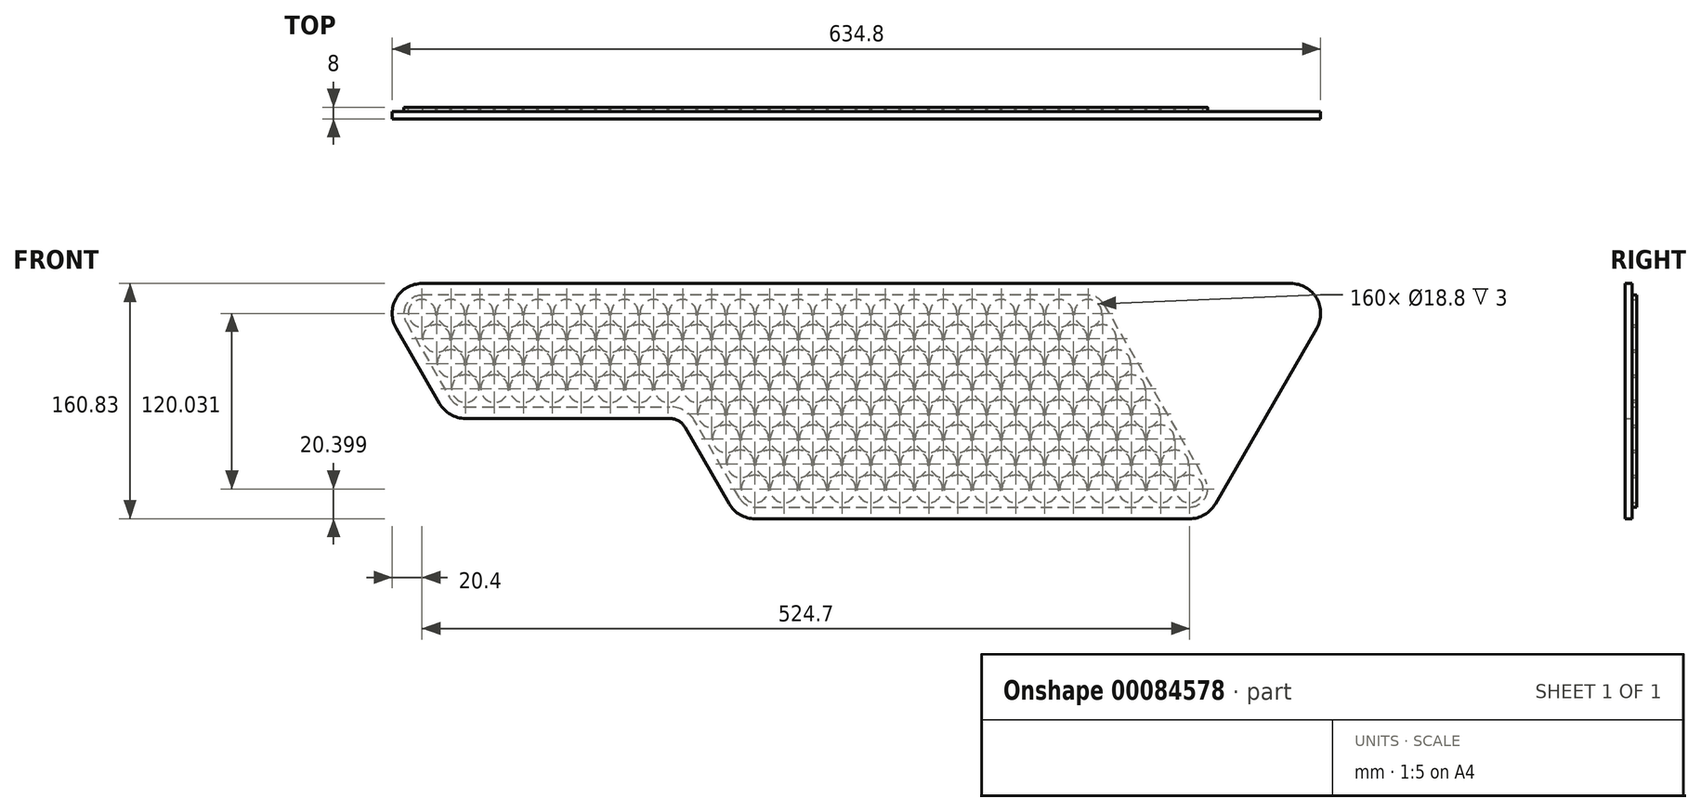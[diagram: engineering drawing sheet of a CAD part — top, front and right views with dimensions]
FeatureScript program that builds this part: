
annotation { "Feature Type Name" : "Feature", "Feature Type Description" : "" }
export const myFeature = defineFeature(function(context is Context, id is Id, definition is map)
    precondition{}
    {
        {
            var Q0;
            Q0=qCreatedBy(makeId("Front.planeOp"),FACE);
            var sketch = newSketch(context, id + "F0", { "sketchPlane" : qUnion([Q0]) });
            skCircle(sketch, "E0", {"center": v(0, 0) * mm, "radius": 9.4 * mm});
            skCircle(sketch, "E1.0.1.0", {"center": v(9.9, -17.15) * mm, "radius": 9.4 * mm});
            skCircle(sketch, "E1.0.2.0", {"center": v(19.8, -34.3) * mm, "radius": 9.4 * mm});
            skCircle(sketch, "E1.0.3.0", {"center": v(29.7, -51.44) * mm, "radius": 9.4 * mm});
            skCircle(sketch, "E1.1.0.0", {"center": v(19.8, 0) * mm, "radius": 9.4 * mm});
            skCircle(sketch, "E1.1.1.0", {"center": v(29.7, -17.15) * mm, "radius": 9.4 * mm});
            skCircle(sketch, "E1.1.2.0", {"center": v(39.6, -34.3) * mm, "radius": 9.4 * mm});
            skCircle(sketch, "E1.1.3.0", {"center": v(49.5, -51.44) * mm, "radius": 9.4 * mm});
            skCircle(sketch, "E1.2.0.0", {"center": v(39.6, 0) * mm, "radius": 9.4 * mm});
            skCircle(sketch, "E1.2.1.0", {"center": v(49.5, -17.15) * mm, "radius": 9.4 * mm});
            skCircle(sketch, "E1.2.2.0", {"center": v(59.4, -34.3) * mm, "radius": 9.4 * mm});
            skCircle(sketch, "E1.2.3.0", {"center": v(69.3, -51.44) * mm, "radius": 9.4 * mm});
            skCircle(sketch, "E1.3.0.0", {"center": v(59.4, 0) * mm, "radius": 9.4 * mm});
            skCircle(sketch, "E1.3.1.0", {"center": v(69.3, -17.15) * mm, "radius": 9.4 * mm});
            skCircle(sketch, "E1.3.2.0", {"center": v(79.2, -34.3) * mm, "radius": 9.4 * mm});
            skCircle(sketch, "E1.3.3.0", {"center": v(89.1, -51.44) * mm, "radius": 9.4 * mm});
            skCircle(sketch, "E1.4.0.0", {"center": v(79.2, 0) * mm, "radius": 9.4 * mm});
            skCircle(sketch, "E1.4.1.0", {"center": v(89.1, -17.15) * mm, "radius": 9.4 * mm});
            skCircle(sketch, "E1.4.2.0", {"center": v(99, -34.3) * mm, "radius": 9.4 * mm});
            skCircle(sketch, "E1.4.3.0", {"center": v(108.9, -51.44) * mm, "radius": 9.4 * mm});
            skCircle(sketch, "E1.5.0.0", {"center": v(99, 0) * mm, "radius": 9.4 * mm});
            skCircle(sketch, "E1.5.1.0", {"center": v(108.9, -17.15) * mm, "radius": 9.4 * mm});
            skCircle(sketch, "E1.5.2.0", {"center": v(118.8, -34.3) * mm, "radius": 9.4 * mm});
            skCircle(sketch, "E1.5.3.0", {"center": v(128.7, -51.44) * mm, "radius": 9.4 * mm});
            skCircle(sketch, "E1.6.0.0", {"center": v(118.8, 0) * mm, "radius": 9.4 * mm});
            skCircle(sketch, "E1.6.1.0", {"center": v(128.7, -17.15) * mm, "radius": 9.4 * mm});
            skCircle(sketch, "E1.6.2.0", {"center": v(138.6, -34.3) * mm, "radius": 9.4 * mm});
            skCircle(sketch, "E1.6.3.0", {"center": v(148.5, -51.44) * mm, "radius": 9.4 * mm});
            skCircle(sketch, "E1.7.0.0", {"center": v(138.6, 0) * mm, "radius": 9.4 * mm});
            skCircle(sketch, "E1.7.1.0", {"center": v(148.5, -17.15) * mm, "radius": 9.4 * mm});
            skCircle(sketch, "E1.7.2.0", {"center": v(158.4, -34.3) * mm, "radius": 9.4 * mm});
            skCircle(sketch, "E1.7.3.0", {"center": v(168.3, -51.44) * mm, "radius": 9.4 * mm});
            skCircle(sketch, "E1.8.0.0", {"center": v(158.4, 0) * mm, "radius": 9.4 * mm});
            skCircle(sketch, "E1.8.1.0", {"center": v(168.3, -17.15) * mm, "radius": 9.4 * mm});
            skCircle(sketch, "E1.8.2.0", {"center": v(178.2, -34.3) * mm, "radius": 9.4 * mm});
            skCircle(sketch, "E1.8.3.0", {"center": v(188.1, -51.44) * mm, "radius": 9.4 * mm});
            skCircle(sketch, "E1.9.0.0", {"center": v(178.2, 0) * mm, "radius": 9.4 * mm});
            skCircle(sketch, "E1.9.1.0", {"center": v(188.1, -17.15) * mm, "radius": 9.4 * mm});
            skCircle(sketch, "E1.9.2.0", {"center": v(198, -34.3) * mm, "radius": 9.4 * mm});
            skCircle(sketch, "E1.9.3.0", {"center": v(207.9, -51.44) * mm, "radius": 9.4 * mm});
            skLineSegment(sketch, "E1.direction1", {"start": v(0, 0) * mm, "end": v(19.8, 0) * mm, "construction": true});
            skLineSegment(sketch, "E1.direction2", {"start": v(0, 0) * mm, "end": v(9.9, -17.15) * mm, "construction": true});
            skCircle(sketch, "E2.0.10.0", {"center": v(198, 0) * mm, "radius": 9.4 * mm});
            skCircle(sketch, "E2.0.10.1", {"center": v(207.9, -17.15) * mm, "radius": 9.4 * mm});
            skCircle(sketch, "E2.0.10.2", {"center": v(217.8, -34.3) * mm, "radius": 9.4 * mm});
            skCircle(sketch, "E2.0.10.3", {"center": v(227.7, -51.44) * mm, "radius": 9.4 * mm});
            skCircle(sketch, "E2.0.11.0", {"center": v(217.8, 0) * mm, "radius": 9.4 * mm});
            skCircle(sketch, "E2.0.11.1", {"center": v(227.7, -17.15) * mm, "radius": 9.4 * mm});
            skCircle(sketch, "E2.0.11.2", {"center": v(237.6, -34.3) * mm, "radius": 9.4 * mm});
            skCircle(sketch, "E2.0.11.3", {"center": v(247.5, -51.44) * mm, "radius": 9.4 * mm});
            skCircle(sketch, "E2.0.12.0", {"center": v(237.6, 0) * mm, "radius": 9.4 * mm});
            skCircle(sketch, "E2.0.12.1", {"center": v(247.5, -17.15) * mm, "radius": 9.4 * mm});
            skCircle(sketch, "E2.0.12.2", {"center": v(257.4, -34.3) * mm, "radius": 9.4 * mm});
            skCircle(sketch, "E2.0.12.3", {"center": v(267.3, -51.44) * mm, "radius": 9.4 * mm});
            skCircle(sketch, "E2.0.13.0", {"center": v(257.4, 0) * mm, "radius": 9.4 * mm});
            skCircle(sketch, "E2.0.13.1", {"center": v(267.3, -17.15) * mm, "radius": 9.4 * mm});
            skCircle(sketch, "E2.0.13.2", {"center": v(277.2, -34.3) * mm, "radius": 9.4 * mm});
            skCircle(sketch, "E2.0.13.3", {"center": v(287.1, -51.44) * mm, "radius": 9.4 * mm});
            skCircle(sketch, "E2.0.14.0", {"center": v(277.2, 0) * mm, "radius": 9.4 * mm});
            skCircle(sketch, "E2.0.14.1", {"center": v(287.1, -17.15) * mm, "radius": 9.4 * mm});
            skCircle(sketch, "E2.0.14.2", {"center": v(297, -34.3) * mm, "radius": 9.4 * mm});
            skCircle(sketch, "E2.0.14.3", {"center": v(306.9, -51.44) * mm, "radius": 9.4 * mm});
            skCircle(sketch, "E2.0.15.0", {"center": v(297, 0) * mm, "radius": 9.4 * mm});
            skCircle(sketch, "E2.0.15.1", {"center": v(306.9, -17.15) * mm, "radius": 9.4 * mm});
            skCircle(sketch, "E2.0.15.2", {"center": v(316.8, -34.3) * mm, "radius": 9.4 * mm});
            skCircle(sketch, "E2.0.15.3", {"center": v(326.7, -51.44) * mm, "radius": 9.4 * mm});
            skCircle(sketch, "E2.0.16.0", {"center": v(316.8, 0) * mm, "radius": 9.4 * mm});
            skCircle(sketch, "E2.0.16.1", {"center": v(326.7, -17.15) * mm, "radius": 9.4 * mm});
            skCircle(sketch, "E2.0.16.2", {"center": v(336.6, -34.3) * mm, "radius": 9.4 * mm});
            skCircle(sketch, "E2.0.16.3", {"center": v(346.5, -51.44) * mm, "radius": 9.4 * mm});
            skCircle(sketch, "E2.0.17.0", {"center": v(336.6, 0) * mm, "radius": 9.4 * mm});
            skCircle(sketch, "E2.0.17.1", {"center": v(346.5, -17.15) * mm, "radius": 9.4 * mm});
            skCircle(sketch, "E2.0.17.2", {"center": v(356.4, -34.3) * mm, "radius": 9.4 * mm});
            skCircle(sketch, "E2.0.17.3", {"center": v(366.3, -51.44) * mm, "radius": 9.4 * mm});
            skCircle(sketch, "E2.0.18.0", {"center": v(356.4, 0) * mm, "radius": 9.4 * mm});
            skCircle(sketch, "E2.0.18.1", {"center": v(366.3, -17.15) * mm, "radius": 9.4 * mm});
            skCircle(sketch, "E2.0.18.2", {"center": v(376.2, -34.3) * mm, "radius": 9.4 * mm});
            skCircle(sketch, "E2.0.18.3", {"center": v(386.1, -51.44) * mm, "radius": 9.4 * mm});
            skCircle(sketch, "E2.0.19.0", {"center": v(376.2, 0) * mm, "radius": 9.4 * mm});
            skCircle(sketch, "E2.0.19.1", {"center": v(386.1, -17.15) * mm, "radius": 9.4 * mm});
            skCircle(sketch, "E2.0.19.2", {"center": v(396, -34.3) * mm, "radius": 9.4 * mm});
            skCircle(sketch, "E2.0.19.3", {"center": v(405.9, -51.44) * mm, "radius": 9.4 * mm});
            skCircle(sketch, "E3.0.20.0", {"center": v(396, 0) * mm, "radius": 9.4 * mm});
            skCircle(sketch, "E3.0.20.1", {"center": v(405.9, -17.15) * mm, "radius": 9.4 * mm});
            skCircle(sketch, "E3.0.20.2", {"center": v(415.8, -34.3) * mm, "radius": 9.4 * mm});
            skCircle(sketch, "E3.0.20.3", {"center": v(425.7, -51.44) * mm, "radius": 9.4 * mm});
            skCircle(sketch, "E3.0.21.0", {"center": v(415.8, 0) * mm, "radius": 9.4 * mm});
            skCircle(sketch, "E3.0.21.1", {"center": v(425.7, -17.15) * mm, "radius": 9.4 * mm});
            skCircle(sketch, "E3.0.21.2", {"center": v(435.6, -34.3) * mm, "radius": 9.4 * mm});
            skCircle(sketch, "E3.0.21.3", {"center": v(445.5, -51.44) * mm, "radius": 9.4 * mm});
            skCircle(sketch, "E3.0.22.0", {"center": v(435.6, 0) * mm, "radius": 9.4 * mm});
            skCircle(sketch, "E3.0.22.1", {"center": v(445.5, -17.15) * mm, "radius": 9.4 * mm});
            skCircle(sketch, "E3.0.22.2", {"center": v(455.4, -34.3) * mm, "radius": 9.4 * mm});
            skCircle(sketch, "E3.0.22.3", {"center": v(465.3, -51.44) * mm, "radius": 9.4 * mm});
            skCircle(sketch, "E3.0.23.0", {"center": v(455.4, 0) * mm, "radius": 9.4 * mm});
            skCircle(sketch, "E3.0.23.1", {"center": v(465.3, -17.15) * mm, "radius": 9.4 * mm});
            skCircle(sketch, "E3.0.23.2", {"center": v(475.2, -34.3) * mm, "radius": 9.4 * mm});
            skCircle(sketch, "E3.0.23.3", {"center": v(485.1, -51.44) * mm, "radius": 9.4 * mm});
            skLineSegment(sketch, "E4", {"start": v(188.1, -51.44) * mm, "end": v(158.4, 0) * mm, "construction": true});
            skLineSegment(sketch, "E5", {"start": v(237.6, 0) * mm, "end": v(207.9, -51.44) * mm, "construction": true});
            skLineSegment(sketch, "E6", {"start": v(207.9, -51.44) * mm, "end": v(188.1, -85.74) * mm, "construction": true});
            skLineSegment(sketch, "E7", {"start": v(188.1, -51.44) * mm, "end": v(207.9, -85.74) * mm, "construction": true});
            skCircle(sketch, "E8", {"center": v(198, -68.59) * mm, "radius": 9.4 * mm});
            skCircle(sketch, "E9.0.1.0", {"center": v(207.9, -85.74) * mm, "radius": 9.4 * mm});
            skCircle(sketch, "E9.0.2.0", {"center": v(217.8, -102.88) * mm, "radius": 9.4 * mm});
            skCircle(sketch, "E9.0.3.0", {"center": v(227.7, -120.03) * mm, "radius": 9.4 * mm});
            skCircle(sketch, "E9.1.0.0", {"center": v(217.8, -68.59) * mm, "radius": 9.4 * mm});
            skCircle(sketch, "E9.1.1.0", {"center": v(227.7, -85.74) * mm, "radius": 9.4 * mm});
            skCircle(sketch, "E9.1.2.0", {"center": v(237.6, -102.88) * mm, "radius": 9.4 * mm});
            skCircle(sketch, "E9.1.3.0", {"center": v(247.5, -120.03) * mm, "radius": 9.4 * mm});
            skCircle(sketch, "E9.2.0.0", {"center": v(237.6, -68.59) * mm, "radius": 9.4 * mm});
            skCircle(sketch, "E9.2.1.0", {"center": v(247.5, -85.74) * mm, "radius": 9.4 * mm});
            skCircle(sketch, "E9.2.2.0", {"center": v(257.4, -102.88) * mm, "radius": 9.4 * mm});
            skCircle(sketch, "E9.2.3.0", {"center": v(267.3, -120.03) * mm, "radius": 9.4 * mm});
            skCircle(sketch, "E9.3.0.0", {"center": v(257.4, -68.59) * mm, "radius": 9.4 * mm});
            skCircle(sketch, "E9.3.1.0", {"center": v(267.3, -85.74) * mm, "radius": 9.4 * mm});
            skCircle(sketch, "E9.3.2.0", {"center": v(277.2, -102.88) * mm, "radius": 9.4 * mm});
            skCircle(sketch, "E9.3.3.0", {"center": v(287.1, -120.03) * mm, "radius": 9.4 * mm});
            skCircle(sketch, "E9.4.0.0", {"center": v(277.2, -68.59) * mm, "radius": 9.4 * mm});
            skCircle(sketch, "E9.4.1.0", {"center": v(287.1, -85.74) * mm, "radius": 9.4 * mm});
            skCircle(sketch, "E9.4.2.0", {"center": v(297, -102.88) * mm, "radius": 9.4 * mm});
            skCircle(sketch, "E9.4.3.0", {"center": v(306.9, -120.03) * mm, "radius": 9.4 * mm});
            skCircle(sketch, "E9.5.0.0", {"center": v(297, -68.59) * mm, "radius": 9.4 * mm});
            skCircle(sketch, "E9.5.1.0", {"center": v(306.9, -85.74) * mm, "radius": 9.4 * mm});
            skCircle(sketch, "E9.5.2.0", {"center": v(316.8, -102.88) * mm, "radius": 9.4 * mm});
            skCircle(sketch, "E9.5.3.0", {"center": v(326.7, -120.03) * mm, "radius": 9.4 * mm});
            skCircle(sketch, "E9.6.0.0", {"center": v(316.8, -68.59) * mm, "radius": 9.4 * mm});
            skCircle(sketch, "E9.6.1.0", {"center": v(326.7, -85.74) * mm, "radius": 9.4 * mm});
            skCircle(sketch, "E9.6.2.0", {"center": v(336.6, -102.88) * mm, "radius": 9.4 * mm});
            skCircle(sketch, "E9.6.3.0", {"center": v(346.5, -120.03) * mm, "radius": 9.4 * mm});
            skCircle(sketch, "E9.7.0.0", {"center": v(336.6, -68.59) * mm, "radius": 9.4 * mm});
            skCircle(sketch, "E9.7.1.0", {"center": v(346.5, -85.74) * mm, "radius": 9.4 * mm});
            skCircle(sketch, "E9.7.2.0", {"center": v(356.4, -102.88) * mm, "radius": 9.4 * mm});
            skCircle(sketch, "E9.7.3.0", {"center": v(366.3, -120.03) * mm, "radius": 9.4 * mm});
            skCircle(sketch, "E9.8.0.0", {"center": v(356.4, -68.59) * mm, "radius": 9.4 * mm});
            skCircle(sketch, "E9.8.1.0", {"center": v(366.3, -85.74) * mm, "radius": 9.4 * mm});
            skCircle(sketch, "E9.8.2.0", {"center": v(376.2, -102.88) * mm, "radius": 9.4 * mm});
            skCircle(sketch, "E9.8.3.0", {"center": v(386.1, -120.03) * mm, "radius": 9.4 * mm});
            skCircle(sketch, "E9.9.0.0", {"center": v(376.2, -68.59) * mm, "radius": 9.4 * mm});
            skCircle(sketch, "E9.9.1.0", {"center": v(386.1, -85.74) * mm, "radius": 9.4 * mm});
            skCircle(sketch, "E9.9.2.0", {"center": v(396, -102.88) * mm, "radius": 9.4 * mm});
            skCircle(sketch, "E9.9.3.0", {"center": v(405.9, -120.03) * mm, "radius": 9.4 * mm});
            skCircle(sketch, "E9.10.0.0", {"center": v(396, -68.59) * mm, "radius": 9.4 * mm});
            skCircle(sketch, "E9.10.1.0", {"center": v(405.9, -85.74) * mm, "radius": 9.4 * mm});
            skCircle(sketch, "E9.10.2.0", {"center": v(415.8, -102.88) * mm, "radius": 9.4 * mm});
            skCircle(sketch, "E9.10.3.0", {"center": v(425.7, -120.03) * mm, "radius": 9.4 * mm});
            skCircle(sketch, "E9.11.0.0", {"center": v(415.8, -68.59) * mm, "radius": 9.4 * mm});
            skCircle(sketch, "E9.11.1.0", {"center": v(425.7, -85.74) * mm, "radius": 9.4 * mm});
            skCircle(sketch, "E9.11.2.0", {"center": v(435.6, -102.88) * mm, "radius": 9.4 * mm});
            skCircle(sketch, "E9.11.3.0", {"center": v(445.5, -120.03) * mm, "radius": 9.4 * mm});
            skCircle(sketch, "E9.12.0.0", {"center": v(435.6, -68.59) * mm, "radius": 9.4 * mm});
            skCircle(sketch, "E9.12.1.0", {"center": v(445.5, -85.74) * mm, "radius": 9.4 * mm});
            skCircle(sketch, "E9.12.2.0", {"center": v(455.4, -102.88) * mm, "radius": 9.4 * mm});
            skCircle(sketch, "E9.12.3.0", {"center": v(465.3, -120.03) * mm, "radius": 9.4 * mm});
            skCircle(sketch, "E9.13.0.0", {"center": v(455.4, -68.59) * mm, "radius": 9.4 * mm});
            skCircle(sketch, "E9.13.1.0", {"center": v(465.3, -85.74) * mm, "radius": 9.4 * mm});
            skCircle(sketch, "E9.13.2.0", {"center": v(475.2, -102.88) * mm, "radius": 9.4 * mm});
            skCircle(sketch, "E9.13.3.0", {"center": v(485.1, -120.03) * mm, "radius": 9.4 * mm});
            skCircle(sketch, "E9.14.0.0", {"center": v(475.2, -68.59) * mm, "radius": 9.4 * mm});
            skCircle(sketch, "E9.14.1.0", {"center": v(485.1, -85.74) * mm, "radius": 9.4 * mm});
            skCircle(sketch, "E9.14.2.0", {"center": v(495, -102.88) * mm, "radius": 9.4 * mm});
            skCircle(sketch, "E9.14.3.0", {"center": v(504.9, -120.03) * mm, "radius": 9.4 * mm});
            skCircle(sketch, "E9.15.0.0", {"center": v(495, -68.59) * mm, "radius": 9.4 * mm});
            skCircle(sketch, "E9.15.1.0", {"center": v(504.9, -85.74) * mm, "radius": 9.4 * mm});
            skCircle(sketch, "E9.15.2.0", {"center": v(514.8, -102.88) * mm, "radius": 9.4 * mm});
            skCircle(sketch, "E9.15.3.0", {"center": v(524.7, -120.03) * mm, "radius": 9.4 * mm});
            skLineSegment(sketch, "E9.direction1", {"start": v(198, -68.59) * mm, "end": v(217.8, -68.59) * mm, "construction": true});
            skLineSegment(sketch, "E9.direction2", {"start": v(198, -68.59) * mm, "end": v(207.9, -85.74) * mm, "construction": true});
            skCircle(sketch, "E10.0", {"center": v(0, 0) * mm, "radius": 12.4 * mm});
            skCircle(sketch, "E11.0", {"center": v(29.7, -51.44) * mm, "radius": 12.4 * mm});
            skCircle(sketch, "E12.0", {"center": v(455.4, 0) * mm, "radius": 12.4 * mm});
            skCircle(sketch, "E13.0", {"center": v(524.7, -120.03) * mm, "radius": 12.4 * mm});
            skCircle(sketch, "E14.0", {"center": v(227.7, -120.03) * mm, "radius": 12.4 * mm});
            skCircle(sketch, "E15.0", {"center": v(198, -68.59) * mm, "radius": 12.4 * mm});
            skLineSegment(sketch, "E16", {"start": v(-10.74, -6.2) * mm, "end": v(18.96, -57.64) * mm});
            skLineSegment(sketch, "E17", {"start": v(455.4, 12.4) * mm, "end": v(0, 12.4) * mm});
            skLineSegment(sketch, "E18", {"start": v(466.14, 6.2) * mm, "end": v(535.44, -113.83) * mm});
            skLineSegment(sketch, "E19", {"start": v(227.7, -132.43) * mm, "end": v(524.7, -132.43) * mm});
            skLineSegment(sketch, "E20", {"start": v(216.96, -126.23) * mm, "end": v(187.26, -74.79) * mm});
            skCircle(sketch, "E21.0", {"center": v(168.3, -51.44) * mm, "radius": 12.4 * mm});
            skLineSegment(sketch, "E22", {"start": v(29.7, -63.84) * mm, "end": v(168.3, -63.84) * mm});
            skLineSegment(sketch, "E23", {"start": v(168.3, -63.84) * mm, "end": v(180.94, -63.84) * mm});
            skLineSegment(sketch, "E24", {"start": v(187.26, -74.79) * mm, "end": v(180.94, -63.84) * mm});
            skSolve(sketch);
        }
        {
            var Q0;
            Q0=qSketchRegion(id+"F0",true);
            extrude(context, id + "F1", {"entities" : qUnion([Q0]), "depth" : 3 * mm});
        }
        {
            var Q0;
            Q0=makeQuery(id+"F1.opExtrude","SWEPT_EDGE",EDGE,{"disambiguationData":[OSD([sQuery(id+"F0.wireOp",EDGE,"E23"),sQuery(id+"F0.wireOp",EDGE,"E24")])]});
            fillet(context, id + "F2", {"entities" : qUnion([Q0]), "radius" : 20 * mm, "tangentPropagation" : true, "conicFillet" : false});
        }
        {
            var Q0;
            Q0=makeQuery(id+"F1.opExtrude","CAP_FACE",FACE,{"disambiguationData":[OSD([sQuery(id+"F0.wireOp",EDGE,"E0"),sQuery(id+"F0.wireOp",EDGE,"E1.0.1.0"),sQuery(id+"F0.wireOp",EDGE,"E1.0.2.0"),sQuery(id+"F0.wireOp",EDGE,"E1.0.3.0"),sQuery(id+"F0.wireOp",EDGE,"E1.1.0.0"),sQuery(id+"F0.wireOp",EDGE,"E1.1.1.0"),sQuery(id+"F0.wireOp",EDGE,"E1.1.2.0"),sQuery(id+"F0.wireOp",EDGE,"E1.1.3.0"),sQuery(id+"F0.wireOp",EDGE,"E1.2.0.0"),sQuery(id+"F0.wireOp",EDGE,"E1.2.1.0"),sQuery(id+"F0.wireOp",EDGE,"E1.2.2.0"),sQuery(id+"F0.wireOp",EDGE,"E1.2.3.0"),sQuery(id+"F0.wireOp",EDGE,"E1.3.0.0"),sQuery(id+"F0.wireOp",EDGE,"E1.3.1.0"),sQuery(id+"F0.wireOp",EDGE,"E1.3.2.0"),sQuery(id+"F0.wireOp",EDGE,"E1.3.3.0"),sQuery(id+"F0.wireOp",EDGE,"E1.4.0.0"),sQuery(id+"F0.wireOp",EDGE,"E1.4.1.0"),sQuery(id+"F0.wireOp",EDGE,"E1.4.2.0"),sQuery(id+"F0.wireOp",EDGE,"E1.4.3.0"),sQuery(id+"F0.wireOp",EDGE,"E1.5.0.0"),sQuery(id+"F0.wireOp",EDGE,"E1.5.1.0"),sQuery(id+"F0.wireOp",EDGE,"E1.5.2.0"),sQuery(id+"F0.wireOp",EDGE,"E1.5.3.0"),sQuery(id+"F0.wireOp",EDGE,"E1.6.0.0"),sQuery(id+"F0.wireOp",EDGE,"E1.6.1.0"),sQuery(id+"F0.wireOp",EDGE,"E1.6.2.0"),sQuery(id+"F0.wireOp",EDGE,"E1.6.3.0"),sQuery(id+"F0.wireOp",EDGE,"E1.7.0.0"),sQuery(id+"F0.wireOp",EDGE,"E1.7.1.0"),sQuery(id+"F0.wireOp",EDGE,"E1.7.2.0"),sQuery(id+"F0.wireOp",EDGE,"E1.7.3.0"),sQuery(id+"F0.wireOp",EDGE,"E1.8.0.0"),sQuery(id+"F0.wireOp",EDGE,"E1.8.1.0"),sQuery(id+"F0.wireOp",EDGE,"E1.8.2.0"),sQuery(id+"F0.wireOp",EDGE,"E1.8.3.0"),sQuery(id+"F0.wireOp",EDGE,"E1.9.0.0"),sQuery(id+"F0.wireOp",EDGE,"E1.9.1.0"),sQuery(id+"F0.wireOp",EDGE,"E1.9.2.0"),sQuery(id+"F0.wireOp",EDGE,"E1.9.3.0"),sQuery(id+"F0.wireOp",EDGE,"E2.0.10.0"),sQuery(id+"F0.wireOp",EDGE,"E2.0.10.1"),sQuery(id+"F0.wireOp",EDGE,"E2.0.10.2"),sQuery(id+"F0.wireOp",EDGE,"E2.0.10.3"),sQuery(id+"F0.wireOp",EDGE,"E2.0.11.0"),sQuery(id+"F0.wireOp",EDGE,"E2.0.11.1"),sQuery(id+"F0.wireOp",EDGE,"E2.0.11.2"),sQuery(id+"F0.wireOp",EDGE,"E2.0.11.3"),sQuery(id+"F0.wireOp",EDGE,"E2.0.12.0"),sQuery(id+"F0.wireOp",EDGE,"E2.0.12.1"),sQuery(id+"F0.wireOp",EDGE,"E2.0.12.2"),sQuery(id+"F0.wireOp",EDGE,"E2.0.12.3"),sQuery(id+"F0.wireOp",EDGE,"E2.0.13.0"),sQuery(id+"F0.wireOp",EDGE,"E2.0.13.1"),sQuery(id+"F0.wireOp",EDGE,"E2.0.13.2"),sQuery(id+"F0.wireOp",EDGE,"E2.0.13.3"),sQuery(id+"F0.wireOp",EDGE,"E2.0.14.0"),sQuery(id+"F0.wireOp",EDGE,"E2.0.14.1"),sQuery(id+"F0.wireOp",EDGE,"E2.0.14.2"),sQuery(id+"F0.wireOp",EDGE,"E2.0.14.3"),sQuery(id+"F0.wireOp",EDGE,"E2.0.15.0"),sQuery(id+"F0.wireOp",EDGE,"E2.0.15.1"),sQuery(id+"F0.wireOp",EDGE,"E2.0.15.2"),sQuery(id+"F0.wireOp",EDGE,"E2.0.15.3"),sQuery(id+"F0.wireOp",EDGE,"E2.0.16.0"),sQuery(id+"F0.wireOp",EDGE,"E2.0.16.1"),sQuery(id+"F0.wireOp",EDGE,"E2.0.16.2"),sQuery(id+"F0.wireOp",EDGE,"E2.0.16.3"),sQuery(id+"F0.wireOp",EDGE,"E2.0.17.0"),sQuery(id+"F0.wireOp",EDGE,"E2.0.17.1"),sQuery(id+"F0.wireOp",EDGE,"E2.0.17.2"),sQuery(id+"F0.wireOp",EDGE,"E2.0.17.3"),sQuery(id+"F0.wireOp",EDGE,"E2.0.18.0"),sQuery(id+"F0.wireOp",EDGE,"E2.0.18.1"),sQuery(id+"F0.wireOp",EDGE,"E2.0.18.2"),sQuery(id+"F0.wireOp",EDGE,"E2.0.18.3"),sQuery(id+"F0.wireOp",EDGE,"E2.0.19.0"),sQuery(id+"F0.wireOp",EDGE,"E2.0.19.1"),sQuery(id+"F0.wireOp",EDGE,"E2.0.19.2"),sQuery(id+"F0.wireOp",EDGE,"E2.0.19.3"),sQuery(id+"F0.wireOp",EDGE,"E3.0.20.0"),sQuery(id+"F0.wireOp",EDGE,"E3.0.20.1"),sQuery(id+"F0.wireOp",EDGE,"E3.0.20.2"),sQuery(id+"F0.wireOp",EDGE,"E3.0.20.3"),sQuery(id+"F0.wireOp",EDGE,"E3.0.21.0"),sQuery(id+"F0.wireOp",EDGE,"E3.0.21.1"),sQuery(id+"F0.wireOp",EDGE,"E3.0.21.2"),sQuery(id+"F0.wireOp",EDGE,"E3.0.21.3"),sQuery(id+"F0.wireOp",EDGE,"E3.0.22.0"),sQuery(id+"F0.wireOp",EDGE,"E3.0.22.1"),sQuery(id+"F0.wireOp",EDGE,"E3.0.22.2"),sQuery(id+"F0.wireOp",EDGE,"E3.0.22.3"),sQuery(id+"F0.wireOp",EDGE,"E3.0.23.0"),sQuery(id+"F0.wireOp",EDGE,"E3.0.23.1"),sQuery(id+"F0.wireOp",EDGE,"E3.0.23.2"),sQuery(id+"F0.wireOp",EDGE,"E3.0.23.3"),sQuery(id+"F0.wireOp",EDGE,"E8"),sQuery(id+"F0.wireOp",EDGE,"E9.0.1.0"),sQuery(id+"F0.wireOp",EDGE,"E9.0.2.0"),sQuery(id+"F0.wireOp",EDGE,"E9.0.3.0"),sQuery(id+"F0.wireOp",EDGE,"E9.1.0.0"),sQuery(id+"F0.wireOp",EDGE,"E9.1.1.0"),sQuery(id+"F0.wireOp",EDGE,"E9.1.2.0"),sQuery(id+"F0.wireOp",EDGE,"E9.1.3.0"),sQuery(id+"F0.wireOp",EDGE,"E9.2.0.0"),sQuery(id+"F0.wireOp",EDGE,"E9.2.1.0"),sQuery(id+"F0.wireOp",EDGE,"E9.2.2.0"),sQuery(id+"F0.wireOp",EDGE,"E9.2.3.0"),sQuery(id+"F0.wireOp",EDGE,"E9.3.0.0"),sQuery(id+"F0.wireOp",EDGE,"E9.3.1.0"),sQuery(id+"F0.wireOp",EDGE,"E9.3.2.0"),sQuery(id+"F0.wireOp",EDGE,"E9.3.3.0"),sQuery(id+"F0.wireOp",EDGE,"E9.4.0.0"),sQuery(id+"F0.wireOp",EDGE,"E9.4.1.0"),sQuery(id+"F0.wireOp",EDGE,"E9.4.2.0"),sQuery(id+"F0.wireOp",EDGE,"E9.4.3.0"),sQuery(id+"F0.wireOp",EDGE,"E9.5.0.0"),sQuery(id+"F0.wireOp",EDGE,"E9.5.1.0"),sQuery(id+"F0.wireOp",EDGE,"E9.5.2.0"),sQuery(id+"F0.wireOp",EDGE,"E9.5.3.0"),sQuery(id+"F0.wireOp",EDGE,"E9.6.0.0"),sQuery(id+"F0.wireOp",EDGE,"E9.6.1.0"),sQuery(id+"F0.wireOp",EDGE,"E9.6.2.0"),sQuery(id+"F0.wireOp",EDGE,"E9.6.3.0"),sQuery(id+"F0.wireOp",EDGE,"E9.7.0.0"),sQuery(id+"F0.wireOp",EDGE,"E9.7.1.0"),sQuery(id+"F0.wireOp",EDGE,"E9.7.2.0"),sQuery(id+"F0.wireOp",EDGE,"E9.7.3.0"),sQuery(id+"F0.wireOp",EDGE,"E9.8.0.0"),sQuery(id+"F0.wireOp",EDGE,"E9.8.1.0"),sQuery(id+"F0.wireOp",EDGE,"E9.8.2.0"),sQuery(id+"F0.wireOp",EDGE,"E9.8.3.0"),sQuery(id+"F0.wireOp",EDGE,"E9.9.0.0"),sQuery(id+"F0.wireOp",EDGE,"E9.9.1.0"),sQuery(id+"F0.wireOp",EDGE,"E9.9.2.0"),sQuery(id+"F0.wireOp",EDGE,"E9.9.3.0"),sQuery(id+"F0.wireOp",EDGE,"E9.10.0.0"),sQuery(id+"F0.wireOp",EDGE,"E9.10.1.0"),sQuery(id+"F0.wireOp",EDGE,"E9.10.2.0"),sQuery(id+"F0.wireOp",EDGE,"E9.10.3.0"),sQuery(id+"F0.wireOp",EDGE,"E9.11.0.0"),sQuery(id+"F0.wireOp",EDGE,"E9.11.1.0"),sQuery(id+"F0.wireOp",EDGE,"E9.11.2.0"),sQuery(id+"F0.wireOp",EDGE,"E9.11.3.0"),sQuery(id+"F0.wireOp",EDGE,"E9.12.0.0"),sQuery(id+"F0.wireOp",EDGE,"E9.12.1.0"),sQuery(id+"F0.wireOp",EDGE,"E9.12.2.0"),sQuery(id+"F0.wireOp",EDGE,"E9.12.3.0"),sQuery(id+"F0.wireOp",EDGE,"E9.13.0.0"),sQuery(id+"F0.wireOp",EDGE,"E9.13.1.0"),sQuery(id+"F0.wireOp",EDGE,"E9.13.2.0"),sQuery(id+"F0.wireOp",EDGE,"E9.13.3.0"),sQuery(id+"F0.wireOp",EDGE,"E9.14.0.0"),sQuery(id+"F0.wireOp",EDGE,"E9.14.1.0"),sQuery(id+"F0.wireOp",EDGE,"E9.14.2.0"),sQuery(id+"F0.wireOp",EDGE,"E9.14.3.0"),sQuery(id+"F0.wireOp",EDGE,"E9.15.0.0"),sQuery(id+"F0.wireOp",EDGE,"E9.15.1.0"),sQuery(id+"F0.wireOp",EDGE,"E9.15.2.0"),sQuery(id+"F0.wireOp",EDGE,"E9.15.3.0"),sQuery(id+"F0.wireOp",EDGE,"E10.0"),sQuery(id+"F0.wireOp",EDGE,"E11.0"),sQuery(id+"F0.wireOp",EDGE,"E12.0"),sQuery(id+"F0.wireOp",EDGE,"E13.0"),sQuery(id+"F0.wireOp",EDGE,"E14.0"),sQuery(id+"F0.wireOp",EDGE,"E16"),sQuery(id+"F0.wireOp",EDGE,"E17"),sQuery(id+"F0.wireOp",EDGE,"E18"),sQuery(id+"F0.wireOp",EDGE,"E19"),sQuery(id+"F0.wireOp",EDGE,"E20"),sQuery(id+"F0.wireOp",EDGE,"E22"),sQuery(id+"F0.wireOp",EDGE,"E23"),sQuery(id+"F0.wireOp",EDGE,"E24")])],"isStart":false});
            var sketch = newSketch(context, id + "F3", { "sketchPlane" : qUnion([Q0]) });
            skLineSegment(sketch, "E25.0", {"start": v(455.4, 12.4) * mm, "end": v(0, 12.4) * mm});
            skLineSegment(sketch, "E25.1", {"start": v(-10.74, -6.2) * mm, "end": v(18.96, -57.64) * mm});
            skLineSegment(sketch, "E25.2", {"start": v(29.7, -63.84) * mm, "end": v(169.4, -63.84) * mm});
            skLineSegment(sketch, "E25.3", {"start": v(216.96, -126.23) * mm, "end": v(186.71, -73.84) * mm});
            skLineSegment(sketch, "E25.4", {"start": v(227.7, -132.43) * mm, "end": v(524.7, -132.43) * mm});
            skLineSegment(sketch, "E25.5", {"start": v(466.14, 6.2) * mm, "end": v(535.44, -113.83) * mm});
            skArc(sketch, "E25.6", {"start": v(466.14, 6.2) * mm, "mid": v(461.6, 10.74) * mm, "end": v(455.4, 12.4) * mm});
            skArc(sketch, "E25.7", {"start": v(524.7, -132.43) * mm, "mid": v(535.44, -126.23) * mm, "end": v(535.44, -113.83) * mm});
            skArc(sketch, "E25.8", {"start": v(216.96, -126.23) * mm, "mid": v(221.5, -130.77) * mm, "end": v(227.7, -132.43) * mm});
            skArc(sketch, "E25.9", {"start": v(169.4, -63.84) * mm, "mid": v(179.4, -66.52) * mm, "end": v(186.71, -73.84) * mm});
            skArc(sketch, "E25.10", {"start": v(18.96, -57.64) * mm, "mid": v(23.5, -62.18) * mm, "end": v(29.7, -63.84) * mm});
            skArc(sketch, "E25.11", {"start": v(0, 12.4) * mm, "mid": v(-10.74, 6.2) * mm, "end": v(-10.74, -6.2) * mm});
            skSolve(sketch);
        }
        {
            var Q0;
            Q0=qSketchRegion(id+"F3",true);
            extrude(context, id + "F4", {"entities" : qUnion([Q0]), "depth" : 2 * mm});
        }
        {
            var Q0;
            Q0=makeQuery(id+"F1.opExtrude","CAP_FACE",FACE,{"disambiguationData":[OSD([sQuery(id+"F0.wireOp",EDGE,"E0"),sQuery(id+"F0.wireOp",EDGE,"E1.0.1.0"),sQuery(id+"F0.wireOp",EDGE,"E1.0.2.0"),sQuery(id+"F0.wireOp",EDGE,"E1.0.3.0"),sQuery(id+"F0.wireOp",EDGE,"E1.1.0.0"),sQuery(id+"F0.wireOp",EDGE,"E1.1.1.0"),sQuery(id+"F0.wireOp",EDGE,"E1.1.2.0"),sQuery(id+"F0.wireOp",EDGE,"E1.1.3.0"),sQuery(id+"F0.wireOp",EDGE,"E1.2.0.0"),sQuery(id+"F0.wireOp",EDGE,"E1.2.1.0"),sQuery(id+"F0.wireOp",EDGE,"E1.2.2.0"),sQuery(id+"F0.wireOp",EDGE,"E1.2.3.0"),sQuery(id+"F0.wireOp",EDGE,"E1.3.0.0"),sQuery(id+"F0.wireOp",EDGE,"E1.3.1.0"),sQuery(id+"F0.wireOp",EDGE,"E1.3.2.0"),sQuery(id+"F0.wireOp",EDGE,"E1.3.3.0"),sQuery(id+"F0.wireOp",EDGE,"E1.4.0.0"),sQuery(id+"F0.wireOp",EDGE,"E1.4.1.0"),sQuery(id+"F0.wireOp",EDGE,"E1.4.2.0"),sQuery(id+"F0.wireOp",EDGE,"E1.4.3.0"),sQuery(id+"F0.wireOp",EDGE,"E1.5.0.0"),sQuery(id+"F0.wireOp",EDGE,"E1.5.1.0"),sQuery(id+"F0.wireOp",EDGE,"E1.5.2.0"),sQuery(id+"F0.wireOp",EDGE,"E1.5.3.0"),sQuery(id+"F0.wireOp",EDGE,"E1.6.0.0"),sQuery(id+"F0.wireOp",EDGE,"E1.6.1.0"),sQuery(id+"F0.wireOp",EDGE,"E1.6.2.0"),sQuery(id+"F0.wireOp",EDGE,"E1.6.3.0"),sQuery(id+"F0.wireOp",EDGE,"E1.7.0.0"),sQuery(id+"F0.wireOp",EDGE,"E1.7.1.0"),sQuery(id+"F0.wireOp",EDGE,"E1.7.2.0"),sQuery(id+"F0.wireOp",EDGE,"E1.7.3.0"),sQuery(id+"F0.wireOp",EDGE,"E1.8.0.0"),sQuery(id+"F0.wireOp",EDGE,"E1.8.1.0"),sQuery(id+"F0.wireOp",EDGE,"E1.8.2.0"),sQuery(id+"F0.wireOp",EDGE,"E1.8.3.0"),sQuery(id+"F0.wireOp",EDGE,"E1.9.0.0"),sQuery(id+"F0.wireOp",EDGE,"E1.9.1.0"),sQuery(id+"F0.wireOp",EDGE,"E1.9.2.0"),sQuery(id+"F0.wireOp",EDGE,"E1.9.3.0"),sQuery(id+"F0.wireOp",EDGE,"E2.0.10.0"),sQuery(id+"F0.wireOp",EDGE,"E2.0.10.1"),sQuery(id+"F0.wireOp",EDGE,"E2.0.10.2"),sQuery(id+"F0.wireOp",EDGE,"E2.0.10.3"),sQuery(id+"F0.wireOp",EDGE,"E2.0.11.0"),sQuery(id+"F0.wireOp",EDGE,"E2.0.11.1"),sQuery(id+"F0.wireOp",EDGE,"E2.0.11.2"),sQuery(id+"F0.wireOp",EDGE,"E2.0.11.3"),sQuery(id+"F0.wireOp",EDGE,"E2.0.12.0"),sQuery(id+"F0.wireOp",EDGE,"E2.0.12.1"),sQuery(id+"F0.wireOp",EDGE,"E2.0.12.2"),sQuery(id+"F0.wireOp",EDGE,"E2.0.12.3"),sQuery(id+"F0.wireOp",EDGE,"E2.0.13.0"),sQuery(id+"F0.wireOp",EDGE,"E2.0.13.1"),sQuery(id+"F0.wireOp",EDGE,"E2.0.13.2"),sQuery(id+"F0.wireOp",EDGE,"E2.0.13.3"),sQuery(id+"F0.wireOp",EDGE,"E2.0.14.0"),sQuery(id+"F0.wireOp",EDGE,"E2.0.14.1"),sQuery(id+"F0.wireOp",EDGE,"E2.0.14.2"),sQuery(id+"F0.wireOp",EDGE,"E2.0.14.3"),sQuery(id+"F0.wireOp",EDGE,"E2.0.15.0"),sQuery(id+"F0.wireOp",EDGE,"E2.0.15.1"),sQuery(id+"F0.wireOp",EDGE,"E2.0.15.2"),sQuery(id+"F0.wireOp",EDGE,"E2.0.15.3"),sQuery(id+"F0.wireOp",EDGE,"E2.0.16.0"),sQuery(id+"F0.wireOp",EDGE,"E2.0.16.1"),sQuery(id+"F0.wireOp",EDGE,"E2.0.16.2"),sQuery(id+"F0.wireOp",EDGE,"E2.0.16.3"),sQuery(id+"F0.wireOp",EDGE,"E2.0.17.0"),sQuery(id+"F0.wireOp",EDGE,"E2.0.17.1"),sQuery(id+"F0.wireOp",EDGE,"E2.0.17.2"),sQuery(id+"F0.wireOp",EDGE,"E2.0.17.3"),sQuery(id+"F0.wireOp",EDGE,"E2.0.18.0"),sQuery(id+"F0.wireOp",EDGE,"E2.0.18.1"),sQuery(id+"F0.wireOp",EDGE,"E2.0.18.2"),sQuery(id+"F0.wireOp",EDGE,"E2.0.18.3"),sQuery(id+"F0.wireOp",EDGE,"E2.0.19.0"),sQuery(id+"F0.wireOp",EDGE,"E2.0.19.1"),sQuery(id+"F0.wireOp",EDGE,"E2.0.19.2"),sQuery(id+"F0.wireOp",EDGE,"E2.0.19.3"),sQuery(id+"F0.wireOp",EDGE,"E3.0.20.0"),sQuery(id+"F0.wireOp",EDGE,"E3.0.20.1"),sQuery(id+"F0.wireOp",EDGE,"E3.0.20.2"),sQuery(id+"F0.wireOp",EDGE,"E3.0.20.3"),sQuery(id+"F0.wireOp",EDGE,"E3.0.21.0"),sQuery(id+"F0.wireOp",EDGE,"E3.0.21.1"),sQuery(id+"F0.wireOp",EDGE,"E3.0.21.2"),sQuery(id+"F0.wireOp",EDGE,"E3.0.21.3"),sQuery(id+"F0.wireOp",EDGE,"E3.0.22.0"),sQuery(id+"F0.wireOp",EDGE,"E3.0.22.1"),sQuery(id+"F0.wireOp",EDGE,"E3.0.22.2"),sQuery(id+"F0.wireOp",EDGE,"E3.0.22.3"),sQuery(id+"F0.wireOp",EDGE,"E3.0.23.0"),sQuery(id+"F0.wireOp",EDGE,"E3.0.23.1"),sQuery(id+"F0.wireOp",EDGE,"E3.0.23.2"),sQuery(id+"F0.wireOp",EDGE,"E3.0.23.3"),sQuery(id+"F0.wireOp",EDGE,"E8"),sQuery(id+"F0.wireOp",EDGE,"E9.0.1.0"),sQuery(id+"F0.wireOp",EDGE,"E9.0.2.0"),sQuery(id+"F0.wireOp",EDGE,"E9.0.3.0"),sQuery(id+"F0.wireOp",EDGE,"E9.1.0.0"),sQuery(id+"F0.wireOp",EDGE,"E9.1.1.0"),sQuery(id+"F0.wireOp",EDGE,"E9.1.2.0"),sQuery(id+"F0.wireOp",EDGE,"E9.1.3.0"),sQuery(id+"F0.wireOp",EDGE,"E9.2.0.0"),sQuery(id+"F0.wireOp",EDGE,"E9.2.1.0"),sQuery(id+"F0.wireOp",EDGE,"E9.2.2.0"),sQuery(id+"F0.wireOp",EDGE,"E9.2.3.0"),sQuery(id+"F0.wireOp",EDGE,"E9.3.0.0"),sQuery(id+"F0.wireOp",EDGE,"E9.3.1.0"),sQuery(id+"F0.wireOp",EDGE,"E9.3.2.0"),sQuery(id+"F0.wireOp",EDGE,"E9.3.3.0"),sQuery(id+"F0.wireOp",EDGE,"E9.4.0.0"),sQuery(id+"F0.wireOp",EDGE,"E9.4.1.0"),sQuery(id+"F0.wireOp",EDGE,"E9.4.2.0"),sQuery(id+"F0.wireOp",EDGE,"E9.4.3.0"),sQuery(id+"F0.wireOp",EDGE,"E9.5.0.0"),sQuery(id+"F0.wireOp",EDGE,"E9.5.1.0"),sQuery(id+"F0.wireOp",EDGE,"E9.5.2.0"),sQuery(id+"F0.wireOp",EDGE,"E9.5.3.0"),sQuery(id+"F0.wireOp",EDGE,"E9.6.0.0"),sQuery(id+"F0.wireOp",EDGE,"E9.6.1.0"),sQuery(id+"F0.wireOp",EDGE,"E9.6.2.0"),sQuery(id+"F0.wireOp",EDGE,"E9.6.3.0"),sQuery(id+"F0.wireOp",EDGE,"E9.7.0.0"),sQuery(id+"F0.wireOp",EDGE,"E9.7.1.0"),sQuery(id+"F0.wireOp",EDGE,"E9.7.2.0"),sQuery(id+"F0.wireOp",EDGE,"E9.7.3.0"),sQuery(id+"F0.wireOp",EDGE,"E9.8.0.0"),sQuery(id+"F0.wireOp",EDGE,"E9.8.1.0"),sQuery(id+"F0.wireOp",EDGE,"E9.8.2.0"),sQuery(id+"F0.wireOp",EDGE,"E9.8.3.0"),sQuery(id+"F0.wireOp",EDGE,"E9.9.0.0"),sQuery(id+"F0.wireOp",EDGE,"E9.9.1.0"),sQuery(id+"F0.wireOp",EDGE,"E9.9.2.0"),sQuery(id+"F0.wireOp",EDGE,"E9.9.3.0"),sQuery(id+"F0.wireOp",EDGE,"E9.10.0.0"),sQuery(id+"F0.wireOp",EDGE,"E9.10.1.0"),sQuery(id+"F0.wireOp",EDGE,"E9.10.2.0"),sQuery(id+"F0.wireOp",EDGE,"E9.10.3.0"),sQuery(id+"F0.wireOp",EDGE,"E9.11.0.0"),sQuery(id+"F0.wireOp",EDGE,"E9.11.1.0"),sQuery(id+"F0.wireOp",EDGE,"E9.11.2.0"),sQuery(id+"F0.wireOp",EDGE,"E9.11.3.0"),sQuery(id+"F0.wireOp",EDGE,"E9.12.0.0"),sQuery(id+"F0.wireOp",EDGE,"E9.12.1.0"),sQuery(id+"F0.wireOp",EDGE,"E9.12.2.0"),sQuery(id+"F0.wireOp",EDGE,"E9.12.3.0"),sQuery(id+"F0.wireOp",EDGE,"E9.13.0.0"),sQuery(id+"F0.wireOp",EDGE,"E9.13.1.0"),sQuery(id+"F0.wireOp",EDGE,"E9.13.2.0"),sQuery(id+"F0.wireOp",EDGE,"E9.13.3.0"),sQuery(id+"F0.wireOp",EDGE,"E9.14.0.0"),sQuery(id+"F0.wireOp",EDGE,"E9.14.1.0"),sQuery(id+"F0.wireOp",EDGE,"E9.14.2.0"),sQuery(id+"F0.wireOp",EDGE,"E9.14.3.0"),sQuery(id+"F0.wireOp",EDGE,"E9.15.0.0"),sQuery(id+"F0.wireOp",EDGE,"E9.15.1.0"),sQuery(id+"F0.wireOp",EDGE,"E9.15.2.0"),sQuery(id+"F0.wireOp",EDGE,"E9.15.3.0"),sQuery(id+"F0.wireOp",EDGE,"E10.0"),sQuery(id+"F0.wireOp",EDGE,"E11.0"),sQuery(id+"F0.wireOp",EDGE,"E12.0"),sQuery(id+"F0.wireOp",EDGE,"E13.0"),sQuery(id+"F0.wireOp",EDGE,"E14.0"),sQuery(id+"F0.wireOp",EDGE,"E16"),sQuery(id+"F0.wireOp",EDGE,"E17"),sQuery(id+"F0.wireOp",EDGE,"E18"),sQuery(id+"F0.wireOp",EDGE,"E19"),sQuery(id+"F0.wireOp",EDGE,"E20"),sQuery(id+"F0.wireOp",EDGE,"E22"),sQuery(id+"F0.wireOp",EDGE,"E23"),sQuery(id+"F0.wireOp",EDGE,"E24")])],"isStart":false});
            var sketch = newSketch(context, id + "F5", { "sketchPlane" : qUnion([Q0]) });
            skArc(sketch, "E26.0", {"start": v(-8.5, 4) * mm, "mid": v(-9.4, 0) * mm, "end": v(-8.5, -4) * mm});
            skArc(sketch, "E26.1", {"start": v(21.2, -47.44) * mm, "mid": v(20.3, -51.44) * mm, "end": v(21.2, -55.44) * mm});
            skLineSegment(sketch, "E27", {"start": v(0, 0) * mm, "end": v(455.4, 0) * mm, "construction": true});
            skLineSegment(sketch, "E28", {"start": v(0, 0) * mm, "end": v(29.7, -51.44) * mm, "construction": true});
            skLineSegment(sketch, "E29", {"start": v(198, -68.59) * mm, "end": v(495, -68.59) * mm, "construction": true});
            skLineSegment(sketch, "E30", {"start": v(198, -68.59) * mm, "end": v(227.7, -120.03) * mm, "construction": true});
            skLineSegment(sketch, "E31.0.left", {"start": v(0, 4) * mm, "end": v(463.9, 4) * mm});
            skLineSegment(sketch, "E31.0.right", {"start": v(0, -4) * mm, "end": v(463.9, -4) * mm});
            skLineSegment(sketch, "E32", {"start": v(0, 4) * mm, "end": v(-8.5, 4) * mm});
            skLineSegment(sketch, "E33", {"start": v(0, -4) * mm, "end": v(-8.5, -4) * mm});
            skArc(sketch, "E34.trimOffspring", {"start": v(463.9, -4) * mm, "mid": v(464.8, 0) * mm, "end": v(463.9, 4) * mm});
            skArc(sketch, "E35.0.1.0", {"start": v(1.4, -13.15) * mm, "mid": v(0.5, -17.15) * mm, "end": v(1.4, -21.15) * mm});
            skLineSegment(sketch, "E35.0.1.1", {"start": v(9.9, -13.15) * mm, "end": v(1.4, -13.15) * mm});
            skLineSegment(sketch, "E35.0.1.2", {"start": v(9.9, -21.15) * mm, "end": v(1.4, -21.15) * mm});
            skLineSegment(sketch, "E35.0.1.3", {"start": v(9.9, -13.15) * mm, "end": v(473.8, -13.15) * mm});
            skLineSegment(sketch, "E35.0.1.4", {"start": v(9.9, -21.15) * mm, "end": v(473.8, -21.15) * mm});
            skArc(sketch, "E35.0.1.5", {"start": v(473.8, -21.15) * mm, "mid": v(474.7, -17.15) * mm, "end": v(473.8, -13.15) * mm});
            skArc(sketch, "E35.0.2.0", {"start": v(11.3, -30.3) * mm, "mid": v(10.4, -34.3) * mm, "end": v(11.3, -38.3) * mm});
            skLineSegment(sketch, "E35.0.2.1", {"start": v(19.8, -30.3) * mm, "end": v(11.3, -30.3) * mm});
            skLineSegment(sketch, "E35.0.2.2", {"start": v(19.8, -38.3) * mm, "end": v(11.3, -38.3) * mm});
            skLineSegment(sketch, "E35.0.2.3", {"start": v(19.8, -30.3) * mm, "end": v(483.7, -30.3) * mm});
            skLineSegment(sketch, "E35.0.2.4", {"start": v(19.8, -38.3) * mm, "end": v(483.7, -38.3) * mm});
            skArc(sketch, "E35.0.2.5", {"start": v(483.7, -38.3) * mm, "mid": v(484.6, -34.3) * mm, "end": v(483.7, -30.3) * mm});
            skLineSegment(sketch, "E35.0.3.1", {"start": v(29.7, -47.44) * mm, "end": v(21.2, -47.44) * mm});
            skLineSegment(sketch, "E35.0.3.2", {"start": v(29.7, -55.44) * mm, "end": v(21.2, -55.44) * mm});
            skLineSegment(sketch, "E35.0.3.3", {"start": v(29.7, -47.44) * mm, "end": v(493.6, -47.44) * mm});
            skLineSegment(sketch, "E35.0.3.4", {"start": v(29.7, -55.44) * mm, "end": v(493.6, -55.44) * mm});
            skArc(sketch, "E35.0.3.5", {"start": v(493.6, -55.44) * mm, "mid": v(494.5, -51.44) * mm, "end": v(493.6, -47.44) * mm});
            skLineSegment(sketch, "E35.direction1", {"start": v(-8.5, -4) * mm, "end": v(16.5, -4) * mm, "construction": true});
            skLineSegment(sketch, "E35.direction2", {"start": v(-8.5, -4) * mm, "end": v(1.4, -21.15) * mm, "construction": true});
            skSolve(sketch);
        }
        {
            var Q0;
            Q0=qSketchRegion(id+"F5",true);
            var Q1;
            Q1=makeQuery(id+"F4.opExtrude","CAP_FACE",FACE,{"disambiguationData":[OSD([sQuery(id+"F3.wireOp",EDGE,"E25.0"),sQuery(id+"F3.wireOp",EDGE,"E25.1"),sQuery(id+"F3.wireOp",EDGE,"E25.2"),sQuery(id+"F3.wireOp",EDGE,"E25.3"),sQuery(id+"F3.wireOp",EDGE,"E25.4"),sQuery(id+"F3.wireOp",EDGE,"E25.5"),sQuery(id+"F3.wireOp",EDGE,"E25.6"),sQuery(id+"F3.wireOp",EDGE,"E25.7"),sQuery(id+"F3.wireOp",EDGE,"E25.8"),sQuery(id+"F3.wireOp",EDGE,"E25.9"),sQuery(id+"F3.wireOp",EDGE,"E25.10"),sQuery(id+"F3.wireOp",EDGE,"E25.11")])],"isStart":false});
            extrude(context, id + "F6", {"entities" : qUnion([Q0]), "operationType" : NewBodyOperationType.REMOVE, "endBound" : BoundingType.UP_TO_SURFACE, "endBoundEntityFace" : qUnion([Q1]), "depth" : 25 * mm});
        }
        {
            var Q0;
            Q0=makeQuery(id+"F1.opExtrude","CAP_FACE",FACE,{"disambiguationData":[OSD([sQuery(id+"F0.wireOp",EDGE,"E0"),sQuery(id+"F0.wireOp",EDGE,"E1.0.1.0"),sQuery(id+"F0.wireOp",EDGE,"E1.0.2.0"),sQuery(id+"F0.wireOp",EDGE,"E1.0.3.0"),sQuery(id+"F0.wireOp",EDGE,"E1.1.0.0"),sQuery(id+"F0.wireOp",EDGE,"E1.1.1.0"),sQuery(id+"F0.wireOp",EDGE,"E1.1.2.0"),sQuery(id+"F0.wireOp",EDGE,"E1.1.3.0"),sQuery(id+"F0.wireOp",EDGE,"E1.2.0.0"),sQuery(id+"F0.wireOp",EDGE,"E1.2.1.0"),sQuery(id+"F0.wireOp",EDGE,"E1.2.2.0"),sQuery(id+"F0.wireOp",EDGE,"E1.2.3.0"),sQuery(id+"F0.wireOp",EDGE,"E1.3.0.0"),sQuery(id+"F0.wireOp",EDGE,"E1.3.1.0"),sQuery(id+"F0.wireOp",EDGE,"E1.3.2.0"),sQuery(id+"F0.wireOp",EDGE,"E1.3.3.0"),sQuery(id+"F0.wireOp",EDGE,"E1.4.0.0"),sQuery(id+"F0.wireOp",EDGE,"E1.4.1.0"),sQuery(id+"F0.wireOp",EDGE,"E1.4.2.0"),sQuery(id+"F0.wireOp",EDGE,"E1.4.3.0"),sQuery(id+"F0.wireOp",EDGE,"E1.5.0.0"),sQuery(id+"F0.wireOp",EDGE,"E1.5.1.0"),sQuery(id+"F0.wireOp",EDGE,"E1.5.2.0"),sQuery(id+"F0.wireOp",EDGE,"E1.5.3.0"),sQuery(id+"F0.wireOp",EDGE,"E1.6.0.0"),sQuery(id+"F0.wireOp",EDGE,"E1.6.1.0"),sQuery(id+"F0.wireOp",EDGE,"E1.6.2.0"),sQuery(id+"F0.wireOp",EDGE,"E1.6.3.0"),sQuery(id+"F0.wireOp",EDGE,"E1.7.0.0"),sQuery(id+"F0.wireOp",EDGE,"E1.7.1.0"),sQuery(id+"F0.wireOp",EDGE,"E1.7.2.0"),sQuery(id+"F0.wireOp",EDGE,"E1.7.3.0"),sQuery(id+"F0.wireOp",EDGE,"E1.8.0.0"),sQuery(id+"F0.wireOp",EDGE,"E1.8.1.0"),sQuery(id+"F0.wireOp",EDGE,"E1.8.2.0"),sQuery(id+"F0.wireOp",EDGE,"E1.8.3.0"),sQuery(id+"F0.wireOp",EDGE,"E1.9.0.0"),sQuery(id+"F0.wireOp",EDGE,"E1.9.1.0"),sQuery(id+"F0.wireOp",EDGE,"E1.9.2.0"),sQuery(id+"F0.wireOp",EDGE,"E1.9.3.0"),sQuery(id+"F0.wireOp",EDGE,"E2.0.10.0"),sQuery(id+"F0.wireOp",EDGE,"E2.0.10.1"),sQuery(id+"F0.wireOp",EDGE,"E2.0.10.2"),sQuery(id+"F0.wireOp",EDGE,"E2.0.10.3"),sQuery(id+"F0.wireOp",EDGE,"E2.0.11.0"),sQuery(id+"F0.wireOp",EDGE,"E2.0.11.1"),sQuery(id+"F0.wireOp",EDGE,"E2.0.11.2"),sQuery(id+"F0.wireOp",EDGE,"E2.0.11.3"),sQuery(id+"F0.wireOp",EDGE,"E2.0.12.0"),sQuery(id+"F0.wireOp",EDGE,"E2.0.12.1"),sQuery(id+"F0.wireOp",EDGE,"E2.0.12.2"),sQuery(id+"F0.wireOp",EDGE,"E2.0.12.3"),sQuery(id+"F0.wireOp",EDGE,"E2.0.13.0"),sQuery(id+"F0.wireOp",EDGE,"E2.0.13.1"),sQuery(id+"F0.wireOp",EDGE,"E2.0.13.2"),sQuery(id+"F0.wireOp",EDGE,"E2.0.13.3"),sQuery(id+"F0.wireOp",EDGE,"E2.0.14.0"),sQuery(id+"F0.wireOp",EDGE,"E2.0.14.1"),sQuery(id+"F0.wireOp",EDGE,"E2.0.14.2"),sQuery(id+"F0.wireOp",EDGE,"E2.0.14.3"),sQuery(id+"F0.wireOp",EDGE,"E2.0.15.0"),sQuery(id+"F0.wireOp",EDGE,"E2.0.15.1"),sQuery(id+"F0.wireOp",EDGE,"E2.0.15.2"),sQuery(id+"F0.wireOp",EDGE,"E2.0.15.3"),sQuery(id+"F0.wireOp",EDGE,"E2.0.16.0"),sQuery(id+"F0.wireOp",EDGE,"E2.0.16.1"),sQuery(id+"F0.wireOp",EDGE,"E2.0.16.2"),sQuery(id+"F0.wireOp",EDGE,"E2.0.16.3"),sQuery(id+"F0.wireOp",EDGE,"E2.0.17.0"),sQuery(id+"F0.wireOp",EDGE,"E2.0.17.1"),sQuery(id+"F0.wireOp",EDGE,"E2.0.17.2"),sQuery(id+"F0.wireOp",EDGE,"E2.0.17.3"),sQuery(id+"F0.wireOp",EDGE,"E2.0.18.0"),sQuery(id+"F0.wireOp",EDGE,"E2.0.18.1"),sQuery(id+"F0.wireOp",EDGE,"E2.0.18.2"),sQuery(id+"F0.wireOp",EDGE,"E2.0.18.3"),sQuery(id+"F0.wireOp",EDGE,"E2.0.19.0"),sQuery(id+"F0.wireOp",EDGE,"E2.0.19.1"),sQuery(id+"F0.wireOp",EDGE,"E2.0.19.2"),sQuery(id+"F0.wireOp",EDGE,"E2.0.19.3"),sQuery(id+"F0.wireOp",EDGE,"E3.0.20.0"),sQuery(id+"F0.wireOp",EDGE,"E3.0.20.1"),sQuery(id+"F0.wireOp",EDGE,"E3.0.20.2"),sQuery(id+"F0.wireOp",EDGE,"E3.0.20.3"),sQuery(id+"F0.wireOp",EDGE,"E3.0.21.0"),sQuery(id+"F0.wireOp",EDGE,"E3.0.21.1"),sQuery(id+"F0.wireOp",EDGE,"E3.0.21.2"),sQuery(id+"F0.wireOp",EDGE,"E3.0.21.3"),sQuery(id+"F0.wireOp",EDGE,"E3.0.22.0"),sQuery(id+"F0.wireOp",EDGE,"E3.0.22.1"),sQuery(id+"F0.wireOp",EDGE,"E3.0.22.2"),sQuery(id+"F0.wireOp",EDGE,"E3.0.22.3"),sQuery(id+"F0.wireOp",EDGE,"E3.0.23.0"),sQuery(id+"F0.wireOp",EDGE,"E3.0.23.1"),sQuery(id+"F0.wireOp",EDGE,"E3.0.23.2"),sQuery(id+"F0.wireOp",EDGE,"E3.0.23.3"),sQuery(id+"F0.wireOp",EDGE,"E8"),sQuery(id+"F0.wireOp",EDGE,"E9.0.1.0"),sQuery(id+"F0.wireOp",EDGE,"E9.0.2.0"),sQuery(id+"F0.wireOp",EDGE,"E9.0.3.0"),sQuery(id+"F0.wireOp",EDGE,"E9.1.0.0"),sQuery(id+"F0.wireOp",EDGE,"E9.1.1.0"),sQuery(id+"F0.wireOp",EDGE,"E9.1.2.0"),sQuery(id+"F0.wireOp",EDGE,"E9.1.3.0"),sQuery(id+"F0.wireOp",EDGE,"E9.2.0.0"),sQuery(id+"F0.wireOp",EDGE,"E9.2.1.0"),sQuery(id+"F0.wireOp",EDGE,"E9.2.2.0"),sQuery(id+"F0.wireOp",EDGE,"E9.2.3.0"),sQuery(id+"F0.wireOp",EDGE,"E9.3.0.0"),sQuery(id+"F0.wireOp",EDGE,"E9.3.1.0"),sQuery(id+"F0.wireOp",EDGE,"E9.3.2.0"),sQuery(id+"F0.wireOp",EDGE,"E9.3.3.0"),sQuery(id+"F0.wireOp",EDGE,"E9.4.0.0"),sQuery(id+"F0.wireOp",EDGE,"E9.4.1.0"),sQuery(id+"F0.wireOp",EDGE,"E9.4.2.0"),sQuery(id+"F0.wireOp",EDGE,"E9.4.3.0"),sQuery(id+"F0.wireOp",EDGE,"E9.5.0.0"),sQuery(id+"F0.wireOp",EDGE,"E9.5.1.0"),sQuery(id+"F0.wireOp",EDGE,"E9.5.2.0"),sQuery(id+"F0.wireOp",EDGE,"E9.5.3.0"),sQuery(id+"F0.wireOp",EDGE,"E9.6.0.0"),sQuery(id+"F0.wireOp",EDGE,"E9.6.1.0"),sQuery(id+"F0.wireOp",EDGE,"E9.6.2.0"),sQuery(id+"F0.wireOp",EDGE,"E9.6.3.0"),sQuery(id+"F0.wireOp",EDGE,"E9.7.0.0"),sQuery(id+"F0.wireOp",EDGE,"E9.7.1.0"),sQuery(id+"F0.wireOp",EDGE,"E9.7.2.0"),sQuery(id+"F0.wireOp",EDGE,"E9.7.3.0"),sQuery(id+"F0.wireOp",EDGE,"E9.8.0.0"),sQuery(id+"F0.wireOp",EDGE,"E9.8.1.0"),sQuery(id+"F0.wireOp",EDGE,"E9.8.2.0"),sQuery(id+"F0.wireOp",EDGE,"E9.8.3.0"),sQuery(id+"F0.wireOp",EDGE,"E9.9.0.0"),sQuery(id+"F0.wireOp",EDGE,"E9.9.1.0"),sQuery(id+"F0.wireOp",EDGE,"E9.9.2.0"),sQuery(id+"F0.wireOp",EDGE,"E9.9.3.0"),sQuery(id+"F0.wireOp",EDGE,"E9.10.0.0"),sQuery(id+"F0.wireOp",EDGE,"E9.10.1.0"),sQuery(id+"F0.wireOp",EDGE,"E9.10.2.0"),sQuery(id+"F0.wireOp",EDGE,"E9.10.3.0"),sQuery(id+"F0.wireOp",EDGE,"E9.11.0.0"),sQuery(id+"F0.wireOp",EDGE,"E9.11.1.0"),sQuery(id+"F0.wireOp",EDGE,"E9.11.2.0"),sQuery(id+"F0.wireOp",EDGE,"E9.11.3.0"),sQuery(id+"F0.wireOp",EDGE,"E9.12.0.0"),sQuery(id+"F0.wireOp",EDGE,"E9.12.1.0"),sQuery(id+"F0.wireOp",EDGE,"E9.12.2.0"),sQuery(id+"F0.wireOp",EDGE,"E9.12.3.0"),sQuery(id+"F0.wireOp",EDGE,"E9.13.0.0"),sQuery(id+"F0.wireOp",EDGE,"E9.13.1.0"),sQuery(id+"F0.wireOp",EDGE,"E9.13.2.0"),sQuery(id+"F0.wireOp",EDGE,"E9.13.3.0"),sQuery(id+"F0.wireOp",EDGE,"E9.14.0.0"),sQuery(id+"F0.wireOp",EDGE,"E9.14.1.0"),sQuery(id+"F0.wireOp",EDGE,"E9.14.2.0"),sQuery(id+"F0.wireOp",EDGE,"E9.14.3.0"),sQuery(id+"F0.wireOp",EDGE,"E9.15.0.0"),sQuery(id+"F0.wireOp",EDGE,"E9.15.1.0"),sQuery(id+"F0.wireOp",EDGE,"E9.15.2.0"),sQuery(id+"F0.wireOp",EDGE,"E9.15.3.0"),sQuery(id+"F0.wireOp",EDGE,"E10.0"),sQuery(id+"F0.wireOp",EDGE,"E11.0"),sQuery(id+"F0.wireOp",EDGE,"E12.0"),sQuery(id+"F0.wireOp",EDGE,"E13.0"),sQuery(id+"F0.wireOp",EDGE,"E14.0"),sQuery(id+"F0.wireOp",EDGE,"E16"),sQuery(id+"F0.wireOp",EDGE,"E17"),sQuery(id+"F0.wireOp",EDGE,"E18"),sQuery(id+"F0.wireOp",EDGE,"E19"),sQuery(id+"F0.wireOp",EDGE,"E20"),sQuery(id+"F0.wireOp",EDGE,"E22"),sQuery(id+"F0.wireOp",EDGE,"E23"),sQuery(id+"F0.wireOp",EDGE,"E24")])],"isStart":false});
            var sketch = newSketch(context, id + "F7", { "sketchPlane" : qUnion([Q0]) });
            skArc(sketch, "E36.0", {"start": v(189.5, -64.59) * mm, "mid": v(188.6, -68.59) * mm, "end": v(189.5, -72.59) * mm});
            skArc(sketch, "E36.1", {"start": v(219.2, -116.03) * mm, "mid": v(218.3, -120.03) * mm, "end": v(219.2, -124.03) * mm});
            skLineSegment(sketch, "E37", {"start": v(198, -68.59) * mm, "end": v(495, -68.59) * mm, "construction": true});
            skLineSegment(sketch, "E38", {"start": v(198, -68.59) * mm, "end": v(227.7, -120.03) * mm, "construction": true});
            skLineSegment(sketch, "E39.0.left", {"start": v(198, -64.59) * mm, "end": v(495, -64.59) * mm});
            skLineSegment(sketch, "E39.0.right", {"start": v(198, -72.59) * mm, "end": v(495, -72.59) * mm});
            skLineSegment(sketch, "E40", {"start": v(198, -64.59) * mm, "end": v(189.5, -64.59) * mm});
            skLineSegment(sketch, "E41", {"start": v(198, -72.59) * mm, "end": v(189.5, -72.59) * mm});
            skLineSegment(sketch, "E42", {"start": v(495, -64.59) * mm, "end": v(503.5, -64.59) * mm});
            skLineSegment(sketch, "E43", {"start": v(495, -72.59) * mm, "end": v(503.5, -72.59) * mm});
            skArc(sketch, "E44.trimOffspring", {"start": v(503.5, -72.59) * mm, "mid": v(504.4, -68.59) * mm, "end": v(503.5, -64.59) * mm});
            skArc(sketch, "E45.0.1.0", {"start": v(199.4, -81.74) * mm, "mid": v(198.5, -85.74) * mm, "end": v(199.4, -89.74) * mm});
            skLineSegment(sketch, "E45.0.1.1", {"start": v(207.9, -81.74) * mm, "end": v(504.9, -81.74) * mm});
            skLineSegment(sketch, "E45.0.1.2", {"start": v(207.9, -89.74) * mm, "end": v(504.9, -89.74) * mm});
            skLineSegment(sketch, "E45.0.1.3", {"start": v(207.9, -81.74) * mm, "end": v(199.4, -81.74) * mm});
            skLineSegment(sketch, "E45.0.1.4", {"start": v(207.9, -89.74) * mm, "end": v(199.4, -89.74) * mm});
            skLineSegment(sketch, "E45.0.1.5", {"start": v(504.9, -81.74) * mm, "end": v(513.4, -81.74) * mm});
            skLineSegment(sketch, "E45.0.1.6", {"start": v(504.9, -89.74) * mm, "end": v(513.4, -89.74) * mm});
            skArc(sketch, "E45.0.1.7", {"start": v(513.4, -89.74) * mm, "mid": v(514.3, -85.74) * mm, "end": v(513.4, -81.74) * mm});
            skArc(sketch, "E45.0.2.0", {"start": v(209.3, -98.88) * mm, "mid": v(208.4, -102.88) * mm, "end": v(209.3, -106.88) * mm});
            skLineSegment(sketch, "E45.0.2.1", {"start": v(217.8, -98.88) * mm, "end": v(514.8, -98.88) * mm});
            skLineSegment(sketch, "E45.0.2.2", {"start": v(217.8, -106.88) * mm, "end": v(514.8, -106.88) * mm});
            skLineSegment(sketch, "E45.0.2.3", {"start": v(217.8, -98.88) * mm, "end": v(209.3, -98.88) * mm});
            skLineSegment(sketch, "E45.0.2.4", {"start": v(217.8, -106.88) * mm, "end": v(209.3, -106.88) * mm});
            skLineSegment(sketch, "E45.0.2.5", {"start": v(514.8, -98.88) * mm, "end": v(523.3, -98.88) * mm});
            skLineSegment(sketch, "E45.0.2.6", {"start": v(514.8, -106.88) * mm, "end": v(523.3, -106.88) * mm});
            skArc(sketch, "E45.0.2.7", {"start": v(523.3, -106.88) * mm, "mid": v(524.2, -102.88) * mm, "end": v(523.3, -98.88) * mm});
            skLineSegment(sketch, "E45.0.3.1", {"start": v(227.7, -116.03) * mm, "end": v(524.7, -116.03) * mm});
            skLineSegment(sketch, "E45.0.3.2", {"start": v(227.7, -124.03) * mm, "end": v(524.7, -124.03) * mm});
            skLineSegment(sketch, "E45.0.3.3", {"start": v(227.7, -116.03) * mm, "end": v(219.2, -116.03) * mm});
            skLineSegment(sketch, "E45.0.3.4", {"start": v(227.7, -124.03) * mm, "end": v(219.2, -124.03) * mm});
            skLineSegment(sketch, "E45.0.3.5", {"start": v(524.7, -116.03) * mm, "end": v(533.2, -116.03) * mm});
            skLineSegment(sketch, "E45.0.3.6", {"start": v(524.7, -124.03) * mm, "end": v(533.2, -124.03) * mm});
            skArc(sketch, "E45.0.3.7", {"start": v(533.2, -124.03) * mm, "mid": v(534.1, -120.03) * mm, "end": v(533.2, -116.03) * mm});
            skLineSegment(sketch, "E45.direction1", {"start": v(189.5, -72.59) * mm, "end": v(214.5, -72.59) * mm, "construction": true});
            skLineSegment(sketch, "E45.direction2", {"start": v(189.5, -72.59) * mm, "end": v(199.4, -89.74) * mm, "construction": true});
            skSolve(sketch);
        }
        {
            var Q0;
            Q0=qSketchRegion(id+"F7",true);
            var Q1;
            Q1=makeQuery(id+"F4.opExtrude","CAP_FACE",FACE,{"disambiguationData":[OSD([sQuery(id+"F3.wireOp",EDGE,"E25.0"),sQuery(id+"F3.wireOp",EDGE,"E25.1"),sQuery(id+"F3.wireOp",EDGE,"E25.2"),sQuery(id+"F3.wireOp",EDGE,"E25.3"),sQuery(id+"F3.wireOp",EDGE,"E25.4"),sQuery(id+"F3.wireOp",EDGE,"E25.5"),sQuery(id+"F3.wireOp",EDGE,"E25.6"),sQuery(id+"F3.wireOp",EDGE,"E25.7"),sQuery(id+"F3.wireOp",EDGE,"E25.8"),sQuery(id+"F3.wireOp",EDGE,"E25.9"),sQuery(id+"F3.wireOp",EDGE,"E25.10"),sQuery(id+"F3.wireOp",EDGE,"E25.11")])],"isStart":false});
            extrude(context, id + "F8", {"entities" : qUnion([Q0]), "operationType" : NewBodyOperationType.REMOVE, "endBound" : BoundingType.UP_TO_SURFACE, "endBoundEntityFace" : qUnion([Q1]), "depth" : 25 * mm});
        }
        {
            var Q0;
            Q0=makeQuery(id+"F1.opExtrude","CAP_FACE",FACE,{"disambiguationData":[OSD([sQuery(id+"F0.wireOp",EDGE,"E0"),sQuery(id+"F0.wireOp",EDGE,"E1.0.1.0"),sQuery(id+"F0.wireOp",EDGE,"E1.0.2.0"),sQuery(id+"F0.wireOp",EDGE,"E1.0.3.0"),sQuery(id+"F0.wireOp",EDGE,"E1.1.0.0"),sQuery(id+"F0.wireOp",EDGE,"E1.1.1.0"),sQuery(id+"F0.wireOp",EDGE,"E1.1.2.0"),sQuery(id+"F0.wireOp",EDGE,"E1.1.3.0"),sQuery(id+"F0.wireOp",EDGE,"E1.2.0.0"),sQuery(id+"F0.wireOp",EDGE,"E1.2.1.0"),sQuery(id+"F0.wireOp",EDGE,"E1.2.2.0"),sQuery(id+"F0.wireOp",EDGE,"E1.2.3.0"),sQuery(id+"F0.wireOp",EDGE,"E1.3.0.0"),sQuery(id+"F0.wireOp",EDGE,"E1.3.1.0"),sQuery(id+"F0.wireOp",EDGE,"E1.3.2.0"),sQuery(id+"F0.wireOp",EDGE,"E1.3.3.0"),sQuery(id+"F0.wireOp",EDGE,"E1.4.0.0"),sQuery(id+"F0.wireOp",EDGE,"E1.4.1.0"),sQuery(id+"F0.wireOp",EDGE,"E1.4.2.0"),sQuery(id+"F0.wireOp",EDGE,"E1.4.3.0"),sQuery(id+"F0.wireOp",EDGE,"E1.5.0.0"),sQuery(id+"F0.wireOp",EDGE,"E1.5.1.0"),sQuery(id+"F0.wireOp",EDGE,"E1.5.2.0"),sQuery(id+"F0.wireOp",EDGE,"E1.5.3.0"),sQuery(id+"F0.wireOp",EDGE,"E1.6.0.0"),sQuery(id+"F0.wireOp",EDGE,"E1.6.1.0"),sQuery(id+"F0.wireOp",EDGE,"E1.6.2.0"),sQuery(id+"F0.wireOp",EDGE,"E1.6.3.0"),sQuery(id+"F0.wireOp",EDGE,"E1.7.0.0"),sQuery(id+"F0.wireOp",EDGE,"E1.7.1.0"),sQuery(id+"F0.wireOp",EDGE,"E1.7.2.0"),sQuery(id+"F0.wireOp",EDGE,"E1.7.3.0"),sQuery(id+"F0.wireOp",EDGE,"E1.8.0.0"),sQuery(id+"F0.wireOp",EDGE,"E1.8.1.0"),sQuery(id+"F0.wireOp",EDGE,"E1.8.2.0"),sQuery(id+"F0.wireOp",EDGE,"E1.8.3.0"),sQuery(id+"F0.wireOp",EDGE,"E1.9.0.0"),sQuery(id+"F0.wireOp",EDGE,"E1.9.1.0"),sQuery(id+"F0.wireOp",EDGE,"E1.9.2.0"),sQuery(id+"F0.wireOp",EDGE,"E1.9.3.0"),sQuery(id+"F0.wireOp",EDGE,"E2.0.10.0"),sQuery(id+"F0.wireOp",EDGE,"E2.0.10.1"),sQuery(id+"F0.wireOp",EDGE,"E2.0.10.2"),sQuery(id+"F0.wireOp",EDGE,"E2.0.10.3"),sQuery(id+"F0.wireOp",EDGE,"E2.0.11.0"),sQuery(id+"F0.wireOp",EDGE,"E2.0.11.1"),sQuery(id+"F0.wireOp",EDGE,"E2.0.11.2"),sQuery(id+"F0.wireOp",EDGE,"E2.0.11.3"),sQuery(id+"F0.wireOp",EDGE,"E2.0.12.0"),sQuery(id+"F0.wireOp",EDGE,"E2.0.12.1"),sQuery(id+"F0.wireOp",EDGE,"E2.0.12.2"),sQuery(id+"F0.wireOp",EDGE,"E2.0.12.3"),sQuery(id+"F0.wireOp",EDGE,"E2.0.13.0"),sQuery(id+"F0.wireOp",EDGE,"E2.0.13.1"),sQuery(id+"F0.wireOp",EDGE,"E2.0.13.2"),sQuery(id+"F0.wireOp",EDGE,"E2.0.13.3"),sQuery(id+"F0.wireOp",EDGE,"E2.0.14.0"),sQuery(id+"F0.wireOp",EDGE,"E2.0.14.1"),sQuery(id+"F0.wireOp",EDGE,"E2.0.14.2"),sQuery(id+"F0.wireOp",EDGE,"E2.0.14.3"),sQuery(id+"F0.wireOp",EDGE,"E2.0.15.0"),sQuery(id+"F0.wireOp",EDGE,"E2.0.15.1"),sQuery(id+"F0.wireOp",EDGE,"E2.0.15.2"),sQuery(id+"F0.wireOp",EDGE,"E2.0.15.3"),sQuery(id+"F0.wireOp",EDGE,"E2.0.16.0"),sQuery(id+"F0.wireOp",EDGE,"E2.0.16.1"),sQuery(id+"F0.wireOp",EDGE,"E2.0.16.2"),sQuery(id+"F0.wireOp",EDGE,"E2.0.16.3"),sQuery(id+"F0.wireOp",EDGE,"E2.0.17.0"),sQuery(id+"F0.wireOp",EDGE,"E2.0.17.1"),sQuery(id+"F0.wireOp",EDGE,"E2.0.17.2"),sQuery(id+"F0.wireOp",EDGE,"E2.0.17.3"),sQuery(id+"F0.wireOp",EDGE,"E2.0.18.0"),sQuery(id+"F0.wireOp",EDGE,"E2.0.18.1"),sQuery(id+"F0.wireOp",EDGE,"E2.0.18.2"),sQuery(id+"F0.wireOp",EDGE,"E2.0.18.3"),sQuery(id+"F0.wireOp",EDGE,"E2.0.19.0"),sQuery(id+"F0.wireOp",EDGE,"E2.0.19.1"),sQuery(id+"F0.wireOp",EDGE,"E2.0.19.2"),sQuery(id+"F0.wireOp",EDGE,"E2.0.19.3"),sQuery(id+"F0.wireOp",EDGE,"E3.0.20.0"),sQuery(id+"F0.wireOp",EDGE,"E3.0.20.1"),sQuery(id+"F0.wireOp",EDGE,"E3.0.20.2"),sQuery(id+"F0.wireOp",EDGE,"E3.0.20.3"),sQuery(id+"F0.wireOp",EDGE,"E3.0.21.0"),sQuery(id+"F0.wireOp",EDGE,"E3.0.21.1"),sQuery(id+"F0.wireOp",EDGE,"E3.0.21.2"),sQuery(id+"F0.wireOp",EDGE,"E3.0.21.3"),sQuery(id+"F0.wireOp",EDGE,"E3.0.22.0"),sQuery(id+"F0.wireOp",EDGE,"E3.0.22.1"),sQuery(id+"F0.wireOp",EDGE,"E3.0.22.2"),sQuery(id+"F0.wireOp",EDGE,"E3.0.22.3"),sQuery(id+"F0.wireOp",EDGE,"E3.0.23.0"),sQuery(id+"F0.wireOp",EDGE,"E3.0.23.1"),sQuery(id+"F0.wireOp",EDGE,"E3.0.23.2"),sQuery(id+"F0.wireOp",EDGE,"E3.0.23.3"),sQuery(id+"F0.wireOp",EDGE,"E8"),sQuery(id+"F0.wireOp",EDGE,"E9.0.1.0"),sQuery(id+"F0.wireOp",EDGE,"E9.0.2.0"),sQuery(id+"F0.wireOp",EDGE,"E9.0.3.0"),sQuery(id+"F0.wireOp",EDGE,"E9.1.0.0"),sQuery(id+"F0.wireOp",EDGE,"E9.1.1.0"),sQuery(id+"F0.wireOp",EDGE,"E9.1.2.0"),sQuery(id+"F0.wireOp",EDGE,"E9.1.3.0"),sQuery(id+"F0.wireOp",EDGE,"E9.2.0.0"),sQuery(id+"F0.wireOp",EDGE,"E9.2.1.0"),sQuery(id+"F0.wireOp",EDGE,"E9.2.2.0"),sQuery(id+"F0.wireOp",EDGE,"E9.2.3.0"),sQuery(id+"F0.wireOp",EDGE,"E9.3.0.0"),sQuery(id+"F0.wireOp",EDGE,"E9.3.1.0"),sQuery(id+"F0.wireOp",EDGE,"E9.3.2.0"),sQuery(id+"F0.wireOp",EDGE,"E9.3.3.0"),sQuery(id+"F0.wireOp",EDGE,"E9.4.0.0"),sQuery(id+"F0.wireOp",EDGE,"E9.4.1.0"),sQuery(id+"F0.wireOp",EDGE,"E9.4.2.0"),sQuery(id+"F0.wireOp",EDGE,"E9.4.3.0"),sQuery(id+"F0.wireOp",EDGE,"E9.5.0.0"),sQuery(id+"F0.wireOp",EDGE,"E9.5.1.0"),sQuery(id+"F0.wireOp",EDGE,"E9.5.2.0"),sQuery(id+"F0.wireOp",EDGE,"E9.5.3.0"),sQuery(id+"F0.wireOp",EDGE,"E9.6.0.0"),sQuery(id+"F0.wireOp",EDGE,"E9.6.1.0"),sQuery(id+"F0.wireOp",EDGE,"E9.6.2.0"),sQuery(id+"F0.wireOp",EDGE,"E9.6.3.0"),sQuery(id+"F0.wireOp",EDGE,"E9.7.0.0"),sQuery(id+"F0.wireOp",EDGE,"E9.7.1.0"),sQuery(id+"F0.wireOp",EDGE,"E9.7.2.0"),sQuery(id+"F0.wireOp",EDGE,"E9.7.3.0"),sQuery(id+"F0.wireOp",EDGE,"E9.8.0.0"),sQuery(id+"F0.wireOp",EDGE,"E9.8.1.0"),sQuery(id+"F0.wireOp",EDGE,"E9.8.2.0"),sQuery(id+"F0.wireOp",EDGE,"E9.8.3.0"),sQuery(id+"F0.wireOp",EDGE,"E9.9.0.0"),sQuery(id+"F0.wireOp",EDGE,"E9.9.1.0"),sQuery(id+"F0.wireOp",EDGE,"E9.9.2.0"),sQuery(id+"F0.wireOp",EDGE,"E9.9.3.0"),sQuery(id+"F0.wireOp",EDGE,"E9.10.0.0"),sQuery(id+"F0.wireOp",EDGE,"E9.10.1.0"),sQuery(id+"F0.wireOp",EDGE,"E9.10.2.0"),sQuery(id+"F0.wireOp",EDGE,"E9.10.3.0"),sQuery(id+"F0.wireOp",EDGE,"E9.11.0.0"),sQuery(id+"F0.wireOp",EDGE,"E9.11.1.0"),sQuery(id+"F0.wireOp",EDGE,"E9.11.2.0"),sQuery(id+"F0.wireOp",EDGE,"E9.11.3.0"),sQuery(id+"F0.wireOp",EDGE,"E9.12.0.0"),sQuery(id+"F0.wireOp",EDGE,"E9.12.1.0"),sQuery(id+"F0.wireOp",EDGE,"E9.12.2.0"),sQuery(id+"F0.wireOp",EDGE,"E9.12.3.0"),sQuery(id+"F0.wireOp",EDGE,"E9.13.0.0"),sQuery(id+"F0.wireOp",EDGE,"E9.13.1.0"),sQuery(id+"F0.wireOp",EDGE,"E9.13.2.0"),sQuery(id+"F0.wireOp",EDGE,"E9.13.3.0"),sQuery(id+"F0.wireOp",EDGE,"E9.14.0.0"),sQuery(id+"F0.wireOp",EDGE,"E9.14.1.0"),sQuery(id+"F0.wireOp",EDGE,"E9.14.2.0"),sQuery(id+"F0.wireOp",EDGE,"E9.14.3.0"),sQuery(id+"F0.wireOp",EDGE,"E9.15.0.0"),sQuery(id+"F0.wireOp",EDGE,"E9.15.1.0"),sQuery(id+"F0.wireOp",EDGE,"E9.15.2.0"),sQuery(id+"F0.wireOp",EDGE,"E9.15.3.0"),sQuery(id+"F0.wireOp",EDGE,"E10.0"),sQuery(id+"F0.wireOp",EDGE,"E11.0"),sQuery(id+"F0.wireOp",EDGE,"E12.0"),sQuery(id+"F0.wireOp",EDGE,"E13.0"),sQuery(id+"F0.wireOp",EDGE,"E14.0"),sQuery(id+"F0.wireOp",EDGE,"E16"),sQuery(id+"F0.wireOp",EDGE,"E17"),sQuery(id+"F0.wireOp",EDGE,"E18"),sQuery(id+"F0.wireOp",EDGE,"E19"),sQuery(id+"F0.wireOp",EDGE,"E20"),sQuery(id+"F0.wireOp",EDGE,"E22"),sQuery(id+"F0.wireOp",EDGE,"E23"),sQuery(id+"F0.wireOp",EDGE,"E24")])],"isStart":false});
            var sketch = newSketch(context, id + "F9", { "sketchPlane" : qUnion([Q0]) });
            skArc(sketch, "E46.0", {"start": v(-0.79, 9.37) * mm, "mid": v(-4.7, 8.14) * mm, "end": v(-7.72, 5.37) * mm});
            skArc(sketch, "E46.1", {"start": v(30.49, -60.8) * mm, "mid": v(34.4, -59.58) * mm, "end": v(37.42, -56.8) * mm});
            skLineSegment(sketch, "E47", {"start": v(0, 0) * mm, "end": v(29.7, -51.44) * mm, "construction": true});
            skLineSegment(sketch, "E48.0.left", {"start": v(3.46, 2) * mm, "end": v(33.16, -49.44) * mm});
            skLineSegment(sketch, "E48.0.right", {"start": v(-3.46, -2) * mm, "end": v(26.24, -53.44) * mm});
            skLineSegment(sketch, "E49", {"start": v(3.46, 2) * mm, "end": v(-0.79, 9.37) * mm});
            skLineSegment(sketch, "E50", {"start": v(-3.46, -2) * mm, "end": v(-7.72, 5.37) * mm});
            skLineSegment(sketch, "E51", {"start": v(26.24, -53.44) * mm, "end": v(30.49, -60.8) * mm});
            skLineSegment(sketch, "E52", {"start": v(33.16, -49.44) * mm, "end": v(37.42, -56.8) * mm});
            skArc(sketch, "E53.1.0.0", {"start": v(19.01, 9.37) * mm, "mid": v(15.1, 8.14) * mm, "end": v(12.08, 5.37) * mm});
            skLineSegment(sketch, "E53.1.0.1", {"start": v(16.34, -2) * mm, "end": v(12.08, 5.37) * mm});
            skLineSegment(sketch, "E53.1.0.2", {"start": v(23.26, 2) * mm, "end": v(19.01, 9.37) * mm});
            skLineSegment(sketch, "E53.1.0.3", {"start": v(23.26, 2) * mm, "end": v(52.96, -49.44) * mm});
            skLineSegment(sketch, "E53.1.0.4", {"start": v(16.34, -2) * mm, "end": v(46.04, -53.44) * mm});
            skLineSegment(sketch, "E53.1.0.5", {"start": v(46.04, -53.44) * mm, "end": v(50.29, -60.8) * mm});
            skLineSegment(sketch, "E53.1.0.6", {"start": v(52.96, -49.44) * mm, "end": v(57.22, -56.8) * mm});
            skArc(sketch, "E53.1.0.7", {"start": v(50.29, -60.8) * mm, "mid": v(54.2, -59.58) * mm, "end": v(57.22, -56.8) * mm});
            skArc(sketch, "E53.2.0.0", {"start": v(38.81, 9.37) * mm, "mid": v(34.9, 8.14) * mm, "end": v(31.88, 5.37) * mm});
            skLineSegment(sketch, "E53.2.0.1", {"start": v(36.14, -2) * mm, "end": v(31.88, 5.37) * mm});
            skLineSegment(sketch, "E53.2.0.2", {"start": v(43.06, 2) * mm, "end": v(38.81, 9.37) * mm});
            skLineSegment(sketch, "E53.2.0.3", {"start": v(43.06, 2) * mm, "end": v(72.76, -49.44) * mm});
            skLineSegment(sketch, "E53.2.0.4", {"start": v(36.14, -2) * mm, "end": v(65.84, -53.44) * mm});
            skLineSegment(sketch, "E53.2.0.5", {"start": v(65.84, -53.44) * mm, "end": v(70.09, -60.8) * mm});
            skLineSegment(sketch, "E53.2.0.6", {"start": v(72.76, -49.44) * mm, "end": v(77.02, -56.8) * mm});
            skArc(sketch, "E53.2.0.7", {"start": v(70.09, -60.8) * mm, "mid": v(74, -59.58) * mm, "end": v(77.02, -56.8) * mm});
            skArc(sketch, "E53.3.0.0", {"start": v(58.61, 9.37) * mm, "mid": v(54.7, 8.14) * mm, "end": v(51.68, 5.37) * mm});
            skLineSegment(sketch, "E53.3.0.1", {"start": v(55.94, -2) * mm, "end": v(51.68, 5.37) * mm});
            skLineSegment(sketch, "E53.3.0.2", {"start": v(62.86, 2) * mm, "end": v(58.61, 9.37) * mm});
            skLineSegment(sketch, "E53.3.0.3", {"start": v(62.86, 2) * mm, "end": v(92.56, -49.44) * mm});
            skLineSegment(sketch, "E53.3.0.4", {"start": v(55.94, -2) * mm, "end": v(85.64, -53.44) * mm});
            skLineSegment(sketch, "E53.3.0.5", {"start": v(85.64, -53.44) * mm, "end": v(89.89, -60.8) * mm});
            skLineSegment(sketch, "E53.3.0.6", {"start": v(92.56, -49.44) * mm, "end": v(96.82, -56.8) * mm});
            skArc(sketch, "E53.3.0.7", {"start": v(89.89, -60.8) * mm, "mid": v(93.8, -59.58) * mm, "end": v(96.82, -56.8) * mm});
            skArc(sketch, "E53.4.0.0", {"start": v(78.41, 9.37) * mm, "mid": v(74.5, 8.14) * mm, "end": v(71.48, 5.37) * mm});
            skLineSegment(sketch, "E53.4.0.1", {"start": v(75.74, -2) * mm, "end": v(71.48, 5.37) * mm});
            skLineSegment(sketch, "E53.4.0.2", {"start": v(82.66, 2) * mm, "end": v(78.41, 9.37) * mm});
            skLineSegment(sketch, "E53.4.0.3", {"start": v(82.66, 2) * mm, "end": v(112.36, -49.44) * mm});
            skLineSegment(sketch, "E53.4.0.4", {"start": v(75.74, -2) * mm, "end": v(105.44, -53.44) * mm});
            skLineSegment(sketch, "E53.4.0.5", {"start": v(105.44, -53.44) * mm, "end": v(109.69, -60.8) * mm});
            skLineSegment(sketch, "E53.4.0.6", {"start": v(112.36, -49.44) * mm, "end": v(116.62, -56.8) * mm});
            skArc(sketch, "E53.4.0.7", {"start": v(109.69, -60.8) * mm, "mid": v(113.6, -59.58) * mm, "end": v(116.62, -56.8) * mm});
            skArc(sketch, "E53.5.0.0", {"start": v(98.21, 9.37) * mm, "mid": v(94.3, 8.14) * mm, "end": v(91.28, 5.37) * mm});
            skLineSegment(sketch, "E53.5.0.1", {"start": v(95.54, -2) * mm, "end": v(91.28, 5.37) * mm});
            skLineSegment(sketch, "E53.5.0.2", {"start": v(102.46, 2) * mm, "end": v(98.21, 9.37) * mm});
            skLineSegment(sketch, "E53.5.0.3", {"start": v(102.46, 2) * mm, "end": v(132.16, -49.44) * mm});
            skLineSegment(sketch, "E53.5.0.4", {"start": v(95.54, -2) * mm, "end": v(125.24, -53.44) * mm});
            skLineSegment(sketch, "E53.5.0.5", {"start": v(125.24, -53.44) * mm, "end": v(129.49, -60.8) * mm});
            skLineSegment(sketch, "E53.5.0.6", {"start": v(132.16, -49.44) * mm, "end": v(136.42, -56.8) * mm});
            skArc(sketch, "E53.5.0.7", {"start": v(129.49, -60.8) * mm, "mid": v(133.4, -59.58) * mm, "end": v(136.42, -56.8) * mm});
            skArc(sketch, "E53.6.0.0", {"start": v(118.01, 9.37) * mm, "mid": v(114.1, 8.14) * mm, "end": v(111.08, 5.37) * mm});
            skLineSegment(sketch, "E53.6.0.1", {"start": v(115.34, -2) * mm, "end": v(111.08, 5.37) * mm});
            skLineSegment(sketch, "E53.6.0.2", {"start": v(122.26, 2) * mm, "end": v(118.01, 9.37) * mm});
            skLineSegment(sketch, "E53.6.0.3", {"start": v(122.26, 2) * mm, "end": v(151.96, -49.44) * mm});
            skLineSegment(sketch, "E53.6.0.4", {"start": v(115.34, -2) * mm, "end": v(145.04, -53.44) * mm});
            skLineSegment(sketch, "E53.6.0.5", {"start": v(145.04, -53.44) * mm, "end": v(149.29, -60.8) * mm});
            skLineSegment(sketch, "E53.6.0.6", {"start": v(151.96, -49.44) * mm, "end": v(156.22, -56.8) * mm});
            skArc(sketch, "E53.6.0.7", {"start": v(149.29, -60.8) * mm, "mid": v(153.2, -59.58) * mm, "end": v(156.22, -56.8) * mm});
            skArc(sketch, "E53.7.0.0", {"start": v(137.81, 9.37) * mm, "mid": v(133.9, 8.14) * mm, "end": v(130.88, 5.37) * mm});
            skLineSegment(sketch, "E53.7.0.1", {"start": v(135.14, -2) * mm, "end": v(130.88, 5.37) * mm});
            skLineSegment(sketch, "E53.7.0.2", {"start": v(142.06, 2) * mm, "end": v(137.81, 9.37) * mm});
            skLineSegment(sketch, "E53.7.0.3", {"start": v(142.06, 2) * mm, "end": v(171.76, -49.44) * mm});
            skLineSegment(sketch, "E53.7.0.4", {"start": v(135.14, -2) * mm, "end": v(164.84, -53.44) * mm});
            skLineSegment(sketch, "E53.7.0.5", {"start": v(164.84, -53.44) * mm, "end": v(169.09, -60.8) * mm});
            skLineSegment(sketch, "E53.7.0.6", {"start": v(171.76, -49.44) * mm, "end": v(176.02, -56.8) * mm});
            skArc(sketch, "E53.7.0.7", {"start": v(169.09, -60.8) * mm, "mid": v(173, -59.58) * mm, "end": v(176.02, -56.8) * mm});
            skLineSegment(sketch, "E53.direction1", {"start": v(-7.72, 5.37) * mm, "end": v(12.08, 5.37) * mm, "construction": true});
            skSolve(sketch);
        }
        {
            var Q0;
            Q0=qSketchRegion(id+"F9",true);
            var Q1;
            Q1=makeQuery(id+"F4.opExtrude","CAP_FACE",FACE,{"disambiguationData":[OSD([sQuery(id+"F3.wireOp",EDGE,"E25.0"),sQuery(id+"F3.wireOp",EDGE,"E25.1"),sQuery(id+"F3.wireOp",EDGE,"E25.2"),sQuery(id+"F3.wireOp",EDGE,"E25.3"),sQuery(id+"F3.wireOp",EDGE,"E25.4"),sQuery(id+"F3.wireOp",EDGE,"E25.5"),sQuery(id+"F3.wireOp",EDGE,"E25.6"),sQuery(id+"F3.wireOp",EDGE,"E25.7"),sQuery(id+"F3.wireOp",EDGE,"E25.8"),sQuery(id+"F3.wireOp",EDGE,"E25.9"),sQuery(id+"F3.wireOp",EDGE,"E25.10"),sQuery(id+"F3.wireOp",EDGE,"E25.11")])],"isStart":false});
            extrude(context, id + "F10", {"entities" : qUnion([Q0]), "operationType" : NewBodyOperationType.REMOVE, "endBound" : BoundingType.UP_TO_SURFACE, "endBoundEntityFace" : qUnion([Q1]), "depth" : 25 * mm});
        }
        {
            var Q0;
            Q0=makeQuery(id+"F1.opExtrude","CAP_FACE",FACE,{"disambiguationData":[OSD([sQuery(id+"F0.wireOp",EDGE,"E0"),sQuery(id+"F0.wireOp",EDGE,"E1.0.1.0"),sQuery(id+"F0.wireOp",EDGE,"E1.0.2.0"),sQuery(id+"F0.wireOp",EDGE,"E1.0.3.0"),sQuery(id+"F0.wireOp",EDGE,"E1.1.0.0"),sQuery(id+"F0.wireOp",EDGE,"E1.1.1.0"),sQuery(id+"F0.wireOp",EDGE,"E1.1.2.0"),sQuery(id+"F0.wireOp",EDGE,"E1.1.3.0"),sQuery(id+"F0.wireOp",EDGE,"E1.2.0.0"),sQuery(id+"F0.wireOp",EDGE,"E1.2.1.0"),sQuery(id+"F0.wireOp",EDGE,"E1.2.2.0"),sQuery(id+"F0.wireOp",EDGE,"E1.2.3.0"),sQuery(id+"F0.wireOp",EDGE,"E1.3.0.0"),sQuery(id+"F0.wireOp",EDGE,"E1.3.1.0"),sQuery(id+"F0.wireOp",EDGE,"E1.3.2.0"),sQuery(id+"F0.wireOp",EDGE,"E1.3.3.0"),sQuery(id+"F0.wireOp",EDGE,"E1.4.0.0"),sQuery(id+"F0.wireOp",EDGE,"E1.4.1.0"),sQuery(id+"F0.wireOp",EDGE,"E1.4.2.0"),sQuery(id+"F0.wireOp",EDGE,"E1.4.3.0"),sQuery(id+"F0.wireOp",EDGE,"E1.5.0.0"),sQuery(id+"F0.wireOp",EDGE,"E1.5.1.0"),sQuery(id+"F0.wireOp",EDGE,"E1.5.2.0"),sQuery(id+"F0.wireOp",EDGE,"E1.5.3.0"),sQuery(id+"F0.wireOp",EDGE,"E1.6.0.0"),sQuery(id+"F0.wireOp",EDGE,"E1.6.1.0"),sQuery(id+"F0.wireOp",EDGE,"E1.6.2.0"),sQuery(id+"F0.wireOp",EDGE,"E1.6.3.0"),sQuery(id+"F0.wireOp",EDGE,"E1.7.0.0"),sQuery(id+"F0.wireOp",EDGE,"E1.7.1.0"),sQuery(id+"F0.wireOp",EDGE,"E1.7.2.0"),sQuery(id+"F0.wireOp",EDGE,"E1.7.3.0"),sQuery(id+"F0.wireOp",EDGE,"E1.8.0.0"),sQuery(id+"F0.wireOp",EDGE,"E1.8.1.0"),sQuery(id+"F0.wireOp",EDGE,"E1.8.2.0"),sQuery(id+"F0.wireOp",EDGE,"E1.8.3.0"),sQuery(id+"F0.wireOp",EDGE,"E1.9.0.0"),sQuery(id+"F0.wireOp",EDGE,"E1.9.1.0"),sQuery(id+"F0.wireOp",EDGE,"E1.9.2.0"),sQuery(id+"F0.wireOp",EDGE,"E1.9.3.0"),sQuery(id+"F0.wireOp",EDGE,"E2.0.10.0"),sQuery(id+"F0.wireOp",EDGE,"E2.0.10.1"),sQuery(id+"F0.wireOp",EDGE,"E2.0.10.2"),sQuery(id+"F0.wireOp",EDGE,"E2.0.10.3"),sQuery(id+"F0.wireOp",EDGE,"E2.0.11.0"),sQuery(id+"F0.wireOp",EDGE,"E2.0.11.1"),sQuery(id+"F0.wireOp",EDGE,"E2.0.11.2"),sQuery(id+"F0.wireOp",EDGE,"E2.0.11.3"),sQuery(id+"F0.wireOp",EDGE,"E2.0.12.0"),sQuery(id+"F0.wireOp",EDGE,"E2.0.12.1"),sQuery(id+"F0.wireOp",EDGE,"E2.0.12.2"),sQuery(id+"F0.wireOp",EDGE,"E2.0.12.3"),sQuery(id+"F0.wireOp",EDGE,"E2.0.13.0"),sQuery(id+"F0.wireOp",EDGE,"E2.0.13.1"),sQuery(id+"F0.wireOp",EDGE,"E2.0.13.2"),sQuery(id+"F0.wireOp",EDGE,"E2.0.13.3"),sQuery(id+"F0.wireOp",EDGE,"E2.0.14.0"),sQuery(id+"F0.wireOp",EDGE,"E2.0.14.1"),sQuery(id+"F0.wireOp",EDGE,"E2.0.14.2"),sQuery(id+"F0.wireOp",EDGE,"E2.0.14.3"),sQuery(id+"F0.wireOp",EDGE,"E2.0.15.0"),sQuery(id+"F0.wireOp",EDGE,"E2.0.15.1"),sQuery(id+"F0.wireOp",EDGE,"E2.0.15.2"),sQuery(id+"F0.wireOp",EDGE,"E2.0.15.3"),sQuery(id+"F0.wireOp",EDGE,"E2.0.16.0"),sQuery(id+"F0.wireOp",EDGE,"E2.0.16.1"),sQuery(id+"F0.wireOp",EDGE,"E2.0.16.2"),sQuery(id+"F0.wireOp",EDGE,"E2.0.16.3"),sQuery(id+"F0.wireOp",EDGE,"E2.0.17.0"),sQuery(id+"F0.wireOp",EDGE,"E2.0.17.1"),sQuery(id+"F0.wireOp",EDGE,"E2.0.17.2"),sQuery(id+"F0.wireOp",EDGE,"E2.0.17.3"),sQuery(id+"F0.wireOp",EDGE,"E2.0.18.0"),sQuery(id+"F0.wireOp",EDGE,"E2.0.18.1"),sQuery(id+"F0.wireOp",EDGE,"E2.0.18.2"),sQuery(id+"F0.wireOp",EDGE,"E2.0.18.3"),sQuery(id+"F0.wireOp",EDGE,"E2.0.19.0"),sQuery(id+"F0.wireOp",EDGE,"E2.0.19.1"),sQuery(id+"F0.wireOp",EDGE,"E2.0.19.2"),sQuery(id+"F0.wireOp",EDGE,"E2.0.19.3"),sQuery(id+"F0.wireOp",EDGE,"E3.0.20.0"),sQuery(id+"F0.wireOp",EDGE,"E3.0.20.1"),sQuery(id+"F0.wireOp",EDGE,"E3.0.20.2"),sQuery(id+"F0.wireOp",EDGE,"E3.0.20.3"),sQuery(id+"F0.wireOp",EDGE,"E3.0.21.0"),sQuery(id+"F0.wireOp",EDGE,"E3.0.21.1"),sQuery(id+"F0.wireOp",EDGE,"E3.0.21.2"),sQuery(id+"F0.wireOp",EDGE,"E3.0.21.3"),sQuery(id+"F0.wireOp",EDGE,"E3.0.22.0"),sQuery(id+"F0.wireOp",EDGE,"E3.0.22.1"),sQuery(id+"F0.wireOp",EDGE,"E3.0.22.2"),sQuery(id+"F0.wireOp",EDGE,"E3.0.22.3"),sQuery(id+"F0.wireOp",EDGE,"E3.0.23.0"),sQuery(id+"F0.wireOp",EDGE,"E3.0.23.1"),sQuery(id+"F0.wireOp",EDGE,"E3.0.23.2"),sQuery(id+"F0.wireOp",EDGE,"E3.0.23.3"),sQuery(id+"F0.wireOp",EDGE,"E8"),sQuery(id+"F0.wireOp",EDGE,"E9.0.1.0"),sQuery(id+"F0.wireOp",EDGE,"E9.0.2.0"),sQuery(id+"F0.wireOp",EDGE,"E9.0.3.0"),sQuery(id+"F0.wireOp",EDGE,"E9.1.0.0"),sQuery(id+"F0.wireOp",EDGE,"E9.1.1.0"),sQuery(id+"F0.wireOp",EDGE,"E9.1.2.0"),sQuery(id+"F0.wireOp",EDGE,"E9.1.3.0"),sQuery(id+"F0.wireOp",EDGE,"E9.2.0.0"),sQuery(id+"F0.wireOp",EDGE,"E9.2.1.0"),sQuery(id+"F0.wireOp",EDGE,"E9.2.2.0"),sQuery(id+"F0.wireOp",EDGE,"E9.2.3.0"),sQuery(id+"F0.wireOp",EDGE,"E9.3.0.0"),sQuery(id+"F0.wireOp",EDGE,"E9.3.1.0"),sQuery(id+"F0.wireOp",EDGE,"E9.3.2.0"),sQuery(id+"F0.wireOp",EDGE,"E9.3.3.0"),sQuery(id+"F0.wireOp",EDGE,"E9.4.0.0"),sQuery(id+"F0.wireOp",EDGE,"E9.4.1.0"),sQuery(id+"F0.wireOp",EDGE,"E9.4.2.0"),sQuery(id+"F0.wireOp",EDGE,"E9.4.3.0"),sQuery(id+"F0.wireOp",EDGE,"E9.5.0.0"),sQuery(id+"F0.wireOp",EDGE,"E9.5.1.0"),sQuery(id+"F0.wireOp",EDGE,"E9.5.2.0"),sQuery(id+"F0.wireOp",EDGE,"E9.5.3.0"),sQuery(id+"F0.wireOp",EDGE,"E9.6.0.0"),sQuery(id+"F0.wireOp",EDGE,"E9.6.1.0"),sQuery(id+"F0.wireOp",EDGE,"E9.6.2.0"),sQuery(id+"F0.wireOp",EDGE,"E9.6.3.0"),sQuery(id+"F0.wireOp",EDGE,"E9.7.0.0"),sQuery(id+"F0.wireOp",EDGE,"E9.7.1.0"),sQuery(id+"F0.wireOp",EDGE,"E9.7.2.0"),sQuery(id+"F0.wireOp",EDGE,"E9.7.3.0"),sQuery(id+"F0.wireOp",EDGE,"E9.8.0.0"),sQuery(id+"F0.wireOp",EDGE,"E9.8.1.0"),sQuery(id+"F0.wireOp",EDGE,"E9.8.2.0"),sQuery(id+"F0.wireOp",EDGE,"E9.8.3.0"),sQuery(id+"F0.wireOp",EDGE,"E9.9.0.0"),sQuery(id+"F0.wireOp",EDGE,"E9.9.1.0"),sQuery(id+"F0.wireOp",EDGE,"E9.9.2.0"),sQuery(id+"F0.wireOp",EDGE,"E9.9.3.0"),sQuery(id+"F0.wireOp",EDGE,"E9.10.0.0"),sQuery(id+"F0.wireOp",EDGE,"E9.10.1.0"),sQuery(id+"F0.wireOp",EDGE,"E9.10.2.0"),sQuery(id+"F0.wireOp",EDGE,"E9.10.3.0"),sQuery(id+"F0.wireOp",EDGE,"E9.11.0.0"),sQuery(id+"F0.wireOp",EDGE,"E9.11.1.0"),sQuery(id+"F0.wireOp",EDGE,"E9.11.2.0"),sQuery(id+"F0.wireOp",EDGE,"E9.11.3.0"),sQuery(id+"F0.wireOp",EDGE,"E9.12.0.0"),sQuery(id+"F0.wireOp",EDGE,"E9.12.1.0"),sQuery(id+"F0.wireOp",EDGE,"E9.12.2.0"),sQuery(id+"F0.wireOp",EDGE,"E9.12.3.0"),sQuery(id+"F0.wireOp",EDGE,"E9.13.0.0"),sQuery(id+"F0.wireOp",EDGE,"E9.13.1.0"),sQuery(id+"F0.wireOp",EDGE,"E9.13.2.0"),sQuery(id+"F0.wireOp",EDGE,"E9.13.3.0"),sQuery(id+"F0.wireOp",EDGE,"E9.14.0.0"),sQuery(id+"F0.wireOp",EDGE,"E9.14.1.0"),sQuery(id+"F0.wireOp",EDGE,"E9.14.2.0"),sQuery(id+"F0.wireOp",EDGE,"E9.14.3.0"),sQuery(id+"F0.wireOp",EDGE,"E9.15.0.0"),sQuery(id+"F0.wireOp",EDGE,"E9.15.1.0"),sQuery(id+"F0.wireOp",EDGE,"E9.15.2.0"),sQuery(id+"F0.wireOp",EDGE,"E9.15.3.0"),sQuery(id+"F0.wireOp",EDGE,"E10.0"),sQuery(id+"F0.wireOp",EDGE,"E11.0"),sQuery(id+"F0.wireOp",EDGE,"E12.0"),sQuery(id+"F0.wireOp",EDGE,"E13.0"),sQuery(id+"F0.wireOp",EDGE,"E14.0"),sQuery(id+"F0.wireOp",EDGE,"E16"),sQuery(id+"F0.wireOp",EDGE,"E17"),sQuery(id+"F0.wireOp",EDGE,"E18"),sQuery(id+"F0.wireOp",EDGE,"E19"),sQuery(id+"F0.wireOp",EDGE,"E20"),sQuery(id+"F0.wireOp",EDGE,"E22"),sQuery(id+"F0.wireOp",EDGE,"E23"),sQuery(id+"F0.wireOp",EDGE,"E24")])],"isStart":false});
            var sketch = newSketch(context, id + "F11", { "sketchPlane" : qUnion([Q0]) });
            skArc(sketch, "E54.0", {"start": v(157.61, 9.37) * mm, "mid": v(153.7, 8.14) * mm, "end": v(150.68, 5.37) * mm});
            skArc(sketch, "E54.1", {"start": v(228.49, -129.4) * mm, "mid": v(232.4, -128.17) * mm, "end": v(235.42, -125.4) * mm});
            skLineSegment(sketch, "E55", {"start": v(158.4, 0) * mm, "end": v(227.7, -120.03) * mm, "construction": true});
            skLineSegment(sketch, "E56.0.left", {"start": v(161.86, 2) * mm, "end": v(231.16, -118.03) * mm});
            skLineSegment(sketch, "E56.0.right", {"start": v(154.94, -2) * mm, "end": v(224.24, -122.03) * mm});
            skLineSegment(sketch, "E57", {"start": v(161.86, 2) * mm, "end": v(157.61, 9.37) * mm});
            skLineSegment(sketch, "E58", {"start": v(154.94, -2) * mm, "end": v(150.68, 5.37) * mm});
            skLineSegment(sketch, "E59", {"start": v(224.24, -122.03) * mm, "end": v(228.49, -129.4) * mm});
            skLineSegment(sketch, "E60", {"start": v(231.16, -118.03) * mm, "end": v(235.42, -125.4) * mm});
            skArc(sketch, "E61.1.0.0", {"start": v(177.41, 9.37) * mm, "mid": v(173.5, 8.14) * mm, "end": v(170.48, 5.37) * mm});
            skLineSegment(sketch, "E61.1.0.1", {"start": v(174.74, -2) * mm, "end": v(170.48, 5.37) * mm});
            skLineSegment(sketch, "E61.1.0.2", {"start": v(181.66, 2) * mm, "end": v(177.41, 9.37) * mm});
            skLineSegment(sketch, "E61.1.0.3", {"start": v(181.66, 2) * mm, "end": v(250.96, -118.03) * mm});
            skLineSegment(sketch, "E61.1.0.4", {"start": v(174.74, -2) * mm, "end": v(244.04, -122.03) * mm});
            skLineSegment(sketch, "E61.1.0.5", {"start": v(244.04, -122.03) * mm, "end": v(248.29, -129.4) * mm});
            skLineSegment(sketch, "E61.1.0.6", {"start": v(250.96, -118.03) * mm, "end": v(255.22, -125.4) * mm});
            skArc(sketch, "E61.1.0.7", {"start": v(248.29, -129.4) * mm, "mid": v(252.2, -128.17) * mm, "end": v(255.22, -125.4) * mm});
            skArc(sketch, "E61.2.0.0", {"start": v(197.21, 9.37) * mm, "mid": v(193.3, 8.14) * mm, "end": v(190.28, 5.37) * mm});
            skLineSegment(sketch, "E61.2.0.1", {"start": v(194.54, -2) * mm, "end": v(190.28, 5.37) * mm});
            skLineSegment(sketch, "E61.2.0.2", {"start": v(201.46, 2) * mm, "end": v(197.21, 9.37) * mm});
            skLineSegment(sketch, "E61.2.0.3", {"start": v(201.46, 2) * mm, "end": v(270.76, -118.03) * mm});
            skLineSegment(sketch, "E61.2.0.4", {"start": v(194.54, -2) * mm, "end": v(263.84, -122.03) * mm});
            skLineSegment(sketch, "E61.2.0.5", {"start": v(263.84, -122.03) * mm, "end": v(268.09, -129.4) * mm});
            skLineSegment(sketch, "E61.2.0.6", {"start": v(270.76, -118.03) * mm, "end": v(275.02, -125.4) * mm});
            skArc(sketch, "E61.2.0.7", {"start": v(268.09, -129.4) * mm, "mid": v(272, -128.17) * mm, "end": v(275.02, -125.4) * mm});
            skArc(sketch, "E61.3.0.0", {"start": v(217.01, 9.37) * mm, "mid": v(213.1, 8.14) * mm, "end": v(210.08, 5.37) * mm});
            skLineSegment(sketch, "E61.3.0.1", {"start": v(214.34, -2) * mm, "end": v(210.08, 5.37) * mm});
            skLineSegment(sketch, "E61.3.0.2", {"start": v(221.26, 2) * mm, "end": v(217.01, 9.37) * mm});
            skLineSegment(sketch, "E61.3.0.3", {"start": v(221.26, 2) * mm, "end": v(290.56, -118.03) * mm});
            skLineSegment(sketch, "E61.3.0.4", {"start": v(214.34, -2) * mm, "end": v(283.64, -122.03) * mm});
            skLineSegment(sketch, "E61.3.0.5", {"start": v(283.64, -122.03) * mm, "end": v(287.89, -129.4) * mm});
            skLineSegment(sketch, "E61.3.0.6", {"start": v(290.56, -118.03) * mm, "end": v(294.82, -125.4) * mm});
            skArc(sketch, "E61.3.0.7", {"start": v(287.89, -129.4) * mm, "mid": v(291.8, -128.17) * mm, "end": v(294.82, -125.4) * mm});
            skArc(sketch, "E61.4.0.0", {"start": v(236.81, 9.37) * mm, "mid": v(232.9, 8.14) * mm, "end": v(229.88, 5.37) * mm});
            skLineSegment(sketch, "E61.4.0.1", {"start": v(234.14, -2) * mm, "end": v(229.88, 5.37) * mm});
            skLineSegment(sketch, "E61.4.0.2", {"start": v(241.06, 2) * mm, "end": v(236.81, 9.37) * mm});
            skLineSegment(sketch, "E61.4.0.3", {"start": v(241.06, 2) * mm, "end": v(310.36, -118.03) * mm});
            skLineSegment(sketch, "E61.4.0.4", {"start": v(234.14, -2) * mm, "end": v(303.44, -122.03) * mm});
            skLineSegment(sketch, "E61.4.0.5", {"start": v(303.44, -122.03) * mm, "end": v(307.69, -129.4) * mm});
            skLineSegment(sketch, "E61.4.0.6", {"start": v(310.36, -118.03) * mm, "end": v(314.62, -125.4) * mm});
            skArc(sketch, "E61.4.0.7", {"start": v(307.69, -129.4) * mm, "mid": v(311.6, -128.17) * mm, "end": v(314.62, -125.4) * mm});
            skArc(sketch, "E61.5.0.0", {"start": v(256.61, 9.37) * mm, "mid": v(252.7, 8.14) * mm, "end": v(249.68, 5.37) * mm});
            skLineSegment(sketch, "E61.5.0.1", {"start": v(253.94, -2) * mm, "end": v(249.68, 5.37) * mm});
            skLineSegment(sketch, "E61.5.0.2", {"start": v(260.86, 2) * mm, "end": v(256.61, 9.37) * mm});
            skLineSegment(sketch, "E61.5.0.3", {"start": v(260.86, 2) * mm, "end": v(330.16, -118.03) * mm});
            skLineSegment(sketch, "E61.5.0.4", {"start": v(253.94, -2) * mm, "end": v(323.24, -122.03) * mm});
            skLineSegment(sketch, "E61.5.0.5", {"start": v(323.24, -122.03) * mm, "end": v(327.49, -129.4) * mm});
            skLineSegment(sketch, "E61.5.0.6", {"start": v(330.16, -118.03) * mm, "end": v(334.42, -125.4) * mm});
            skArc(sketch, "E61.5.0.7", {"start": v(327.49, -129.4) * mm, "mid": v(331.4, -128.17) * mm, "end": v(334.42, -125.4) * mm});
            skArc(sketch, "E61.6.0.0", {"start": v(276.41, 9.37) * mm, "mid": v(272.5, 8.14) * mm, "end": v(269.48, 5.37) * mm});
            skLineSegment(sketch, "E61.6.0.1", {"start": v(273.74, -2) * mm, "end": v(269.48, 5.37) * mm});
            skLineSegment(sketch, "E61.6.0.2", {"start": v(280.66, 2) * mm, "end": v(276.41, 9.37) * mm});
            skLineSegment(sketch, "E61.6.0.3", {"start": v(280.66, 2) * mm, "end": v(349.96, -118.03) * mm});
            skLineSegment(sketch, "E61.6.0.4", {"start": v(273.74, -2) * mm, "end": v(343.04, -122.03) * mm});
            skLineSegment(sketch, "E61.6.0.5", {"start": v(343.04, -122.03) * mm, "end": v(347.29, -129.4) * mm});
            skLineSegment(sketch, "E61.6.0.6", {"start": v(349.96, -118.03) * mm, "end": v(354.22, -125.4) * mm});
            skArc(sketch, "E61.6.0.7", {"start": v(347.29, -129.4) * mm, "mid": v(351.2, -128.17) * mm, "end": v(354.22, -125.4) * mm});
            skArc(sketch, "E61.7.0.0", {"start": v(296.21, 9.37) * mm, "mid": v(292.3, 8.14) * mm, "end": v(289.28, 5.37) * mm});
            skLineSegment(sketch, "E61.7.0.1", {"start": v(293.54, -2) * mm, "end": v(289.28, 5.37) * mm});
            skLineSegment(sketch, "E61.7.0.2", {"start": v(300.46, 2) * mm, "end": v(296.21, 9.37) * mm});
            skLineSegment(sketch, "E61.7.0.3", {"start": v(300.46, 2) * mm, "end": v(369.76, -118.03) * mm});
            skLineSegment(sketch, "E61.7.0.4", {"start": v(293.54, -2) * mm, "end": v(362.84, -122.03) * mm});
            skLineSegment(sketch, "E61.7.0.5", {"start": v(362.84, -122.03) * mm, "end": v(367.09, -129.4) * mm});
            skLineSegment(sketch, "E61.7.0.6", {"start": v(369.76, -118.03) * mm, "end": v(374.02, -125.4) * mm});
            skArc(sketch, "E61.7.0.7", {"start": v(367.09, -129.4) * mm, "mid": v(371, -128.17) * mm, "end": v(374.02, -125.4) * mm});
            skArc(sketch, "E61.8.0.0", {"start": v(316.01, 9.37) * mm, "mid": v(312.1, 8.14) * mm, "end": v(309.08, 5.37) * mm});
            skLineSegment(sketch, "E61.8.0.1", {"start": v(313.34, -2) * mm, "end": v(309.08, 5.37) * mm});
            skLineSegment(sketch, "E61.8.0.2", {"start": v(320.26, 2) * mm, "end": v(316.01, 9.37) * mm});
            skLineSegment(sketch, "E61.8.0.3", {"start": v(320.26, 2) * mm, "end": v(389.56, -118.03) * mm});
            skLineSegment(sketch, "E61.8.0.4", {"start": v(313.34, -2) * mm, "end": v(382.64, -122.03) * mm});
            skLineSegment(sketch, "E61.8.0.5", {"start": v(382.64, -122.03) * mm, "end": v(386.89, -129.4) * mm});
            skLineSegment(sketch, "E61.8.0.6", {"start": v(389.56, -118.03) * mm, "end": v(393.82, -125.4) * mm});
            skArc(sketch, "E61.8.0.7", {"start": v(386.89, -129.4) * mm, "mid": v(390.8, -128.17) * mm, "end": v(393.82, -125.4) * mm});
            skArc(sketch, "E61.9.0.0", {"start": v(335.81, 9.37) * mm, "mid": v(331.9, 8.14) * mm, "end": v(328.88, 5.37) * mm});
            skLineSegment(sketch, "E61.9.0.1", {"start": v(333.14, -2) * mm, "end": v(328.88, 5.37) * mm});
            skLineSegment(sketch, "E61.9.0.2", {"start": v(340.06, 2) * mm, "end": v(335.81, 9.37) * mm});
            skLineSegment(sketch, "E61.9.0.3", {"start": v(340.06, 2) * mm, "end": v(409.36, -118.03) * mm});
            skLineSegment(sketch, "E61.9.0.4", {"start": v(333.14, -2) * mm, "end": v(402.44, -122.03) * mm});
            skLineSegment(sketch, "E61.9.0.5", {"start": v(402.44, -122.03) * mm, "end": v(406.69, -129.4) * mm});
            skLineSegment(sketch, "E61.9.0.6", {"start": v(409.36, -118.03) * mm, "end": v(413.62, -125.4) * mm});
            skArc(sketch, "E61.9.0.7", {"start": v(406.69, -129.4) * mm, "mid": v(410.6, -128.17) * mm, "end": v(413.62, -125.4) * mm});
            skArc(sketch, "E61.10.0.0", {"start": v(355.61, 9.37) * mm, "mid": v(351.7, 8.14) * mm, "end": v(348.68, 5.37) * mm});
            skLineSegment(sketch, "E61.10.0.1", {"start": v(352.94, -2) * mm, "end": v(348.68, 5.37) * mm});
            skLineSegment(sketch, "E61.10.0.2", {"start": v(359.86, 2) * mm, "end": v(355.61, 9.37) * mm});
            skLineSegment(sketch, "E61.10.0.3", {"start": v(359.86, 2) * mm, "end": v(429.16, -118.03) * mm});
            skLineSegment(sketch, "E61.10.0.4", {"start": v(352.94, -2) * mm, "end": v(422.24, -122.03) * mm});
            skLineSegment(sketch, "E61.10.0.5", {"start": v(422.24, -122.03) * mm, "end": v(426.49, -129.4) * mm});
            skLineSegment(sketch, "E61.10.0.6", {"start": v(429.16, -118.03) * mm, "end": v(433.42, -125.4) * mm});
            skArc(sketch, "E61.10.0.7", {"start": v(426.49, -129.4) * mm, "mid": v(430.4, -128.17) * mm, "end": v(433.42, -125.4) * mm});
            skArc(sketch, "E61.11.0.0", {"start": v(375.41, 9.37) * mm, "mid": v(371.5, 8.14) * mm, "end": v(368.48, 5.37) * mm});
            skLineSegment(sketch, "E61.11.0.1", {"start": v(372.74, -2) * mm, "end": v(368.48, 5.37) * mm});
            skLineSegment(sketch, "E61.11.0.2", {"start": v(379.66, 2) * mm, "end": v(375.41, 9.37) * mm});
            skLineSegment(sketch, "E61.11.0.3", {"start": v(379.66, 2) * mm, "end": v(448.96, -118.03) * mm});
            skLineSegment(sketch, "E61.11.0.4", {"start": v(372.74, -2) * mm, "end": v(442.04, -122.03) * mm});
            skLineSegment(sketch, "E61.11.0.5", {"start": v(442.04, -122.03) * mm, "end": v(446.29, -129.4) * mm});
            skLineSegment(sketch, "E61.11.0.6", {"start": v(448.96, -118.03) * mm, "end": v(453.22, -125.4) * mm});
            skArc(sketch, "E61.11.0.7", {"start": v(446.29, -129.4) * mm, "mid": v(450.2, -128.17) * mm, "end": v(453.22, -125.4) * mm});
            skArc(sketch, "E61.12.0.0", {"start": v(395.21, 9.37) * mm, "mid": v(391.3, 8.14) * mm, "end": v(388.28, 5.37) * mm});
            skLineSegment(sketch, "E61.12.0.1", {"start": v(392.54, -2) * mm, "end": v(388.28, 5.37) * mm});
            skLineSegment(sketch, "E61.12.0.2", {"start": v(399.46, 2) * mm, "end": v(395.21, 9.37) * mm});
            skLineSegment(sketch, "E61.12.0.3", {"start": v(399.46, 2) * mm, "end": v(468.76, -118.03) * mm});
            skLineSegment(sketch, "E61.12.0.4", {"start": v(392.54, -2) * mm, "end": v(461.84, -122.03) * mm});
            skLineSegment(sketch, "E61.12.0.5", {"start": v(461.84, -122.03) * mm, "end": v(466.09, -129.4) * mm});
            skLineSegment(sketch, "E61.12.0.6", {"start": v(468.76, -118.03) * mm, "end": v(473.02, -125.4) * mm});
            skArc(sketch, "E61.12.0.7", {"start": v(466.09, -129.4) * mm, "mid": v(470, -128.17) * mm, "end": v(473.02, -125.4) * mm});
            skArc(sketch, "E61.13.0.0", {"start": v(415.01, 9.37) * mm, "mid": v(411.1, 8.14) * mm, "end": v(408.08, 5.37) * mm});
            skLineSegment(sketch, "E61.13.0.1", {"start": v(412.34, -2) * mm, "end": v(408.08, 5.37) * mm});
            skLineSegment(sketch, "E61.13.0.2", {"start": v(419.26, 2) * mm, "end": v(415.01, 9.37) * mm});
            skLineSegment(sketch, "E61.13.0.3", {"start": v(419.26, 2) * mm, "end": v(488.56, -118.03) * mm});
            skLineSegment(sketch, "E61.13.0.4", {"start": v(412.34, -2) * mm, "end": v(481.64, -122.03) * mm});
            skLineSegment(sketch, "E61.13.0.5", {"start": v(481.64, -122.03) * mm, "end": v(485.89, -129.4) * mm});
            skLineSegment(sketch, "E61.13.0.6", {"start": v(488.56, -118.03) * mm, "end": v(492.82, -125.4) * mm});
            skArc(sketch, "E61.13.0.7", {"start": v(485.89, -129.4) * mm, "mid": v(489.8, -128.17) * mm, "end": v(492.82, -125.4) * mm});
            skArc(sketch, "E61.14.0.0", {"start": v(434.81, 9.37) * mm, "mid": v(430.9, 8.14) * mm, "end": v(427.88, 5.37) * mm});
            skLineSegment(sketch, "E61.14.0.1", {"start": v(432.14, -2) * mm, "end": v(427.88, 5.37) * mm});
            skLineSegment(sketch, "E61.14.0.2", {"start": v(439.06, 2) * mm, "end": v(434.81, 9.37) * mm});
            skLineSegment(sketch, "E61.14.0.3", {"start": v(439.06, 2) * mm, "end": v(508.36, -118.03) * mm});
            skLineSegment(sketch, "E61.14.0.4", {"start": v(432.14, -2) * mm, "end": v(501.44, -122.03) * mm});
            skLineSegment(sketch, "E61.14.0.5", {"start": v(501.44, -122.03) * mm, "end": v(505.69, -129.4) * mm});
            skLineSegment(sketch, "E61.14.0.6", {"start": v(508.36, -118.03) * mm, "end": v(512.62, -125.4) * mm});
            skArc(sketch, "E61.14.0.7", {"start": v(505.69, -129.4) * mm, "mid": v(509.6, -128.17) * mm, "end": v(512.62, -125.4) * mm});
            skArc(sketch, "E61.15.0.0", {"start": v(454.61, 9.37) * mm, "mid": v(450.7, 8.14) * mm, "end": v(447.68, 5.37) * mm});
            skLineSegment(sketch, "E61.15.0.1", {"start": v(451.94, -2) * mm, "end": v(447.68, 5.37) * mm});
            skLineSegment(sketch, "E61.15.0.2", {"start": v(458.86, 2) * mm, "end": v(454.61, 9.37) * mm});
            skLineSegment(sketch, "E61.15.0.3", {"start": v(458.86, 2) * mm, "end": v(528.16, -118.03) * mm});
            skLineSegment(sketch, "E61.15.0.4", {"start": v(451.94, -2) * mm, "end": v(521.24, -122.03) * mm});
            skLineSegment(sketch, "E61.15.0.5", {"start": v(521.24, -122.03) * mm, "end": v(525.49, -129.4) * mm});
            skLineSegment(sketch, "E61.15.0.6", {"start": v(528.16, -118.03) * mm, "end": v(532.42, -125.4) * mm});
            skArc(sketch, "E61.15.0.7", {"start": v(525.49, -129.4) * mm, "mid": v(529.4, -128.17) * mm, "end": v(532.42, -125.4) * mm});
            skLineSegment(sketch, "E61.direction1", {"start": v(150.68, 5.37) * mm, "end": v(170.48, 5.37) * mm, "construction": true});
            skSolve(sketch);
        }
        {
            var Q0;
            Q0=qSketchRegion(id+"F11",true);
            var Q1;
            {var subQ0=sQuery(id+"F3.wireOp",EDGE,"E25.0");var subQ1=sQuery(id+"F3.wireOp",EDGE,"E25.3");var subQ2=sQuery(id+"F3.wireOp",EDGE,"E25.1");var subQ3=sQuery(id+"F3.wireOp",EDGE,"E25.2");var subQ4=sQuery(id+"F3.wireOp",EDGE,"E25.4");var subQ5=sQuery(id+"F3.wireOp",EDGE,"E25.5");var subQ6=sQuery(id+"F3.wireOp",EDGE,"E25.6");var subQ7=sQuery(id+"F3.wireOp",EDGE,"E25.7");var subQ8=sQuery(id+"F3.wireOp",EDGE,"E25.8");var subQ9=sQuery(id+"F3.wireOp",EDGE,"E25.9");var subQ10=sQuery(id+"F3.wireOp",EDGE,"E25.10");var subQ11=sQuery(id+"F3.wireOp",EDGE,"E25.11");Q1=makeQuery(id+"F10.boolean.opBoolean","SPLIT",FACE,{"disambiguationData":[TD([makeQuery(id+"F4.opExtrude","SWEPT_FACE",FACE,{"disambiguationData":[OSD([subQ0])]}),makeQuery(id+"F4.opExtrude","SWEPT_FACE",FACE,{"disambiguationData":[OSD([subQ2])]}),makeQuery(id+"F4.opExtrude","SWEPT_FACE",FACE,{"disambiguationData":[OSD([subQ3])]}),makeQuery(id+"F4.opExtrude","SWEPT_FACE",FACE,{"disambiguationData":[OSD([subQ1])]}),makeQuery(id+"F4.opExtrude","SWEPT_FACE",FACE,{"disambiguationData":[OSD([subQ4])]}),makeQuery(id+"F4.opExtrude","SWEPT_FACE",FACE,{"disambiguationData":[OSD([subQ5])]}),makeQuery(id+"F4.opExtrude","SWEPT_FACE",FACE,{"disambiguationData":[OSD([subQ6])]}),makeQuery(id+"F4.opExtrude","SWEPT_FACE",FACE,{"disambiguationData":[OSD([subQ7])]}),makeQuery(id+"F4.opExtrude","SWEPT_FACE",FACE,{"disambiguationData":[OSD([subQ8])]}),makeQuery(id+"F4.opExtrude","SWEPT_FACE",FACE,{"disambiguationData":[OSD([subQ9])]}),makeQuery(id+"F4.opExtrude","SWEPT_FACE",FACE,{"disambiguationData":[OSD([subQ10])]}),makeQuery(id+"F4.opExtrude","SWEPT_FACE",FACE,{"disambiguationData":[OSD([subQ11])]}),makeQuery(id+"F6.boolean.opBoolean","COPY",FACE,{"derivedFrom":makeQuery(id+"F6.opExtrude","SWEPT_FACE",FACE,{"disambiguationData":[OSD([sQuery(id+"F5.wireOp",EDGE,"E26.0")])]})}),makeQuery(id+"F6.boolean.opBoolean","COPY",FACE,{"derivedFrom":makeQuery(id+"F6.opExtrude","SWEPT_FACE",FACE,{"disambiguationData":[OSD([sQuery(id+"F5.wireOp",EDGE,"E31.0.left"),sQuery(id+"F5.wireOp",EDGE,"E32")])]})}),makeQuery(id+"F6.boolean.opBoolean","COPY",FACE,{"derivedFrom":makeQuery(id+"F6.opExtrude","SWEPT_FACE",FACE,{"disambiguationData":[OSD([sQuery(id+"F5.wireOp",EDGE,"E31.0.right"),sQuery(id+"F5.wireOp",EDGE,"E33")])]})}),makeQuery(id+"F6.boolean.opBoolean","COPY",FACE,{"derivedFrom":makeQuery(id+"F6.opExtrude","SWEPT_FACE",FACE,{"disambiguationData":[OSD([sQuery(id+"F5.wireOp",EDGE,"E34.trimOffspring")])]})}),makeQuery(id+"F6.boolean.opBoolean","COPY",FACE,{"derivedFrom":makeQuery(id+"F6.opExtrude","SWEPT_FACE",FACE,{"disambiguationData":[OSD([sQuery(id+"F5.wireOp",EDGE,"E35.0.1.0")])]})}),makeQuery(id+"F6.boolean.opBoolean","COPY",FACE,{"derivedFrom":makeQuery(id+"F6.opExtrude","SWEPT_FACE",FACE,{"disambiguationData":[OSD([sQuery(id+"F5.wireOp",EDGE,"E35.0.1.1"),sQuery(id+"F5.wireOp",EDGE,"E35.0.1.3")])]})}),makeQuery(id+"F6.boolean.opBoolean","COPY",FACE,{"derivedFrom":makeQuery(id+"F6.opExtrude","SWEPT_FACE",FACE,{"disambiguationData":[OSD([sQuery(id+"F5.wireOp",EDGE,"E35.0.1.2"),sQuery(id+"F5.wireOp",EDGE,"E35.0.1.4")])]})}),makeQuery(id+"F6.boolean.opBoolean","COPY",FACE,{"derivedFrom":makeQuery(id+"F6.opExtrude","SWEPT_FACE",FACE,{"disambiguationData":[OSD([sQuery(id+"F5.wireOp",EDGE,"E35.0.1.5")])]})}),makeQuery(id+"F6.boolean.opBoolean","COPY",FACE,{"derivedFrom":makeQuery(id+"F6.opExtrude","SWEPT_FACE",FACE,{"disambiguationData":[OSD([sQuery(id+"F5.wireOp",EDGE,"E35.0.2.0")])]})}),makeQuery(id+"F6.boolean.opBoolean","COPY",FACE,{"derivedFrom":makeQuery(id+"F6.opExtrude","SWEPT_FACE",FACE,{"disambiguationData":[OSD([sQuery(id+"F5.wireOp",EDGE,"E35.0.2.1"),sQuery(id+"F5.wireOp",EDGE,"E35.0.2.3")])]})}),makeQuery(id+"F6.boolean.opBoolean","COPY",FACE,{"derivedFrom":makeQuery(id+"F6.opExtrude","SWEPT_FACE",FACE,{"disambiguationData":[OSD([sQuery(id+"F5.wireOp",EDGE,"E35.0.2.2"),sQuery(id+"F5.wireOp",EDGE,"E35.0.2.4")])]})}),makeQuery(id+"F6.boolean.opBoolean","COPY",FACE,{"derivedFrom":makeQuery(id+"F6.opExtrude","SWEPT_FACE",FACE,{"disambiguationData":[OSD([sQuery(id+"F5.wireOp",EDGE,"E35.0.2.5")])]})}),makeQuery(id+"F6.boolean.opBoolean","COPY",FACE,{"derivedFrom":makeQuery(id+"F6.opExtrude","SWEPT_FACE",FACE,{"disambiguationData":[OSD([sQuery(id+"F5.wireOp",EDGE,"E26.1")])]})}),makeQuery(id+"F6.boolean.opBoolean","COPY",FACE,{"derivedFrom":makeQuery(id+"F6.opExtrude","SWEPT_FACE",FACE,{"disambiguationData":[OSD([sQuery(id+"F5.wireOp",EDGE,"E35.0.3.1"),sQuery(id+"F5.wireOp",EDGE,"E35.0.3.3")])]})}),makeQuery(id+"F6.boolean.opBoolean","COPY",FACE,{"derivedFrom":makeQuery(id+"F6.opExtrude","SWEPT_FACE",FACE,{"disambiguationData":[OSD([sQuery(id+"F5.wireOp",EDGE,"E35.0.3.2"),sQuery(id+"F5.wireOp",EDGE,"E35.0.3.4")])]})}),makeQuery(id+"F6.boolean.opBoolean","COPY",FACE,{"derivedFrom":makeQuery(id+"F6.opExtrude","SWEPT_FACE",FACE,{"disambiguationData":[OSD([sQuery(id+"F5.wireOp",EDGE,"E35.0.3.5")])]})}),makeQuery(id+"F8.boolean.opBoolean","COPY",FACE,{"derivedFrom":makeQuery(id+"F8.opExtrude","SWEPT_FACE",FACE,{"disambiguationData":[OSD([sQuery(id+"F7.wireOp",EDGE,"E36.0")])]})}),makeQuery(id+"F8.boolean.opBoolean","COPY",FACE,{"derivedFrom":makeQuery(id+"F8.opExtrude","SWEPT_FACE",FACE,{"disambiguationData":[OSD([sQuery(id+"F7.wireOp",EDGE,"E39.0.left"),sQuery(id+"F7.wireOp",EDGE,"E40"),sQuery(id+"F7.wireOp",EDGE,"E42")])]})}),makeQuery(id+"F8.boolean.opBoolean","COPY",FACE,{"derivedFrom":makeQuery(id+"F8.opExtrude","SWEPT_FACE",FACE,{"disambiguationData":[OSD([sQuery(id+"F7.wireOp",EDGE,"E39.0.right"),sQuery(id+"F7.wireOp",EDGE,"E41"),sQuery(id+"F7.wireOp",EDGE,"E43")])]})}),makeQuery(id+"F8.boolean.opBoolean","COPY",FACE,{"derivedFrom":makeQuery(id+"F8.opExtrude","SWEPT_FACE",FACE,{"disambiguationData":[OSD([sQuery(id+"F7.wireOp",EDGE,"E44.trimOffspring")])]})}),makeQuery(id+"F8.boolean.opBoolean","COPY",FACE,{"derivedFrom":makeQuery(id+"F8.opExtrude","SWEPT_FACE",FACE,{"disambiguationData":[OSD([sQuery(id+"F7.wireOp",EDGE,"E45.0.1.0")])]})}),makeQuery(id+"F8.boolean.opBoolean","COPY",FACE,{"derivedFrom":makeQuery(id+"F8.opExtrude","SWEPT_FACE",FACE,{"disambiguationData":[OSD([sQuery(id+"F7.wireOp",EDGE,"E45.0.1.1"),sQuery(id+"F7.wireOp",EDGE,"E45.0.1.3"),sQuery(id+"F7.wireOp",EDGE,"E45.0.1.5")])]})}),makeQuery(id+"F8.boolean.opBoolean","COPY",FACE,{"derivedFrom":makeQuery(id+"F8.opExtrude","SWEPT_FACE",FACE,{"disambiguationData":[OSD([sQuery(id+"F7.wireOp",EDGE,"E45.0.1.2"),sQuery(id+"F7.wireOp",EDGE,"E45.0.1.4"),sQuery(id+"F7.wireOp",EDGE,"E45.0.1.6")])]})}),makeQuery(id+"F8.boolean.opBoolean","COPY",FACE,{"derivedFrom":makeQuery(id+"F8.opExtrude","SWEPT_FACE",FACE,{"disambiguationData":[OSD([sQuery(id+"F7.wireOp",EDGE,"E45.0.1.7")])]})}),makeQuery(id+"F8.boolean.opBoolean","COPY",FACE,{"derivedFrom":makeQuery(id+"F8.opExtrude","SWEPT_FACE",FACE,{"disambiguationData":[OSD([sQuery(id+"F7.wireOp",EDGE,"E45.0.2.0")])]})}),makeQuery(id+"F8.boolean.opBoolean","COPY",FACE,{"derivedFrom":makeQuery(id+"F8.opExtrude","SWEPT_FACE",FACE,{"disambiguationData":[OSD([sQuery(id+"F7.wireOp",EDGE,"E45.0.2.1"),sQuery(id+"F7.wireOp",EDGE,"E45.0.2.3"),sQuery(id+"F7.wireOp",EDGE,"E45.0.2.5")])]})}),makeQuery(id+"F8.boolean.opBoolean","COPY",FACE,{"derivedFrom":makeQuery(id+"F8.opExtrude","SWEPT_FACE",FACE,{"disambiguationData":[OSD([sQuery(id+"F7.wireOp",EDGE,"E45.0.2.2"),sQuery(id+"F7.wireOp",EDGE,"E45.0.2.4"),sQuery(id+"F7.wireOp",EDGE,"E45.0.2.6")])]})}),makeQuery(id+"F8.boolean.opBoolean","COPY",FACE,{"derivedFrom":makeQuery(id+"F8.opExtrude","SWEPT_FACE",FACE,{"disambiguationData":[OSD([sQuery(id+"F7.wireOp",EDGE,"E45.0.2.7")])]})}),makeQuery(id+"F8.boolean.opBoolean","COPY",FACE,{"derivedFrom":makeQuery(id+"F8.opExtrude","SWEPT_FACE",FACE,{"disambiguationData":[OSD([sQuery(id+"F7.wireOp",EDGE,"E36.1")])]})}),makeQuery(id+"F8.boolean.opBoolean","COPY",FACE,{"derivedFrom":makeQuery(id+"F8.opExtrude","SWEPT_FACE",FACE,{"disambiguationData":[OSD([sQuery(id+"F7.wireOp",EDGE,"E45.0.3.1"),sQuery(id+"F7.wireOp",EDGE,"E45.0.3.3"),sQuery(id+"F7.wireOp",EDGE,"E45.0.3.5")])]})}),makeQuery(id+"F8.boolean.opBoolean","COPY",FACE,{"derivedFrom":makeQuery(id+"F8.opExtrude","SWEPT_FACE",FACE,{"disambiguationData":[OSD([sQuery(id+"F7.wireOp",EDGE,"E45.0.3.2"),sQuery(id+"F7.wireOp",EDGE,"E45.0.3.4"),sQuery(id+"F7.wireOp",EDGE,"E45.0.3.6")])]})}),makeQuery(id+"F8.boolean.opBoolean","COPY",FACE,{"derivedFrom":makeQuery(id+"F8.opExtrude","SWEPT_FACE",FACE,{"disambiguationData":[OSD([sQuery(id+"F7.wireOp",EDGE,"E45.0.3.7")])]})}),makeQuery(id+"F10.opExtrude","SWEPT_FACE",FACE,{"disambiguationData":[OSD([sQuery(id+"F9.wireOp",EDGE,"E46.0")])]}),makeQuery(id+"F10.opExtrude","SWEPT_FACE",FACE,{"disambiguationData":[OSD([sQuery(id+"F9.wireOp",EDGE,"E46.1")])]}),makeQuery(id+"F10.opExtrude","SWEPT_FACE",FACE,{"disambiguationData":[OSD([sQuery(id+"F9.wireOp",EDGE,"E48.0.left"),sQuery(id+"F9.wireOp",EDGE,"E49"),sQuery(id+"F9.wireOp",EDGE,"E52")])]}),makeQuery(id+"F10.opExtrude","SWEPT_FACE",FACE,{"disambiguationData":[OSD([sQuery(id+"F9.wireOp",EDGE,"E48.0.right"),sQuery(id+"F9.wireOp",EDGE,"E50"),sQuery(id+"F9.wireOp",EDGE,"E51")])]}),makeQuery(id+"F10.opExtrude","SWEPT_FACE",FACE,{"disambiguationData":[OSD([sQuery(id+"F9.wireOp",EDGE,"E53.1.0.0")])]}),makeQuery(id+"F10.opExtrude","SWEPT_FACE",FACE,{"disambiguationData":[OSD([sQuery(id+"F9.wireOp",EDGE,"E53.1.0.1"),sQuery(id+"F9.wireOp",EDGE,"E53.1.0.4"),sQuery(id+"F9.wireOp",EDGE,"E53.1.0.5")])]}),makeQuery(id+"F10.opExtrude","SWEPT_FACE",FACE,{"disambiguationData":[OSD([sQuery(id+"F9.wireOp",EDGE,"E53.1.0.2"),sQuery(id+"F9.wireOp",EDGE,"E53.1.0.3"),sQuery(id+"F9.wireOp",EDGE,"E53.1.0.6")])]}),makeQuery(id+"F10.opExtrude","SWEPT_FACE",FACE,{"disambiguationData":[OSD([sQuery(id+"F9.wireOp",EDGE,"E53.1.0.7")])]}),makeQuery(id+"F10.opExtrude","SWEPT_FACE",FACE,{"disambiguationData":[OSD([sQuery(id+"F9.wireOp",EDGE,"E53.2.0.0")])]}),makeQuery(id+"F10.opExtrude","SWEPT_FACE",FACE,{"disambiguationData":[OSD([sQuery(id+"F9.wireOp",EDGE,"E53.2.0.1"),sQuery(id+"F9.wireOp",EDGE,"E53.2.0.4"),sQuery(id+"F9.wireOp",EDGE,"E53.2.0.5")])]}),makeQuery(id+"F10.opExtrude","SWEPT_FACE",FACE,{"disambiguationData":[OSD([sQuery(id+"F9.wireOp",EDGE,"E53.2.0.2"),sQuery(id+"F9.wireOp",EDGE,"E53.2.0.3"),sQuery(id+"F9.wireOp",EDGE,"E53.2.0.6")])]}),makeQuery(id+"F10.opExtrude","SWEPT_FACE",FACE,{"disambiguationData":[OSD([sQuery(id+"F9.wireOp",EDGE,"E53.2.0.7")])]}),makeQuery(id+"F10.opExtrude","SWEPT_FACE",FACE,{"disambiguationData":[OSD([sQuery(id+"F9.wireOp",EDGE,"E53.3.0.0")])]}),makeQuery(id+"F10.opExtrude","SWEPT_FACE",FACE,{"disambiguationData":[OSD([sQuery(id+"F9.wireOp",EDGE,"E53.3.0.1"),sQuery(id+"F9.wireOp",EDGE,"E53.3.0.4"),sQuery(id+"F9.wireOp",EDGE,"E53.3.0.5")])]}),makeQuery(id+"F10.opExtrude","SWEPT_FACE",FACE,{"disambiguationData":[OSD([sQuery(id+"F9.wireOp",EDGE,"E53.3.0.2"),sQuery(id+"F9.wireOp",EDGE,"E53.3.0.3"),sQuery(id+"F9.wireOp",EDGE,"E53.3.0.6")])]}),makeQuery(id+"F10.opExtrude","SWEPT_FACE",FACE,{"disambiguationData":[OSD([sQuery(id+"F9.wireOp",EDGE,"E53.3.0.7")])]}),makeQuery(id+"F10.opExtrude","SWEPT_FACE",FACE,{"disambiguationData":[OSD([sQuery(id+"F9.wireOp",EDGE,"E53.4.0.0")])]}),makeQuery(id+"F10.opExtrude","SWEPT_FACE",FACE,{"disambiguationData":[OSD([sQuery(id+"F9.wireOp",EDGE,"E53.4.0.1"),sQuery(id+"F9.wireOp",EDGE,"E53.4.0.4"),sQuery(id+"F9.wireOp",EDGE,"E53.4.0.5")])]}),makeQuery(id+"F10.opExtrude","SWEPT_FACE",FACE,{"disambiguationData":[OSD([sQuery(id+"F9.wireOp",EDGE,"E53.4.0.2"),sQuery(id+"F9.wireOp",EDGE,"E53.4.0.3"),sQuery(id+"F9.wireOp",EDGE,"E53.4.0.6")])]}),makeQuery(id+"F10.opExtrude","SWEPT_FACE",FACE,{"disambiguationData":[OSD([sQuery(id+"F9.wireOp",EDGE,"E53.4.0.7")])]}),makeQuery(id+"F10.opExtrude","SWEPT_FACE",FACE,{"disambiguationData":[OSD([sQuery(id+"F9.wireOp",EDGE,"E53.5.0.0")])]}),makeQuery(id+"F10.opExtrude","SWEPT_FACE",FACE,{"disambiguationData":[OSD([sQuery(id+"F9.wireOp",EDGE,"E53.5.0.1"),sQuery(id+"F9.wireOp",EDGE,"E53.5.0.4"),sQuery(id+"F9.wireOp",EDGE,"E53.5.0.5")])]}),makeQuery(id+"F10.opExtrude","SWEPT_FACE",FACE,{"disambiguationData":[OSD([sQuery(id+"F9.wireOp",EDGE,"E53.5.0.2"),sQuery(id+"F9.wireOp",EDGE,"E53.5.0.3"),sQuery(id+"F9.wireOp",EDGE,"E53.5.0.6")])]}),makeQuery(id+"F10.opExtrude","SWEPT_FACE",FACE,{"disambiguationData":[OSD([sQuery(id+"F9.wireOp",EDGE,"E53.5.0.7")])]}),makeQuery(id+"F10.opExtrude","SWEPT_FACE",FACE,{"disambiguationData":[OSD([sQuery(id+"F9.wireOp",EDGE,"E53.6.0.0")])]}),makeQuery(id+"F10.opExtrude","SWEPT_FACE",FACE,{"disambiguationData":[OSD([sQuery(id+"F9.wireOp",EDGE,"E53.6.0.1"),sQuery(id+"F9.wireOp",EDGE,"E53.6.0.4"),sQuery(id+"F9.wireOp",EDGE,"E53.6.0.5")])]}),makeQuery(id+"F10.opExtrude","SWEPT_FACE",FACE,{"disambiguationData":[OSD([sQuery(id+"F9.wireOp",EDGE,"E53.6.0.2"),sQuery(id+"F9.wireOp",EDGE,"E53.6.0.3"),sQuery(id+"F9.wireOp",EDGE,"E53.6.0.6")])]}),makeQuery(id+"F10.opExtrude","SWEPT_FACE",FACE,{"disambiguationData":[OSD([sQuery(id+"F9.wireOp",EDGE,"E53.6.0.7")])]}),makeQuery(id+"F10.opExtrude","SWEPT_FACE",FACE,{"disambiguationData":[OSD([sQuery(id+"F9.wireOp",EDGE,"E53.7.0.0")])]}),makeQuery(id+"F10.opExtrude","SWEPT_FACE",FACE,{"disambiguationData":[OSD([sQuery(id+"F9.wireOp",EDGE,"E53.7.0.1"),sQuery(id+"F9.wireOp",EDGE,"E53.7.0.4"),sQuery(id+"F9.wireOp",EDGE,"E53.7.0.5")])]}),makeQuery(id+"F10.opExtrude","SWEPT_FACE",FACE,{"disambiguationData":[OSD([sQuery(id+"F9.wireOp",EDGE,"E53.7.0.2"),sQuery(id+"F9.wireOp",EDGE,"E53.7.0.3"),sQuery(id+"F9.wireOp",EDGE,"E53.7.0.6")])]}),makeQuery(id+"F10.opExtrude","SWEPT_FACE",FACE,{"disambiguationData":[OSD([sQuery(id+"F9.wireOp",EDGE,"E53.7.0.7")])]})])],"derivedFrom":makeQuery(id+"F4.opExtrude","CAP_FACE",FACE,{"disambiguationData":[OSD([subQ0,subQ2,subQ3,subQ1,subQ4,subQ5,subQ6,subQ7,subQ8,subQ9,subQ10,subQ11])],"isStart":false})});}
            extrude(context, id + "F12", {"entities" : qUnion([Q0]), "operationType" : NewBodyOperationType.REMOVE, "endBound" : BoundingType.UP_TO_SURFACE, "endBoundEntityFace" : qUnion([Q1]), "depth" : 25 * mm});
        }
        {
            var Q0;
            Q0=makeQuery(id+"F10.boolean.opBoolean","SPLIT",BODY,{"disambiguationData":[OD(1.0)],"derivedFrom":makeQuery(id+"F4.opExtrude","SWEPT_BODY",BODY,{"disambiguationData":[OSD([sQuery(id+"F3.wireOp",EDGE,"E25.0"),sQuery(id+"F3.wireOp",EDGE,"E25.1"),sQuery(id+"F3.wireOp",EDGE,"E25.2"),sQuery(id+"F3.wireOp",EDGE,"E25.3"),sQuery(id+"F3.wireOp",EDGE,"E25.4"),sQuery(id+"F3.wireOp",EDGE,"E25.5"),sQuery(id+"F3.wireOp",EDGE,"E25.6"),sQuery(id+"F3.wireOp",EDGE,"E25.7"),sQuery(id+"F3.wireOp",EDGE,"E25.8"),sQuery(id+"F3.wireOp",EDGE,"E25.9"),sQuery(id+"F3.wireOp",EDGE,"E25.10"),sQuery(id+"F3.wireOp",EDGE,"E25.11")])]})});
            var Q1;
            Q1=makeQuery(id+"F10.boolean.opBoolean","SPLIT",BODY,{"disambiguationData":[OD(2.0)],"derivedFrom":makeQuery(id+"F4.opExtrude","SWEPT_BODY",BODY,{"disambiguationData":[OSD([sQuery(id+"F3.wireOp",EDGE,"E25.0"),sQuery(id+"F3.wireOp",EDGE,"E25.1"),sQuery(id+"F3.wireOp",EDGE,"E25.2"),sQuery(id+"F3.wireOp",EDGE,"E25.3"),sQuery(id+"F3.wireOp",EDGE,"E25.4"),sQuery(id+"F3.wireOp",EDGE,"E25.5"),sQuery(id+"F3.wireOp",EDGE,"E25.6"),sQuery(id+"F3.wireOp",EDGE,"E25.7"),sQuery(id+"F3.wireOp",EDGE,"E25.8"),sQuery(id+"F3.wireOp",EDGE,"E25.9"),sQuery(id+"F3.wireOp",EDGE,"E25.10"),sQuery(id+"F3.wireOp",EDGE,"E25.11")])]})});
            var Q2;
            Q2=makeQuery(id+"F10.boolean.opBoolean","SPLIT",BODY,{"disambiguationData":[OD(3.0)],"derivedFrom":makeQuery(id+"F4.opExtrude","SWEPT_BODY",BODY,{"disambiguationData":[OSD([sQuery(id+"F3.wireOp",EDGE,"E25.0"),sQuery(id+"F3.wireOp",EDGE,"E25.1"),sQuery(id+"F3.wireOp",EDGE,"E25.2"),sQuery(id+"F3.wireOp",EDGE,"E25.3"),sQuery(id+"F3.wireOp",EDGE,"E25.4"),sQuery(id+"F3.wireOp",EDGE,"E25.5"),sQuery(id+"F3.wireOp",EDGE,"E25.6"),sQuery(id+"F3.wireOp",EDGE,"E25.7"),sQuery(id+"F3.wireOp",EDGE,"E25.8"),sQuery(id+"F3.wireOp",EDGE,"E25.9"),sQuery(id+"F3.wireOp",EDGE,"E25.10"),sQuery(id+"F3.wireOp",EDGE,"E25.11")])]})});
            var Q3;
            Q3=makeQuery(id+"F10.boolean.opBoolean","SPLIT",BODY,{"disambiguationData":[OD(4.0)],"derivedFrom":makeQuery(id+"F4.opExtrude","SWEPT_BODY",BODY,{"disambiguationData":[OSD([sQuery(id+"F3.wireOp",EDGE,"E25.0"),sQuery(id+"F3.wireOp",EDGE,"E25.1"),sQuery(id+"F3.wireOp",EDGE,"E25.2"),sQuery(id+"F3.wireOp",EDGE,"E25.3"),sQuery(id+"F3.wireOp",EDGE,"E25.4"),sQuery(id+"F3.wireOp",EDGE,"E25.5"),sQuery(id+"F3.wireOp",EDGE,"E25.6"),sQuery(id+"F3.wireOp",EDGE,"E25.7"),sQuery(id+"F3.wireOp",EDGE,"E25.8"),sQuery(id+"F3.wireOp",EDGE,"E25.9"),sQuery(id+"F3.wireOp",EDGE,"E25.10"),sQuery(id+"F3.wireOp",EDGE,"E25.11")])]})});
            var Q4;
            Q4=makeQuery(id+"F10.boolean.opBoolean","SPLIT",BODY,{"disambiguationData":[OD(5.0)],"derivedFrom":makeQuery(id+"F4.opExtrude","SWEPT_BODY",BODY,{"disambiguationData":[OSD([sQuery(id+"F3.wireOp",EDGE,"E25.0"),sQuery(id+"F3.wireOp",EDGE,"E25.1"),sQuery(id+"F3.wireOp",EDGE,"E25.2"),sQuery(id+"F3.wireOp",EDGE,"E25.3"),sQuery(id+"F3.wireOp",EDGE,"E25.4"),sQuery(id+"F3.wireOp",EDGE,"E25.5"),sQuery(id+"F3.wireOp",EDGE,"E25.6"),sQuery(id+"F3.wireOp",EDGE,"E25.7"),sQuery(id+"F3.wireOp",EDGE,"E25.8"),sQuery(id+"F3.wireOp",EDGE,"E25.9"),sQuery(id+"F3.wireOp",EDGE,"E25.10"),sQuery(id+"F3.wireOp",EDGE,"E25.11")])]})});
            var Q5;
            Q5=makeQuery(id+"F10.boolean.opBoolean","SPLIT",BODY,{"disambiguationData":[OD(6.0)],"derivedFrom":makeQuery(id+"F4.opExtrude","SWEPT_BODY",BODY,{"disambiguationData":[OSD([sQuery(id+"F3.wireOp",EDGE,"E25.0"),sQuery(id+"F3.wireOp",EDGE,"E25.1"),sQuery(id+"F3.wireOp",EDGE,"E25.2"),sQuery(id+"F3.wireOp",EDGE,"E25.3"),sQuery(id+"F3.wireOp",EDGE,"E25.4"),sQuery(id+"F3.wireOp",EDGE,"E25.5"),sQuery(id+"F3.wireOp",EDGE,"E25.6"),sQuery(id+"F3.wireOp",EDGE,"E25.7"),sQuery(id+"F3.wireOp",EDGE,"E25.8"),sQuery(id+"F3.wireOp",EDGE,"E25.9"),sQuery(id+"F3.wireOp",EDGE,"E25.10"),sQuery(id+"F3.wireOp",EDGE,"E25.11")])]})});
            var Q6;
            Q6=makeQuery(id+"F10.boolean.opBoolean","SPLIT",BODY,{"disambiguationData":[OD(7.0)],"derivedFrom":makeQuery(id+"F4.opExtrude","SWEPT_BODY",BODY,{"disambiguationData":[OSD([sQuery(id+"F3.wireOp",EDGE,"E25.0"),sQuery(id+"F3.wireOp",EDGE,"E25.1"),sQuery(id+"F3.wireOp",EDGE,"E25.2"),sQuery(id+"F3.wireOp",EDGE,"E25.3"),sQuery(id+"F3.wireOp",EDGE,"E25.4"),sQuery(id+"F3.wireOp",EDGE,"E25.5"),sQuery(id+"F3.wireOp",EDGE,"E25.6"),sQuery(id+"F3.wireOp",EDGE,"E25.7"),sQuery(id+"F3.wireOp",EDGE,"E25.8"),sQuery(id+"F3.wireOp",EDGE,"E25.9"),sQuery(id+"F3.wireOp",EDGE,"E25.10"),sQuery(id+"F3.wireOp",EDGE,"E25.11")])]})});
            var Q7;
            Q7=makeQuery(id+"F10.boolean.opBoolean","SPLIT",BODY,{"disambiguationData":[OD(8.0)],"derivedFrom":makeQuery(id+"F4.opExtrude","SWEPT_BODY",BODY,{"disambiguationData":[OSD([sQuery(id+"F3.wireOp",EDGE,"E25.0"),sQuery(id+"F3.wireOp",EDGE,"E25.1"),sQuery(id+"F3.wireOp",EDGE,"E25.2"),sQuery(id+"F3.wireOp",EDGE,"E25.3"),sQuery(id+"F3.wireOp",EDGE,"E25.4"),sQuery(id+"F3.wireOp",EDGE,"E25.5"),sQuery(id+"F3.wireOp",EDGE,"E25.6"),sQuery(id+"F3.wireOp",EDGE,"E25.7"),sQuery(id+"F3.wireOp",EDGE,"E25.8"),sQuery(id+"F3.wireOp",EDGE,"E25.9"),sQuery(id+"F3.wireOp",EDGE,"E25.10"),sQuery(id+"F3.wireOp",EDGE,"E25.11")])]})});
            var Q8;
            Q8=makeQuery(id+"F10.boolean.opBoolean","SPLIT",BODY,{"disambiguationData":[OD(9.0)],"derivedFrom":makeQuery(id+"F4.opExtrude","SWEPT_BODY",BODY,{"disambiguationData":[OSD([sQuery(id+"F3.wireOp",EDGE,"E25.0"),sQuery(id+"F3.wireOp",EDGE,"E25.1"),sQuery(id+"F3.wireOp",EDGE,"E25.2"),sQuery(id+"F3.wireOp",EDGE,"E25.3"),sQuery(id+"F3.wireOp",EDGE,"E25.4"),sQuery(id+"F3.wireOp",EDGE,"E25.5"),sQuery(id+"F3.wireOp",EDGE,"E25.6"),sQuery(id+"F3.wireOp",EDGE,"E25.7"),sQuery(id+"F3.wireOp",EDGE,"E25.8"),sQuery(id+"F3.wireOp",EDGE,"E25.9"),sQuery(id+"F3.wireOp",EDGE,"E25.10"),sQuery(id+"F3.wireOp",EDGE,"E25.11")])]})});
            var Q9;
            Q9=makeQuery(id+"F10.boolean.opBoolean","SPLIT",BODY,{"disambiguationData":[OD(10.0)],"derivedFrom":makeQuery(id+"F4.opExtrude","SWEPT_BODY",BODY,{"disambiguationData":[OSD([sQuery(id+"F3.wireOp",EDGE,"E25.0"),sQuery(id+"F3.wireOp",EDGE,"E25.1"),sQuery(id+"F3.wireOp",EDGE,"E25.2"),sQuery(id+"F3.wireOp",EDGE,"E25.3"),sQuery(id+"F3.wireOp",EDGE,"E25.4"),sQuery(id+"F3.wireOp",EDGE,"E25.5"),sQuery(id+"F3.wireOp",EDGE,"E25.6"),sQuery(id+"F3.wireOp",EDGE,"E25.7"),sQuery(id+"F3.wireOp",EDGE,"E25.8"),sQuery(id+"F3.wireOp",EDGE,"E25.9"),sQuery(id+"F3.wireOp",EDGE,"E25.10"),sQuery(id+"F3.wireOp",EDGE,"E25.11")])]})});
            var Q10;
            Q10=makeQuery(id+"F10.boolean.opBoolean","SPLIT",BODY,{"disambiguationData":[OD(11.0)],"derivedFrom":makeQuery(id+"F4.opExtrude","SWEPT_BODY",BODY,{"disambiguationData":[OSD([sQuery(id+"F3.wireOp",EDGE,"E25.0"),sQuery(id+"F3.wireOp",EDGE,"E25.1"),sQuery(id+"F3.wireOp",EDGE,"E25.2"),sQuery(id+"F3.wireOp",EDGE,"E25.3"),sQuery(id+"F3.wireOp",EDGE,"E25.4"),sQuery(id+"F3.wireOp",EDGE,"E25.5"),sQuery(id+"F3.wireOp",EDGE,"E25.6"),sQuery(id+"F3.wireOp",EDGE,"E25.7"),sQuery(id+"F3.wireOp",EDGE,"E25.8"),sQuery(id+"F3.wireOp",EDGE,"E25.9"),sQuery(id+"F3.wireOp",EDGE,"E25.10"),sQuery(id+"F3.wireOp",EDGE,"E25.11")])]})});
            var Q11;
            Q11=makeQuery(id+"F10.boolean.opBoolean","SPLIT",BODY,{"disambiguationData":[OD(12.0)],"derivedFrom":makeQuery(id+"F4.opExtrude","SWEPT_BODY",BODY,{"disambiguationData":[OSD([sQuery(id+"F3.wireOp",EDGE,"E25.0"),sQuery(id+"F3.wireOp",EDGE,"E25.1"),sQuery(id+"F3.wireOp",EDGE,"E25.2"),sQuery(id+"F3.wireOp",EDGE,"E25.3"),sQuery(id+"F3.wireOp",EDGE,"E25.4"),sQuery(id+"F3.wireOp",EDGE,"E25.5"),sQuery(id+"F3.wireOp",EDGE,"E25.6"),sQuery(id+"F3.wireOp",EDGE,"E25.7"),sQuery(id+"F3.wireOp",EDGE,"E25.8"),sQuery(id+"F3.wireOp",EDGE,"E25.9"),sQuery(id+"F3.wireOp",EDGE,"E25.10"),sQuery(id+"F3.wireOp",EDGE,"E25.11")])]})});
            var Q12;
            Q12=makeQuery(id+"F10.boolean.opBoolean","SPLIT",BODY,{"disambiguationData":[OD(13.0)],"derivedFrom":makeQuery(id+"F4.opExtrude","SWEPT_BODY",BODY,{"disambiguationData":[OSD([sQuery(id+"F3.wireOp",EDGE,"E25.0"),sQuery(id+"F3.wireOp",EDGE,"E25.1"),sQuery(id+"F3.wireOp",EDGE,"E25.2"),sQuery(id+"F3.wireOp",EDGE,"E25.3"),sQuery(id+"F3.wireOp",EDGE,"E25.4"),sQuery(id+"F3.wireOp",EDGE,"E25.5"),sQuery(id+"F3.wireOp",EDGE,"E25.6"),sQuery(id+"F3.wireOp",EDGE,"E25.7"),sQuery(id+"F3.wireOp",EDGE,"E25.8"),sQuery(id+"F3.wireOp",EDGE,"E25.9"),sQuery(id+"F3.wireOp",EDGE,"E25.10"),sQuery(id+"F3.wireOp",EDGE,"E25.11")])]})});
            var Q13;
            Q13=makeQuery(id+"F10.boolean.opBoolean","SPLIT",BODY,{"disambiguationData":[OD(14.0)],"derivedFrom":makeQuery(id+"F4.opExtrude","SWEPT_BODY",BODY,{"disambiguationData":[OSD([sQuery(id+"F3.wireOp",EDGE,"E25.0"),sQuery(id+"F3.wireOp",EDGE,"E25.1"),sQuery(id+"F3.wireOp",EDGE,"E25.2"),sQuery(id+"F3.wireOp",EDGE,"E25.3"),sQuery(id+"F3.wireOp",EDGE,"E25.4"),sQuery(id+"F3.wireOp",EDGE,"E25.5"),sQuery(id+"F3.wireOp",EDGE,"E25.6"),sQuery(id+"F3.wireOp",EDGE,"E25.7"),sQuery(id+"F3.wireOp",EDGE,"E25.8"),sQuery(id+"F3.wireOp",EDGE,"E25.9"),sQuery(id+"F3.wireOp",EDGE,"E25.10"),sQuery(id+"F3.wireOp",EDGE,"E25.11")])]})});
            var Q14;
            Q14=makeQuery(id+"F10.boolean.opBoolean","SPLIT",BODY,{"disambiguationData":[OD(15.0)],"derivedFrom":makeQuery(id+"F4.opExtrude","SWEPT_BODY",BODY,{"disambiguationData":[OSD([sQuery(id+"F3.wireOp",EDGE,"E25.0"),sQuery(id+"F3.wireOp",EDGE,"E25.1"),sQuery(id+"F3.wireOp",EDGE,"E25.2"),sQuery(id+"F3.wireOp",EDGE,"E25.3"),sQuery(id+"F3.wireOp",EDGE,"E25.4"),sQuery(id+"F3.wireOp",EDGE,"E25.5"),sQuery(id+"F3.wireOp",EDGE,"E25.6"),sQuery(id+"F3.wireOp",EDGE,"E25.7"),sQuery(id+"F3.wireOp",EDGE,"E25.8"),sQuery(id+"F3.wireOp",EDGE,"E25.9"),sQuery(id+"F3.wireOp",EDGE,"E25.10"),sQuery(id+"F3.wireOp",EDGE,"E25.11")])]})});
            var Q15;
            Q15=makeQuery(id+"F10.boolean.opBoolean","SPLIT",BODY,{"disambiguationData":[OD(16.0)],"derivedFrom":makeQuery(id+"F4.opExtrude","SWEPT_BODY",BODY,{"disambiguationData":[OSD([sQuery(id+"F3.wireOp",EDGE,"E25.0"),sQuery(id+"F3.wireOp",EDGE,"E25.1"),sQuery(id+"F3.wireOp",EDGE,"E25.2"),sQuery(id+"F3.wireOp",EDGE,"E25.3"),sQuery(id+"F3.wireOp",EDGE,"E25.4"),sQuery(id+"F3.wireOp",EDGE,"E25.5"),sQuery(id+"F3.wireOp",EDGE,"E25.6"),sQuery(id+"F3.wireOp",EDGE,"E25.7"),sQuery(id+"F3.wireOp",EDGE,"E25.8"),sQuery(id+"F3.wireOp",EDGE,"E25.9"),sQuery(id+"F3.wireOp",EDGE,"E25.10"),sQuery(id+"F3.wireOp",EDGE,"E25.11")])]})});
            var Q16;
            Q16=makeQuery(id+"F10.boolean.opBoolean","SPLIT",BODY,{"disambiguationData":[OD(17.0)],"derivedFrom":makeQuery(id+"F4.opExtrude","SWEPT_BODY",BODY,{"disambiguationData":[OSD([sQuery(id+"F3.wireOp",EDGE,"E25.0"),sQuery(id+"F3.wireOp",EDGE,"E25.1"),sQuery(id+"F3.wireOp",EDGE,"E25.2"),sQuery(id+"F3.wireOp",EDGE,"E25.3"),sQuery(id+"F3.wireOp",EDGE,"E25.4"),sQuery(id+"F3.wireOp",EDGE,"E25.5"),sQuery(id+"F3.wireOp",EDGE,"E25.6"),sQuery(id+"F3.wireOp",EDGE,"E25.7"),sQuery(id+"F3.wireOp",EDGE,"E25.8"),sQuery(id+"F3.wireOp",EDGE,"E25.9"),sQuery(id+"F3.wireOp",EDGE,"E25.10"),sQuery(id+"F3.wireOp",EDGE,"E25.11")])]})});
            var Q17;
            Q17=makeQuery(id+"F10.boolean.opBoolean","SPLIT",BODY,{"disambiguationData":[OD(18.0)],"derivedFrom":makeQuery(id+"F4.opExtrude","SWEPT_BODY",BODY,{"disambiguationData":[OSD([sQuery(id+"F3.wireOp",EDGE,"E25.0"),sQuery(id+"F3.wireOp",EDGE,"E25.1"),sQuery(id+"F3.wireOp",EDGE,"E25.2"),sQuery(id+"F3.wireOp",EDGE,"E25.3"),sQuery(id+"F3.wireOp",EDGE,"E25.4"),sQuery(id+"F3.wireOp",EDGE,"E25.5"),sQuery(id+"F3.wireOp",EDGE,"E25.6"),sQuery(id+"F3.wireOp",EDGE,"E25.7"),sQuery(id+"F3.wireOp",EDGE,"E25.8"),sQuery(id+"F3.wireOp",EDGE,"E25.9"),sQuery(id+"F3.wireOp",EDGE,"E25.10"),sQuery(id+"F3.wireOp",EDGE,"E25.11")])]})});
            var Q18;
            Q18=makeQuery(id+"F10.boolean.opBoolean","SPLIT",BODY,{"disambiguationData":[OD(19.0)],"derivedFrom":makeQuery(id+"F4.opExtrude","SWEPT_BODY",BODY,{"disambiguationData":[OSD([sQuery(id+"F3.wireOp",EDGE,"E25.0"),sQuery(id+"F3.wireOp",EDGE,"E25.1"),sQuery(id+"F3.wireOp",EDGE,"E25.2"),sQuery(id+"F3.wireOp",EDGE,"E25.3"),sQuery(id+"F3.wireOp",EDGE,"E25.4"),sQuery(id+"F3.wireOp",EDGE,"E25.5"),sQuery(id+"F3.wireOp",EDGE,"E25.6"),sQuery(id+"F3.wireOp",EDGE,"E25.7"),sQuery(id+"F3.wireOp",EDGE,"E25.8"),sQuery(id+"F3.wireOp",EDGE,"E25.9"),sQuery(id+"F3.wireOp",EDGE,"E25.10"),sQuery(id+"F3.wireOp",EDGE,"E25.11")])]})});
            var Q19;
            Q19=makeQuery(id+"F10.boolean.opBoolean","SPLIT",BODY,{"disambiguationData":[OD(20.0)],"derivedFrom":makeQuery(id+"F4.opExtrude","SWEPT_BODY",BODY,{"disambiguationData":[OSD([sQuery(id+"F3.wireOp",EDGE,"E25.0"),sQuery(id+"F3.wireOp",EDGE,"E25.1"),sQuery(id+"F3.wireOp",EDGE,"E25.2"),sQuery(id+"F3.wireOp",EDGE,"E25.3"),sQuery(id+"F3.wireOp",EDGE,"E25.4"),sQuery(id+"F3.wireOp",EDGE,"E25.5"),sQuery(id+"F3.wireOp",EDGE,"E25.6"),sQuery(id+"F3.wireOp",EDGE,"E25.7"),sQuery(id+"F3.wireOp",EDGE,"E25.8"),sQuery(id+"F3.wireOp",EDGE,"E25.9"),sQuery(id+"F3.wireOp",EDGE,"E25.10"),sQuery(id+"F3.wireOp",EDGE,"E25.11")])]})});
            var Q20;
            Q20=makeQuery(id+"F10.boolean.opBoolean","SPLIT",BODY,{"disambiguationData":[OD(21.0)],"derivedFrom":makeQuery(id+"F4.opExtrude","SWEPT_BODY",BODY,{"disambiguationData":[OSD([sQuery(id+"F3.wireOp",EDGE,"E25.0"),sQuery(id+"F3.wireOp",EDGE,"E25.1"),sQuery(id+"F3.wireOp",EDGE,"E25.2"),sQuery(id+"F3.wireOp",EDGE,"E25.3"),sQuery(id+"F3.wireOp",EDGE,"E25.4"),sQuery(id+"F3.wireOp",EDGE,"E25.5"),sQuery(id+"F3.wireOp",EDGE,"E25.6"),sQuery(id+"F3.wireOp",EDGE,"E25.7"),sQuery(id+"F3.wireOp",EDGE,"E25.8"),sQuery(id+"F3.wireOp",EDGE,"E25.9"),sQuery(id+"F3.wireOp",EDGE,"E25.10"),sQuery(id+"F3.wireOp",EDGE,"E25.11")])]})});
            var Q21;
            Q21=makeQuery(id+"F12.boolean.opBoolean","SPLIT",BODY,{"disambiguationData":[OD(0.0)],"derivedFrom":makeQuery(id+"F10.boolean.opBoolean","SPLIT",BODY,{"disambiguationData":[OD(0.0)],"derivedFrom":makeQuery(id+"F4.opExtrude","SWEPT_BODY",BODY,{"disambiguationData":[OSD([sQuery(id+"F3.wireOp",EDGE,"E25.0"),sQuery(id+"F3.wireOp",EDGE,"E25.1"),sQuery(id+"F3.wireOp",EDGE,"E25.2"),sQuery(id+"F3.wireOp",EDGE,"E25.3"),sQuery(id+"F3.wireOp",EDGE,"E25.4"),sQuery(id+"F3.wireOp",EDGE,"E25.5"),sQuery(id+"F3.wireOp",EDGE,"E25.6"),sQuery(id+"F3.wireOp",EDGE,"E25.7"),sQuery(id+"F3.wireOp",EDGE,"E25.8"),sQuery(id+"F3.wireOp",EDGE,"E25.9"),sQuery(id+"F3.wireOp",EDGE,"E25.10"),sQuery(id+"F3.wireOp",EDGE,"E25.11")])]})})});
            var Q22;
            Q22=makeQuery(id+"F12.boolean.opBoolean","SPLIT",BODY,{"disambiguationData":[OD(1.0)],"derivedFrom":makeQuery(id+"F10.boolean.opBoolean","SPLIT",BODY,{"disambiguationData":[OD(0.0)],"derivedFrom":makeQuery(id+"F4.opExtrude","SWEPT_BODY",BODY,{"disambiguationData":[OSD([sQuery(id+"F3.wireOp",EDGE,"E25.0"),sQuery(id+"F3.wireOp",EDGE,"E25.1"),sQuery(id+"F3.wireOp",EDGE,"E25.2"),sQuery(id+"F3.wireOp",EDGE,"E25.3"),sQuery(id+"F3.wireOp",EDGE,"E25.4"),sQuery(id+"F3.wireOp",EDGE,"E25.5"),sQuery(id+"F3.wireOp",EDGE,"E25.6"),sQuery(id+"F3.wireOp",EDGE,"E25.7"),sQuery(id+"F3.wireOp",EDGE,"E25.8"),sQuery(id+"F3.wireOp",EDGE,"E25.9"),sQuery(id+"F3.wireOp",EDGE,"E25.10"),sQuery(id+"F3.wireOp",EDGE,"E25.11")])]})})});
            var Q23;
            Q23=makeQuery(id+"F12.boolean.opBoolean","SPLIT",BODY,{"disambiguationData":[OD(2.0)],"derivedFrom":makeQuery(id+"F10.boolean.opBoolean","SPLIT",BODY,{"disambiguationData":[OD(0.0)],"derivedFrom":makeQuery(id+"F4.opExtrude","SWEPT_BODY",BODY,{"disambiguationData":[OSD([sQuery(id+"F3.wireOp",EDGE,"E25.0"),sQuery(id+"F3.wireOp",EDGE,"E25.1"),sQuery(id+"F3.wireOp",EDGE,"E25.2"),sQuery(id+"F3.wireOp",EDGE,"E25.3"),sQuery(id+"F3.wireOp",EDGE,"E25.4"),sQuery(id+"F3.wireOp",EDGE,"E25.5"),sQuery(id+"F3.wireOp",EDGE,"E25.6"),sQuery(id+"F3.wireOp",EDGE,"E25.7"),sQuery(id+"F3.wireOp",EDGE,"E25.8"),sQuery(id+"F3.wireOp",EDGE,"E25.9"),sQuery(id+"F3.wireOp",EDGE,"E25.10"),sQuery(id+"F3.wireOp",EDGE,"E25.11")])]})})});
            var Q24;
            Q24=makeQuery(id+"F12.boolean.opBoolean","SPLIT",BODY,{"disambiguationData":[OD(3.0)],"derivedFrom":makeQuery(id+"F10.boolean.opBoolean","SPLIT",BODY,{"disambiguationData":[OD(0.0)],"derivedFrom":makeQuery(id+"F4.opExtrude","SWEPT_BODY",BODY,{"disambiguationData":[OSD([sQuery(id+"F3.wireOp",EDGE,"E25.0"),sQuery(id+"F3.wireOp",EDGE,"E25.1"),sQuery(id+"F3.wireOp",EDGE,"E25.2"),sQuery(id+"F3.wireOp",EDGE,"E25.3"),sQuery(id+"F3.wireOp",EDGE,"E25.4"),sQuery(id+"F3.wireOp",EDGE,"E25.5"),sQuery(id+"F3.wireOp",EDGE,"E25.6"),sQuery(id+"F3.wireOp",EDGE,"E25.7"),sQuery(id+"F3.wireOp",EDGE,"E25.8"),sQuery(id+"F3.wireOp",EDGE,"E25.9"),sQuery(id+"F3.wireOp",EDGE,"E25.10"),sQuery(id+"F3.wireOp",EDGE,"E25.11")])]})})});
            var Q25;
            Q25=makeQuery(id+"F12.boolean.opBoolean","SPLIT",BODY,{"disambiguationData":[OD(4.0)],"derivedFrom":makeQuery(id+"F10.boolean.opBoolean","SPLIT",BODY,{"disambiguationData":[OD(0.0)],"derivedFrom":makeQuery(id+"F4.opExtrude","SWEPT_BODY",BODY,{"disambiguationData":[OSD([sQuery(id+"F3.wireOp",EDGE,"E25.0"),sQuery(id+"F3.wireOp",EDGE,"E25.1"),sQuery(id+"F3.wireOp",EDGE,"E25.2"),sQuery(id+"F3.wireOp",EDGE,"E25.3"),sQuery(id+"F3.wireOp",EDGE,"E25.4"),sQuery(id+"F3.wireOp",EDGE,"E25.5"),sQuery(id+"F3.wireOp",EDGE,"E25.6"),sQuery(id+"F3.wireOp",EDGE,"E25.7"),sQuery(id+"F3.wireOp",EDGE,"E25.8"),sQuery(id+"F3.wireOp",EDGE,"E25.9"),sQuery(id+"F3.wireOp",EDGE,"E25.10"),sQuery(id+"F3.wireOp",EDGE,"E25.11")])]})})});
            var Q26;
            Q26=makeQuery(id+"F12.boolean.opBoolean","SPLIT",BODY,{"disambiguationData":[OD(5.0)],"derivedFrom":makeQuery(id+"F10.boolean.opBoolean","SPLIT",BODY,{"disambiguationData":[OD(0.0)],"derivedFrom":makeQuery(id+"F4.opExtrude","SWEPT_BODY",BODY,{"disambiguationData":[OSD([sQuery(id+"F3.wireOp",EDGE,"E25.0"),sQuery(id+"F3.wireOp",EDGE,"E25.1"),sQuery(id+"F3.wireOp",EDGE,"E25.2"),sQuery(id+"F3.wireOp",EDGE,"E25.3"),sQuery(id+"F3.wireOp",EDGE,"E25.4"),sQuery(id+"F3.wireOp",EDGE,"E25.5"),sQuery(id+"F3.wireOp",EDGE,"E25.6"),sQuery(id+"F3.wireOp",EDGE,"E25.7"),sQuery(id+"F3.wireOp",EDGE,"E25.8"),sQuery(id+"F3.wireOp",EDGE,"E25.9"),sQuery(id+"F3.wireOp",EDGE,"E25.10"),sQuery(id+"F3.wireOp",EDGE,"E25.11")])]})})});
            var Q27;
            Q27=makeQuery(id+"F12.boolean.opBoolean","SPLIT",BODY,{"disambiguationData":[OD(6.0)],"derivedFrom":makeQuery(id+"F10.boolean.opBoolean","SPLIT",BODY,{"disambiguationData":[OD(0.0)],"derivedFrom":makeQuery(id+"F4.opExtrude","SWEPT_BODY",BODY,{"disambiguationData":[OSD([sQuery(id+"F3.wireOp",EDGE,"E25.0"),sQuery(id+"F3.wireOp",EDGE,"E25.1"),sQuery(id+"F3.wireOp",EDGE,"E25.2"),sQuery(id+"F3.wireOp",EDGE,"E25.3"),sQuery(id+"F3.wireOp",EDGE,"E25.4"),sQuery(id+"F3.wireOp",EDGE,"E25.5"),sQuery(id+"F3.wireOp",EDGE,"E25.6"),sQuery(id+"F3.wireOp",EDGE,"E25.7"),sQuery(id+"F3.wireOp",EDGE,"E25.8"),sQuery(id+"F3.wireOp",EDGE,"E25.9"),sQuery(id+"F3.wireOp",EDGE,"E25.10"),sQuery(id+"F3.wireOp",EDGE,"E25.11")])]})})});
            var Q28;
            Q28=makeQuery(id+"F12.boolean.opBoolean","SPLIT",BODY,{"disambiguationData":[OD(7.0)],"derivedFrom":makeQuery(id+"F10.boolean.opBoolean","SPLIT",BODY,{"disambiguationData":[OD(0.0)],"derivedFrom":makeQuery(id+"F4.opExtrude","SWEPT_BODY",BODY,{"disambiguationData":[OSD([sQuery(id+"F3.wireOp",EDGE,"E25.0"),sQuery(id+"F3.wireOp",EDGE,"E25.1"),sQuery(id+"F3.wireOp",EDGE,"E25.2"),sQuery(id+"F3.wireOp",EDGE,"E25.3"),sQuery(id+"F3.wireOp",EDGE,"E25.4"),sQuery(id+"F3.wireOp",EDGE,"E25.5"),sQuery(id+"F3.wireOp",EDGE,"E25.6"),sQuery(id+"F3.wireOp",EDGE,"E25.7"),sQuery(id+"F3.wireOp",EDGE,"E25.8"),sQuery(id+"F3.wireOp",EDGE,"E25.9"),sQuery(id+"F3.wireOp",EDGE,"E25.10"),sQuery(id+"F3.wireOp",EDGE,"E25.11")])]})})});
            var Q29;
            Q29=makeQuery(id+"F12.boolean.opBoolean","SPLIT",BODY,{"disambiguationData":[OD(8.0)],"derivedFrom":makeQuery(id+"F10.boolean.opBoolean","SPLIT",BODY,{"disambiguationData":[OD(0.0)],"derivedFrom":makeQuery(id+"F4.opExtrude","SWEPT_BODY",BODY,{"disambiguationData":[OSD([sQuery(id+"F3.wireOp",EDGE,"E25.0"),sQuery(id+"F3.wireOp",EDGE,"E25.1"),sQuery(id+"F3.wireOp",EDGE,"E25.2"),sQuery(id+"F3.wireOp",EDGE,"E25.3"),sQuery(id+"F3.wireOp",EDGE,"E25.4"),sQuery(id+"F3.wireOp",EDGE,"E25.5"),sQuery(id+"F3.wireOp",EDGE,"E25.6"),sQuery(id+"F3.wireOp",EDGE,"E25.7"),sQuery(id+"F3.wireOp",EDGE,"E25.8"),sQuery(id+"F3.wireOp",EDGE,"E25.9"),sQuery(id+"F3.wireOp",EDGE,"E25.10"),sQuery(id+"F3.wireOp",EDGE,"E25.11")])]})})});
            var Q30;
            Q30=makeQuery(id+"F12.boolean.opBoolean","SPLIT",BODY,{"disambiguationData":[OD(9.0)],"derivedFrom":makeQuery(id+"F10.boolean.opBoolean","SPLIT",BODY,{"disambiguationData":[OD(0.0)],"derivedFrom":makeQuery(id+"F4.opExtrude","SWEPT_BODY",BODY,{"disambiguationData":[OSD([sQuery(id+"F3.wireOp",EDGE,"E25.0"),sQuery(id+"F3.wireOp",EDGE,"E25.1"),sQuery(id+"F3.wireOp",EDGE,"E25.2"),sQuery(id+"F3.wireOp",EDGE,"E25.3"),sQuery(id+"F3.wireOp",EDGE,"E25.4"),sQuery(id+"F3.wireOp",EDGE,"E25.5"),sQuery(id+"F3.wireOp",EDGE,"E25.6"),sQuery(id+"F3.wireOp",EDGE,"E25.7"),sQuery(id+"F3.wireOp",EDGE,"E25.8"),sQuery(id+"F3.wireOp",EDGE,"E25.9"),sQuery(id+"F3.wireOp",EDGE,"E25.10"),sQuery(id+"F3.wireOp",EDGE,"E25.11")])]})})});
            var Q31;
            Q31=makeQuery(id+"F12.boolean.opBoolean","SPLIT",BODY,{"disambiguationData":[OD(10.0)],"derivedFrom":makeQuery(id+"F10.boolean.opBoolean","SPLIT",BODY,{"disambiguationData":[OD(0.0)],"derivedFrom":makeQuery(id+"F4.opExtrude","SWEPT_BODY",BODY,{"disambiguationData":[OSD([sQuery(id+"F3.wireOp",EDGE,"E25.0"),sQuery(id+"F3.wireOp",EDGE,"E25.1"),sQuery(id+"F3.wireOp",EDGE,"E25.2"),sQuery(id+"F3.wireOp",EDGE,"E25.3"),sQuery(id+"F3.wireOp",EDGE,"E25.4"),sQuery(id+"F3.wireOp",EDGE,"E25.5"),sQuery(id+"F3.wireOp",EDGE,"E25.6"),sQuery(id+"F3.wireOp",EDGE,"E25.7"),sQuery(id+"F3.wireOp",EDGE,"E25.8"),sQuery(id+"F3.wireOp",EDGE,"E25.9"),sQuery(id+"F3.wireOp",EDGE,"E25.10"),sQuery(id+"F3.wireOp",EDGE,"E25.11")])]})})});
            var Q32;
            Q32=makeQuery(id+"F12.boolean.opBoolean","SPLIT",BODY,{"disambiguationData":[OD(11.0)],"derivedFrom":makeQuery(id+"F10.boolean.opBoolean","SPLIT",BODY,{"disambiguationData":[OD(0.0)],"derivedFrom":makeQuery(id+"F4.opExtrude","SWEPT_BODY",BODY,{"disambiguationData":[OSD([sQuery(id+"F3.wireOp",EDGE,"E25.0"),sQuery(id+"F3.wireOp",EDGE,"E25.1"),sQuery(id+"F3.wireOp",EDGE,"E25.2"),sQuery(id+"F3.wireOp",EDGE,"E25.3"),sQuery(id+"F3.wireOp",EDGE,"E25.4"),sQuery(id+"F3.wireOp",EDGE,"E25.5"),sQuery(id+"F3.wireOp",EDGE,"E25.6"),sQuery(id+"F3.wireOp",EDGE,"E25.7"),sQuery(id+"F3.wireOp",EDGE,"E25.8"),sQuery(id+"F3.wireOp",EDGE,"E25.9"),sQuery(id+"F3.wireOp",EDGE,"E25.10"),sQuery(id+"F3.wireOp",EDGE,"E25.11")])]})})});
            var Q33;
            Q33=makeQuery(id+"F12.boolean.opBoolean","SPLIT",BODY,{"disambiguationData":[OD(12.0)],"derivedFrom":makeQuery(id+"F10.boolean.opBoolean","SPLIT",BODY,{"disambiguationData":[OD(0.0)],"derivedFrom":makeQuery(id+"F4.opExtrude","SWEPT_BODY",BODY,{"disambiguationData":[OSD([sQuery(id+"F3.wireOp",EDGE,"E25.0"),sQuery(id+"F3.wireOp",EDGE,"E25.1"),sQuery(id+"F3.wireOp",EDGE,"E25.2"),sQuery(id+"F3.wireOp",EDGE,"E25.3"),sQuery(id+"F3.wireOp",EDGE,"E25.4"),sQuery(id+"F3.wireOp",EDGE,"E25.5"),sQuery(id+"F3.wireOp",EDGE,"E25.6"),sQuery(id+"F3.wireOp",EDGE,"E25.7"),sQuery(id+"F3.wireOp",EDGE,"E25.8"),sQuery(id+"F3.wireOp",EDGE,"E25.9"),sQuery(id+"F3.wireOp",EDGE,"E25.10"),sQuery(id+"F3.wireOp",EDGE,"E25.11")])]})})});
            var Q34;
            Q34=makeQuery(id+"F12.boolean.opBoolean","SPLIT",BODY,{"disambiguationData":[OD(13.0)],"derivedFrom":makeQuery(id+"F10.boolean.opBoolean","SPLIT",BODY,{"disambiguationData":[OD(0.0)],"derivedFrom":makeQuery(id+"F4.opExtrude","SWEPT_BODY",BODY,{"disambiguationData":[OSD([sQuery(id+"F3.wireOp",EDGE,"E25.0"),sQuery(id+"F3.wireOp",EDGE,"E25.1"),sQuery(id+"F3.wireOp",EDGE,"E25.2"),sQuery(id+"F3.wireOp",EDGE,"E25.3"),sQuery(id+"F3.wireOp",EDGE,"E25.4"),sQuery(id+"F3.wireOp",EDGE,"E25.5"),sQuery(id+"F3.wireOp",EDGE,"E25.6"),sQuery(id+"F3.wireOp",EDGE,"E25.7"),sQuery(id+"F3.wireOp",EDGE,"E25.8"),sQuery(id+"F3.wireOp",EDGE,"E25.9"),sQuery(id+"F3.wireOp",EDGE,"E25.10"),sQuery(id+"F3.wireOp",EDGE,"E25.11")])]})})});
            var Q35;
            Q35=makeQuery(id+"F12.boolean.opBoolean","SPLIT",BODY,{"disambiguationData":[OD(14.0)],"derivedFrom":makeQuery(id+"F10.boolean.opBoolean","SPLIT",BODY,{"disambiguationData":[OD(0.0)],"derivedFrom":makeQuery(id+"F4.opExtrude","SWEPT_BODY",BODY,{"disambiguationData":[OSD([sQuery(id+"F3.wireOp",EDGE,"E25.0"),sQuery(id+"F3.wireOp",EDGE,"E25.1"),sQuery(id+"F3.wireOp",EDGE,"E25.2"),sQuery(id+"F3.wireOp",EDGE,"E25.3"),sQuery(id+"F3.wireOp",EDGE,"E25.4"),sQuery(id+"F3.wireOp",EDGE,"E25.5"),sQuery(id+"F3.wireOp",EDGE,"E25.6"),sQuery(id+"F3.wireOp",EDGE,"E25.7"),sQuery(id+"F3.wireOp",EDGE,"E25.8"),sQuery(id+"F3.wireOp",EDGE,"E25.9"),sQuery(id+"F3.wireOp",EDGE,"E25.10"),sQuery(id+"F3.wireOp",EDGE,"E25.11")])]})})});
            var Q36;
            Q36=makeQuery(id+"F12.boolean.opBoolean","SPLIT",BODY,{"disambiguationData":[OD(15.0)],"derivedFrom":makeQuery(id+"F10.boolean.opBoolean","SPLIT",BODY,{"disambiguationData":[OD(0.0)],"derivedFrom":makeQuery(id+"F4.opExtrude","SWEPT_BODY",BODY,{"disambiguationData":[OSD([sQuery(id+"F3.wireOp",EDGE,"E25.0"),sQuery(id+"F3.wireOp",EDGE,"E25.1"),sQuery(id+"F3.wireOp",EDGE,"E25.2"),sQuery(id+"F3.wireOp",EDGE,"E25.3"),sQuery(id+"F3.wireOp",EDGE,"E25.4"),sQuery(id+"F3.wireOp",EDGE,"E25.5"),sQuery(id+"F3.wireOp",EDGE,"E25.6"),sQuery(id+"F3.wireOp",EDGE,"E25.7"),sQuery(id+"F3.wireOp",EDGE,"E25.8"),sQuery(id+"F3.wireOp",EDGE,"E25.9"),sQuery(id+"F3.wireOp",EDGE,"E25.10"),sQuery(id+"F3.wireOp",EDGE,"E25.11")])]})})});
            var Q37;
            Q37=makeQuery(id+"F12.boolean.opBoolean","SPLIT",BODY,{"disambiguationData":[OD(16.0)],"derivedFrom":makeQuery(id+"F10.boolean.opBoolean","SPLIT",BODY,{"disambiguationData":[OD(0.0)],"derivedFrom":makeQuery(id+"F4.opExtrude","SWEPT_BODY",BODY,{"disambiguationData":[OSD([sQuery(id+"F3.wireOp",EDGE,"E25.0"),sQuery(id+"F3.wireOp",EDGE,"E25.1"),sQuery(id+"F3.wireOp",EDGE,"E25.2"),sQuery(id+"F3.wireOp",EDGE,"E25.3"),sQuery(id+"F3.wireOp",EDGE,"E25.4"),sQuery(id+"F3.wireOp",EDGE,"E25.5"),sQuery(id+"F3.wireOp",EDGE,"E25.6"),sQuery(id+"F3.wireOp",EDGE,"E25.7"),sQuery(id+"F3.wireOp",EDGE,"E25.8"),sQuery(id+"F3.wireOp",EDGE,"E25.9"),sQuery(id+"F3.wireOp",EDGE,"E25.10"),sQuery(id+"F3.wireOp",EDGE,"E25.11")])]})})});
            var Q38;
            Q38=makeQuery(id+"F12.boolean.opBoolean","SPLIT",BODY,{"disambiguationData":[OD(17.0)],"derivedFrom":makeQuery(id+"F10.boolean.opBoolean","SPLIT",BODY,{"disambiguationData":[OD(0.0)],"derivedFrom":makeQuery(id+"F4.opExtrude","SWEPT_BODY",BODY,{"disambiguationData":[OSD([sQuery(id+"F3.wireOp",EDGE,"E25.0"),sQuery(id+"F3.wireOp",EDGE,"E25.1"),sQuery(id+"F3.wireOp",EDGE,"E25.2"),sQuery(id+"F3.wireOp",EDGE,"E25.3"),sQuery(id+"F3.wireOp",EDGE,"E25.4"),sQuery(id+"F3.wireOp",EDGE,"E25.5"),sQuery(id+"F3.wireOp",EDGE,"E25.6"),sQuery(id+"F3.wireOp",EDGE,"E25.7"),sQuery(id+"F3.wireOp",EDGE,"E25.8"),sQuery(id+"F3.wireOp",EDGE,"E25.9"),sQuery(id+"F3.wireOp",EDGE,"E25.10"),sQuery(id+"F3.wireOp",EDGE,"E25.11")])]})})});
            var Q39;
            Q39=makeQuery(id+"F12.boolean.opBoolean","SPLIT",BODY,{"disambiguationData":[OD(18.0)],"derivedFrom":makeQuery(id+"F10.boolean.opBoolean","SPLIT",BODY,{"disambiguationData":[OD(0.0)],"derivedFrom":makeQuery(id+"F4.opExtrude","SWEPT_BODY",BODY,{"disambiguationData":[OSD([sQuery(id+"F3.wireOp",EDGE,"E25.0"),sQuery(id+"F3.wireOp",EDGE,"E25.1"),sQuery(id+"F3.wireOp",EDGE,"E25.2"),sQuery(id+"F3.wireOp",EDGE,"E25.3"),sQuery(id+"F3.wireOp",EDGE,"E25.4"),sQuery(id+"F3.wireOp",EDGE,"E25.5"),sQuery(id+"F3.wireOp",EDGE,"E25.6"),sQuery(id+"F3.wireOp",EDGE,"E25.7"),sQuery(id+"F3.wireOp",EDGE,"E25.8"),sQuery(id+"F3.wireOp",EDGE,"E25.9"),sQuery(id+"F3.wireOp",EDGE,"E25.10"),sQuery(id+"F3.wireOp",EDGE,"E25.11")])]})})});
            var Q40;
            Q40=makeQuery(id+"F12.boolean.opBoolean","SPLIT",BODY,{"disambiguationData":[OD(19.0)],"derivedFrom":makeQuery(id+"F10.boolean.opBoolean","SPLIT",BODY,{"disambiguationData":[OD(0.0)],"derivedFrom":makeQuery(id+"F4.opExtrude","SWEPT_BODY",BODY,{"disambiguationData":[OSD([sQuery(id+"F3.wireOp",EDGE,"E25.0"),sQuery(id+"F3.wireOp",EDGE,"E25.1"),sQuery(id+"F3.wireOp",EDGE,"E25.2"),sQuery(id+"F3.wireOp",EDGE,"E25.3"),sQuery(id+"F3.wireOp",EDGE,"E25.4"),sQuery(id+"F3.wireOp",EDGE,"E25.5"),sQuery(id+"F3.wireOp",EDGE,"E25.6"),sQuery(id+"F3.wireOp",EDGE,"E25.7"),sQuery(id+"F3.wireOp",EDGE,"E25.8"),sQuery(id+"F3.wireOp",EDGE,"E25.9"),sQuery(id+"F3.wireOp",EDGE,"E25.10"),sQuery(id+"F3.wireOp",EDGE,"E25.11")])]})})});
            var Q41;
            Q41=makeQuery(id+"F12.boolean.opBoolean","SPLIT",BODY,{"disambiguationData":[OD(20.0)],"derivedFrom":makeQuery(id+"F10.boolean.opBoolean","SPLIT",BODY,{"disambiguationData":[OD(0.0)],"derivedFrom":makeQuery(id+"F4.opExtrude","SWEPT_BODY",BODY,{"disambiguationData":[OSD([sQuery(id+"F3.wireOp",EDGE,"E25.0"),sQuery(id+"F3.wireOp",EDGE,"E25.1"),sQuery(id+"F3.wireOp",EDGE,"E25.2"),sQuery(id+"F3.wireOp",EDGE,"E25.3"),sQuery(id+"F3.wireOp",EDGE,"E25.4"),sQuery(id+"F3.wireOp",EDGE,"E25.5"),sQuery(id+"F3.wireOp",EDGE,"E25.6"),sQuery(id+"F3.wireOp",EDGE,"E25.7"),sQuery(id+"F3.wireOp",EDGE,"E25.8"),sQuery(id+"F3.wireOp",EDGE,"E25.9"),sQuery(id+"F3.wireOp",EDGE,"E25.10"),sQuery(id+"F3.wireOp",EDGE,"E25.11")])]})})});
            var Q42;
            Q42=makeQuery(id+"F12.boolean.opBoolean","SPLIT",BODY,{"disambiguationData":[OD(21.0)],"derivedFrom":makeQuery(id+"F10.boolean.opBoolean","SPLIT",BODY,{"disambiguationData":[OD(0.0)],"derivedFrom":makeQuery(id+"F4.opExtrude","SWEPT_BODY",BODY,{"disambiguationData":[OSD([sQuery(id+"F3.wireOp",EDGE,"E25.0"),sQuery(id+"F3.wireOp",EDGE,"E25.1"),sQuery(id+"F3.wireOp",EDGE,"E25.2"),sQuery(id+"F3.wireOp",EDGE,"E25.3"),sQuery(id+"F3.wireOp",EDGE,"E25.4"),sQuery(id+"F3.wireOp",EDGE,"E25.5"),sQuery(id+"F3.wireOp",EDGE,"E25.6"),sQuery(id+"F3.wireOp",EDGE,"E25.7"),sQuery(id+"F3.wireOp",EDGE,"E25.8"),sQuery(id+"F3.wireOp",EDGE,"E25.9"),sQuery(id+"F3.wireOp",EDGE,"E25.10"),sQuery(id+"F3.wireOp",EDGE,"E25.11")])]})})});
            var Q43;
            Q43=makeQuery(id+"F12.boolean.opBoolean","SPLIT",BODY,{"disambiguationData":[OD(22.0)],"derivedFrom":makeQuery(id+"F10.boolean.opBoolean","SPLIT",BODY,{"disambiguationData":[OD(0.0)],"derivedFrom":makeQuery(id+"F4.opExtrude","SWEPT_BODY",BODY,{"disambiguationData":[OSD([sQuery(id+"F3.wireOp",EDGE,"E25.0"),sQuery(id+"F3.wireOp",EDGE,"E25.1"),sQuery(id+"F3.wireOp",EDGE,"E25.2"),sQuery(id+"F3.wireOp",EDGE,"E25.3"),sQuery(id+"F3.wireOp",EDGE,"E25.4"),sQuery(id+"F3.wireOp",EDGE,"E25.5"),sQuery(id+"F3.wireOp",EDGE,"E25.6"),sQuery(id+"F3.wireOp",EDGE,"E25.7"),sQuery(id+"F3.wireOp",EDGE,"E25.8"),sQuery(id+"F3.wireOp",EDGE,"E25.9"),sQuery(id+"F3.wireOp",EDGE,"E25.10"),sQuery(id+"F3.wireOp",EDGE,"E25.11")])]})})});
            var Q44;
            Q44=makeQuery(id+"F12.boolean.opBoolean","SPLIT",BODY,{"disambiguationData":[OD(23.0)],"derivedFrom":makeQuery(id+"F10.boolean.opBoolean","SPLIT",BODY,{"disambiguationData":[OD(0.0)],"derivedFrom":makeQuery(id+"F4.opExtrude","SWEPT_BODY",BODY,{"disambiguationData":[OSD([sQuery(id+"F3.wireOp",EDGE,"E25.0"),sQuery(id+"F3.wireOp",EDGE,"E25.1"),sQuery(id+"F3.wireOp",EDGE,"E25.2"),sQuery(id+"F3.wireOp",EDGE,"E25.3"),sQuery(id+"F3.wireOp",EDGE,"E25.4"),sQuery(id+"F3.wireOp",EDGE,"E25.5"),sQuery(id+"F3.wireOp",EDGE,"E25.6"),sQuery(id+"F3.wireOp",EDGE,"E25.7"),sQuery(id+"F3.wireOp",EDGE,"E25.8"),sQuery(id+"F3.wireOp",EDGE,"E25.9"),sQuery(id+"F3.wireOp",EDGE,"E25.10"),sQuery(id+"F3.wireOp",EDGE,"E25.11")])]})})});
            var Q45;
            Q45=makeQuery(id+"F12.boolean.opBoolean","SPLIT",BODY,{"disambiguationData":[OD(24.0)],"derivedFrom":makeQuery(id+"F10.boolean.opBoolean","SPLIT",BODY,{"disambiguationData":[OD(0.0)],"derivedFrom":makeQuery(id+"F4.opExtrude","SWEPT_BODY",BODY,{"disambiguationData":[OSD([sQuery(id+"F3.wireOp",EDGE,"E25.0"),sQuery(id+"F3.wireOp",EDGE,"E25.1"),sQuery(id+"F3.wireOp",EDGE,"E25.2"),sQuery(id+"F3.wireOp",EDGE,"E25.3"),sQuery(id+"F3.wireOp",EDGE,"E25.4"),sQuery(id+"F3.wireOp",EDGE,"E25.5"),sQuery(id+"F3.wireOp",EDGE,"E25.6"),sQuery(id+"F3.wireOp",EDGE,"E25.7"),sQuery(id+"F3.wireOp",EDGE,"E25.8"),sQuery(id+"F3.wireOp",EDGE,"E25.9"),sQuery(id+"F3.wireOp",EDGE,"E25.10"),sQuery(id+"F3.wireOp",EDGE,"E25.11")])]})})});
            var Q46;
            Q46=makeQuery(id+"F12.boolean.opBoolean","SPLIT",BODY,{"disambiguationData":[OD(25.0)],"derivedFrom":makeQuery(id+"F10.boolean.opBoolean","SPLIT",BODY,{"disambiguationData":[OD(0.0)],"derivedFrom":makeQuery(id+"F4.opExtrude","SWEPT_BODY",BODY,{"disambiguationData":[OSD([sQuery(id+"F3.wireOp",EDGE,"E25.0"),sQuery(id+"F3.wireOp",EDGE,"E25.1"),sQuery(id+"F3.wireOp",EDGE,"E25.2"),sQuery(id+"F3.wireOp",EDGE,"E25.3"),sQuery(id+"F3.wireOp",EDGE,"E25.4"),sQuery(id+"F3.wireOp",EDGE,"E25.5"),sQuery(id+"F3.wireOp",EDGE,"E25.6"),sQuery(id+"F3.wireOp",EDGE,"E25.7"),sQuery(id+"F3.wireOp",EDGE,"E25.8"),sQuery(id+"F3.wireOp",EDGE,"E25.9"),sQuery(id+"F3.wireOp",EDGE,"E25.10"),sQuery(id+"F3.wireOp",EDGE,"E25.11")])]})})});
            var Q47;
            Q47=makeQuery(id+"F12.boolean.opBoolean","SPLIT",BODY,{"disambiguationData":[OD(26.0)],"derivedFrom":makeQuery(id+"F10.boolean.opBoolean","SPLIT",BODY,{"disambiguationData":[OD(0.0)],"derivedFrom":makeQuery(id+"F4.opExtrude","SWEPT_BODY",BODY,{"disambiguationData":[OSD([sQuery(id+"F3.wireOp",EDGE,"E25.0"),sQuery(id+"F3.wireOp",EDGE,"E25.1"),sQuery(id+"F3.wireOp",EDGE,"E25.2"),sQuery(id+"F3.wireOp",EDGE,"E25.3"),sQuery(id+"F3.wireOp",EDGE,"E25.4"),sQuery(id+"F3.wireOp",EDGE,"E25.5"),sQuery(id+"F3.wireOp",EDGE,"E25.6"),sQuery(id+"F3.wireOp",EDGE,"E25.7"),sQuery(id+"F3.wireOp",EDGE,"E25.8"),sQuery(id+"F3.wireOp",EDGE,"E25.9"),sQuery(id+"F3.wireOp",EDGE,"E25.10"),sQuery(id+"F3.wireOp",EDGE,"E25.11")])]})})});
            var Q48;
            Q48=makeQuery(id+"F12.boolean.opBoolean","SPLIT",BODY,{"disambiguationData":[OD(27.0)],"derivedFrom":makeQuery(id+"F10.boolean.opBoolean","SPLIT",BODY,{"disambiguationData":[OD(0.0)],"derivedFrom":makeQuery(id+"F4.opExtrude","SWEPT_BODY",BODY,{"disambiguationData":[OSD([sQuery(id+"F3.wireOp",EDGE,"E25.0"),sQuery(id+"F3.wireOp",EDGE,"E25.1"),sQuery(id+"F3.wireOp",EDGE,"E25.2"),sQuery(id+"F3.wireOp",EDGE,"E25.3"),sQuery(id+"F3.wireOp",EDGE,"E25.4"),sQuery(id+"F3.wireOp",EDGE,"E25.5"),sQuery(id+"F3.wireOp",EDGE,"E25.6"),sQuery(id+"F3.wireOp",EDGE,"E25.7"),sQuery(id+"F3.wireOp",EDGE,"E25.8"),sQuery(id+"F3.wireOp",EDGE,"E25.9"),sQuery(id+"F3.wireOp",EDGE,"E25.10"),sQuery(id+"F3.wireOp",EDGE,"E25.11")])]})})});
            var Q49;
            Q49=makeQuery(id+"F12.boolean.opBoolean","SPLIT",BODY,{"disambiguationData":[OD(28.0)],"derivedFrom":makeQuery(id+"F10.boolean.opBoolean","SPLIT",BODY,{"disambiguationData":[OD(0.0)],"derivedFrom":makeQuery(id+"F4.opExtrude","SWEPT_BODY",BODY,{"disambiguationData":[OSD([sQuery(id+"F3.wireOp",EDGE,"E25.0"),sQuery(id+"F3.wireOp",EDGE,"E25.1"),sQuery(id+"F3.wireOp",EDGE,"E25.2"),sQuery(id+"F3.wireOp",EDGE,"E25.3"),sQuery(id+"F3.wireOp",EDGE,"E25.4"),sQuery(id+"F3.wireOp",EDGE,"E25.5"),sQuery(id+"F3.wireOp",EDGE,"E25.6"),sQuery(id+"F3.wireOp",EDGE,"E25.7"),sQuery(id+"F3.wireOp",EDGE,"E25.8"),sQuery(id+"F3.wireOp",EDGE,"E25.9"),sQuery(id+"F3.wireOp",EDGE,"E25.10"),sQuery(id+"F3.wireOp",EDGE,"E25.11")])]})})});
            var Q50;
            Q50=makeQuery(id+"F12.boolean.opBoolean","SPLIT",BODY,{"disambiguationData":[OD(29.0)],"derivedFrom":makeQuery(id+"F10.boolean.opBoolean","SPLIT",BODY,{"disambiguationData":[OD(0.0)],"derivedFrom":makeQuery(id+"F4.opExtrude","SWEPT_BODY",BODY,{"disambiguationData":[OSD([sQuery(id+"F3.wireOp",EDGE,"E25.0"),sQuery(id+"F3.wireOp",EDGE,"E25.1"),sQuery(id+"F3.wireOp",EDGE,"E25.2"),sQuery(id+"F3.wireOp",EDGE,"E25.3"),sQuery(id+"F3.wireOp",EDGE,"E25.4"),sQuery(id+"F3.wireOp",EDGE,"E25.5"),sQuery(id+"F3.wireOp",EDGE,"E25.6"),sQuery(id+"F3.wireOp",EDGE,"E25.7"),sQuery(id+"F3.wireOp",EDGE,"E25.8"),sQuery(id+"F3.wireOp",EDGE,"E25.9"),sQuery(id+"F3.wireOp",EDGE,"E25.10"),sQuery(id+"F3.wireOp",EDGE,"E25.11")])]})})});
            var Q51;
            Q51=makeQuery(id+"F12.boolean.opBoolean","SPLIT",BODY,{"disambiguationData":[OD(30.0)],"derivedFrom":makeQuery(id+"F10.boolean.opBoolean","SPLIT",BODY,{"disambiguationData":[OD(0.0)],"derivedFrom":makeQuery(id+"F4.opExtrude","SWEPT_BODY",BODY,{"disambiguationData":[OSD([sQuery(id+"F3.wireOp",EDGE,"E25.0"),sQuery(id+"F3.wireOp",EDGE,"E25.1"),sQuery(id+"F3.wireOp",EDGE,"E25.2"),sQuery(id+"F3.wireOp",EDGE,"E25.3"),sQuery(id+"F3.wireOp",EDGE,"E25.4"),sQuery(id+"F3.wireOp",EDGE,"E25.5"),sQuery(id+"F3.wireOp",EDGE,"E25.6"),sQuery(id+"F3.wireOp",EDGE,"E25.7"),sQuery(id+"F3.wireOp",EDGE,"E25.8"),sQuery(id+"F3.wireOp",EDGE,"E25.9"),sQuery(id+"F3.wireOp",EDGE,"E25.10"),sQuery(id+"F3.wireOp",EDGE,"E25.11")])]})})});
            var Q52;
            Q52=makeQuery(id+"F12.boolean.opBoolean","SPLIT",BODY,{"disambiguationData":[OD(31.0)],"derivedFrom":makeQuery(id+"F10.boolean.opBoolean","SPLIT",BODY,{"disambiguationData":[OD(0.0)],"derivedFrom":makeQuery(id+"F4.opExtrude","SWEPT_BODY",BODY,{"disambiguationData":[OSD([sQuery(id+"F3.wireOp",EDGE,"E25.0"),sQuery(id+"F3.wireOp",EDGE,"E25.1"),sQuery(id+"F3.wireOp",EDGE,"E25.2"),sQuery(id+"F3.wireOp",EDGE,"E25.3"),sQuery(id+"F3.wireOp",EDGE,"E25.4"),sQuery(id+"F3.wireOp",EDGE,"E25.5"),sQuery(id+"F3.wireOp",EDGE,"E25.6"),sQuery(id+"F3.wireOp",EDGE,"E25.7"),sQuery(id+"F3.wireOp",EDGE,"E25.8"),sQuery(id+"F3.wireOp",EDGE,"E25.9"),sQuery(id+"F3.wireOp",EDGE,"E25.10"),sQuery(id+"F3.wireOp",EDGE,"E25.11")])]})})});
            var Q53;
            Q53=makeQuery(id+"F12.boolean.opBoolean","SPLIT",BODY,{"disambiguationData":[OD(32.0)],"derivedFrom":makeQuery(id+"F10.boolean.opBoolean","SPLIT",BODY,{"disambiguationData":[OD(0.0)],"derivedFrom":makeQuery(id+"F4.opExtrude","SWEPT_BODY",BODY,{"disambiguationData":[OSD([sQuery(id+"F3.wireOp",EDGE,"E25.0"),sQuery(id+"F3.wireOp",EDGE,"E25.1"),sQuery(id+"F3.wireOp",EDGE,"E25.2"),sQuery(id+"F3.wireOp",EDGE,"E25.3"),sQuery(id+"F3.wireOp",EDGE,"E25.4"),sQuery(id+"F3.wireOp",EDGE,"E25.5"),sQuery(id+"F3.wireOp",EDGE,"E25.6"),sQuery(id+"F3.wireOp",EDGE,"E25.7"),sQuery(id+"F3.wireOp",EDGE,"E25.8"),sQuery(id+"F3.wireOp",EDGE,"E25.9"),sQuery(id+"F3.wireOp",EDGE,"E25.10"),sQuery(id+"F3.wireOp",EDGE,"E25.11")])]})})});
            var Q54;
            Q54=makeQuery(id+"F12.boolean.opBoolean","SPLIT",BODY,{"disambiguationData":[OD(33.0)],"derivedFrom":makeQuery(id+"F10.boolean.opBoolean","SPLIT",BODY,{"disambiguationData":[OD(0.0)],"derivedFrom":makeQuery(id+"F4.opExtrude","SWEPT_BODY",BODY,{"disambiguationData":[OSD([sQuery(id+"F3.wireOp",EDGE,"E25.0"),sQuery(id+"F3.wireOp",EDGE,"E25.1"),sQuery(id+"F3.wireOp",EDGE,"E25.2"),sQuery(id+"F3.wireOp",EDGE,"E25.3"),sQuery(id+"F3.wireOp",EDGE,"E25.4"),sQuery(id+"F3.wireOp",EDGE,"E25.5"),sQuery(id+"F3.wireOp",EDGE,"E25.6"),sQuery(id+"F3.wireOp",EDGE,"E25.7"),sQuery(id+"F3.wireOp",EDGE,"E25.8"),sQuery(id+"F3.wireOp",EDGE,"E25.9"),sQuery(id+"F3.wireOp",EDGE,"E25.10"),sQuery(id+"F3.wireOp",EDGE,"E25.11")])]})})});
            var Q55;
            Q55=makeQuery(id+"F12.boolean.opBoolean","SPLIT",BODY,{"disambiguationData":[OD(34.0)],"derivedFrom":makeQuery(id+"F10.boolean.opBoolean","SPLIT",BODY,{"disambiguationData":[OD(0.0)],"derivedFrom":makeQuery(id+"F4.opExtrude","SWEPT_BODY",BODY,{"disambiguationData":[OSD([sQuery(id+"F3.wireOp",EDGE,"E25.0"),sQuery(id+"F3.wireOp",EDGE,"E25.1"),sQuery(id+"F3.wireOp",EDGE,"E25.2"),sQuery(id+"F3.wireOp",EDGE,"E25.3"),sQuery(id+"F3.wireOp",EDGE,"E25.4"),sQuery(id+"F3.wireOp",EDGE,"E25.5"),sQuery(id+"F3.wireOp",EDGE,"E25.6"),sQuery(id+"F3.wireOp",EDGE,"E25.7"),sQuery(id+"F3.wireOp",EDGE,"E25.8"),sQuery(id+"F3.wireOp",EDGE,"E25.9"),sQuery(id+"F3.wireOp",EDGE,"E25.10"),sQuery(id+"F3.wireOp",EDGE,"E25.11")])]})})});
            var Q56;
            Q56=makeQuery(id+"F12.boolean.opBoolean","SPLIT",BODY,{"disambiguationData":[OD(35.0)],"derivedFrom":makeQuery(id+"F10.boolean.opBoolean","SPLIT",BODY,{"disambiguationData":[OD(0.0)],"derivedFrom":makeQuery(id+"F4.opExtrude","SWEPT_BODY",BODY,{"disambiguationData":[OSD([sQuery(id+"F3.wireOp",EDGE,"E25.0"),sQuery(id+"F3.wireOp",EDGE,"E25.1"),sQuery(id+"F3.wireOp",EDGE,"E25.2"),sQuery(id+"F3.wireOp",EDGE,"E25.3"),sQuery(id+"F3.wireOp",EDGE,"E25.4"),sQuery(id+"F3.wireOp",EDGE,"E25.5"),sQuery(id+"F3.wireOp",EDGE,"E25.6"),sQuery(id+"F3.wireOp",EDGE,"E25.7"),sQuery(id+"F3.wireOp",EDGE,"E25.8"),sQuery(id+"F3.wireOp",EDGE,"E25.9"),sQuery(id+"F3.wireOp",EDGE,"E25.10"),sQuery(id+"F3.wireOp",EDGE,"E25.11")])]})})});
            var Q57;
            Q57=makeQuery(id+"F12.boolean.opBoolean","SPLIT",BODY,{"disambiguationData":[OD(36.0)],"derivedFrom":makeQuery(id+"F10.boolean.opBoolean","SPLIT",BODY,{"disambiguationData":[OD(0.0)],"derivedFrom":makeQuery(id+"F4.opExtrude","SWEPT_BODY",BODY,{"disambiguationData":[OSD([sQuery(id+"F3.wireOp",EDGE,"E25.0"),sQuery(id+"F3.wireOp",EDGE,"E25.1"),sQuery(id+"F3.wireOp",EDGE,"E25.2"),sQuery(id+"F3.wireOp",EDGE,"E25.3"),sQuery(id+"F3.wireOp",EDGE,"E25.4"),sQuery(id+"F3.wireOp",EDGE,"E25.5"),sQuery(id+"F3.wireOp",EDGE,"E25.6"),sQuery(id+"F3.wireOp",EDGE,"E25.7"),sQuery(id+"F3.wireOp",EDGE,"E25.8"),sQuery(id+"F3.wireOp",EDGE,"E25.9"),sQuery(id+"F3.wireOp",EDGE,"E25.10"),sQuery(id+"F3.wireOp",EDGE,"E25.11")])]})})});
            var Q58;
            Q58=makeQuery(id+"F12.boolean.opBoolean","SPLIT",BODY,{"disambiguationData":[OD(37.0)],"derivedFrom":makeQuery(id+"F10.boolean.opBoolean","SPLIT",BODY,{"disambiguationData":[OD(0.0)],"derivedFrom":makeQuery(id+"F4.opExtrude","SWEPT_BODY",BODY,{"disambiguationData":[OSD([sQuery(id+"F3.wireOp",EDGE,"E25.0"),sQuery(id+"F3.wireOp",EDGE,"E25.1"),sQuery(id+"F3.wireOp",EDGE,"E25.2"),sQuery(id+"F3.wireOp",EDGE,"E25.3"),sQuery(id+"F3.wireOp",EDGE,"E25.4"),sQuery(id+"F3.wireOp",EDGE,"E25.5"),sQuery(id+"F3.wireOp",EDGE,"E25.6"),sQuery(id+"F3.wireOp",EDGE,"E25.7"),sQuery(id+"F3.wireOp",EDGE,"E25.8"),sQuery(id+"F3.wireOp",EDGE,"E25.9"),sQuery(id+"F3.wireOp",EDGE,"E25.10"),sQuery(id+"F3.wireOp",EDGE,"E25.11")])]})})});
            var Q59;
            Q59=makeQuery(id+"F12.boolean.opBoolean","SPLIT",BODY,{"disambiguationData":[OD(38.0)],"derivedFrom":makeQuery(id+"F10.boolean.opBoolean","SPLIT",BODY,{"disambiguationData":[OD(0.0)],"derivedFrom":makeQuery(id+"F4.opExtrude","SWEPT_BODY",BODY,{"disambiguationData":[OSD([sQuery(id+"F3.wireOp",EDGE,"E25.0"),sQuery(id+"F3.wireOp",EDGE,"E25.1"),sQuery(id+"F3.wireOp",EDGE,"E25.2"),sQuery(id+"F3.wireOp",EDGE,"E25.3"),sQuery(id+"F3.wireOp",EDGE,"E25.4"),sQuery(id+"F3.wireOp",EDGE,"E25.5"),sQuery(id+"F3.wireOp",EDGE,"E25.6"),sQuery(id+"F3.wireOp",EDGE,"E25.7"),sQuery(id+"F3.wireOp",EDGE,"E25.8"),sQuery(id+"F3.wireOp",EDGE,"E25.9"),sQuery(id+"F3.wireOp",EDGE,"E25.10"),sQuery(id+"F3.wireOp",EDGE,"E25.11")])]})})});
            var Q60;
            Q60=makeQuery(id+"F12.boolean.opBoolean","SPLIT",BODY,{"disambiguationData":[OD(39.0)],"derivedFrom":makeQuery(id+"F10.boolean.opBoolean","SPLIT",BODY,{"disambiguationData":[OD(0.0)],"derivedFrom":makeQuery(id+"F4.opExtrude","SWEPT_BODY",BODY,{"disambiguationData":[OSD([sQuery(id+"F3.wireOp",EDGE,"E25.0"),sQuery(id+"F3.wireOp",EDGE,"E25.1"),sQuery(id+"F3.wireOp",EDGE,"E25.2"),sQuery(id+"F3.wireOp",EDGE,"E25.3"),sQuery(id+"F3.wireOp",EDGE,"E25.4"),sQuery(id+"F3.wireOp",EDGE,"E25.5"),sQuery(id+"F3.wireOp",EDGE,"E25.6"),sQuery(id+"F3.wireOp",EDGE,"E25.7"),sQuery(id+"F3.wireOp",EDGE,"E25.8"),sQuery(id+"F3.wireOp",EDGE,"E25.9"),sQuery(id+"F3.wireOp",EDGE,"E25.10"),sQuery(id+"F3.wireOp",EDGE,"E25.11")])]})})});
            var Q61;
            Q61=makeQuery(id+"F12.boolean.opBoolean","SPLIT",BODY,{"disambiguationData":[OD(40.0)],"derivedFrom":makeQuery(id+"F10.boolean.opBoolean","SPLIT",BODY,{"disambiguationData":[OD(0.0)],"derivedFrom":makeQuery(id+"F4.opExtrude","SWEPT_BODY",BODY,{"disambiguationData":[OSD([sQuery(id+"F3.wireOp",EDGE,"E25.0"),sQuery(id+"F3.wireOp",EDGE,"E25.1"),sQuery(id+"F3.wireOp",EDGE,"E25.2"),sQuery(id+"F3.wireOp",EDGE,"E25.3"),sQuery(id+"F3.wireOp",EDGE,"E25.4"),sQuery(id+"F3.wireOp",EDGE,"E25.5"),sQuery(id+"F3.wireOp",EDGE,"E25.6"),sQuery(id+"F3.wireOp",EDGE,"E25.7"),sQuery(id+"F3.wireOp",EDGE,"E25.8"),sQuery(id+"F3.wireOp",EDGE,"E25.9"),sQuery(id+"F3.wireOp",EDGE,"E25.10"),sQuery(id+"F3.wireOp",EDGE,"E25.11")])]})})});
            var Q62;
            Q62=makeQuery(id+"F12.boolean.opBoolean","SPLIT",BODY,{"disambiguationData":[OD(41.0)],"derivedFrom":makeQuery(id+"F10.boolean.opBoolean","SPLIT",BODY,{"disambiguationData":[OD(0.0)],"derivedFrom":makeQuery(id+"F4.opExtrude","SWEPT_BODY",BODY,{"disambiguationData":[OSD([sQuery(id+"F3.wireOp",EDGE,"E25.0"),sQuery(id+"F3.wireOp",EDGE,"E25.1"),sQuery(id+"F3.wireOp",EDGE,"E25.2"),sQuery(id+"F3.wireOp",EDGE,"E25.3"),sQuery(id+"F3.wireOp",EDGE,"E25.4"),sQuery(id+"F3.wireOp",EDGE,"E25.5"),sQuery(id+"F3.wireOp",EDGE,"E25.6"),sQuery(id+"F3.wireOp",EDGE,"E25.7"),sQuery(id+"F3.wireOp",EDGE,"E25.8"),sQuery(id+"F3.wireOp",EDGE,"E25.9"),sQuery(id+"F3.wireOp",EDGE,"E25.10"),sQuery(id+"F3.wireOp",EDGE,"E25.11")])]})})});
            var Q63;
            Q63=makeQuery(id+"F12.boolean.opBoolean","SPLIT",BODY,{"disambiguationData":[OD(42.0)],"derivedFrom":makeQuery(id+"F10.boolean.opBoolean","SPLIT",BODY,{"disambiguationData":[OD(0.0)],"derivedFrom":makeQuery(id+"F4.opExtrude","SWEPT_BODY",BODY,{"disambiguationData":[OSD([sQuery(id+"F3.wireOp",EDGE,"E25.0"),sQuery(id+"F3.wireOp",EDGE,"E25.1"),sQuery(id+"F3.wireOp",EDGE,"E25.2"),sQuery(id+"F3.wireOp",EDGE,"E25.3"),sQuery(id+"F3.wireOp",EDGE,"E25.4"),sQuery(id+"F3.wireOp",EDGE,"E25.5"),sQuery(id+"F3.wireOp",EDGE,"E25.6"),sQuery(id+"F3.wireOp",EDGE,"E25.7"),sQuery(id+"F3.wireOp",EDGE,"E25.8"),sQuery(id+"F3.wireOp",EDGE,"E25.9"),sQuery(id+"F3.wireOp",EDGE,"E25.10"),sQuery(id+"F3.wireOp",EDGE,"E25.11")])]})})});
            var Q64;
            Q64=makeQuery(id+"F12.boolean.opBoolean","SPLIT",BODY,{"disambiguationData":[OD(43.0)],"derivedFrom":makeQuery(id+"F10.boolean.opBoolean","SPLIT",BODY,{"disambiguationData":[OD(0.0)],"derivedFrom":makeQuery(id+"F4.opExtrude","SWEPT_BODY",BODY,{"disambiguationData":[OSD([sQuery(id+"F3.wireOp",EDGE,"E25.0"),sQuery(id+"F3.wireOp",EDGE,"E25.1"),sQuery(id+"F3.wireOp",EDGE,"E25.2"),sQuery(id+"F3.wireOp",EDGE,"E25.3"),sQuery(id+"F3.wireOp",EDGE,"E25.4"),sQuery(id+"F3.wireOp",EDGE,"E25.5"),sQuery(id+"F3.wireOp",EDGE,"E25.6"),sQuery(id+"F3.wireOp",EDGE,"E25.7"),sQuery(id+"F3.wireOp",EDGE,"E25.8"),sQuery(id+"F3.wireOp",EDGE,"E25.9"),sQuery(id+"F3.wireOp",EDGE,"E25.10"),sQuery(id+"F3.wireOp",EDGE,"E25.11")])]})})});
            var Q65;
            Q65=makeQuery(id+"F12.boolean.opBoolean","SPLIT",BODY,{"disambiguationData":[OD(44.0)],"derivedFrom":makeQuery(id+"F10.boolean.opBoolean","SPLIT",BODY,{"disambiguationData":[OD(0.0)],"derivedFrom":makeQuery(id+"F4.opExtrude","SWEPT_BODY",BODY,{"disambiguationData":[OSD([sQuery(id+"F3.wireOp",EDGE,"E25.0"),sQuery(id+"F3.wireOp",EDGE,"E25.1"),sQuery(id+"F3.wireOp",EDGE,"E25.2"),sQuery(id+"F3.wireOp",EDGE,"E25.3"),sQuery(id+"F3.wireOp",EDGE,"E25.4"),sQuery(id+"F3.wireOp",EDGE,"E25.5"),sQuery(id+"F3.wireOp",EDGE,"E25.6"),sQuery(id+"F3.wireOp",EDGE,"E25.7"),sQuery(id+"F3.wireOp",EDGE,"E25.8"),sQuery(id+"F3.wireOp",EDGE,"E25.9"),sQuery(id+"F3.wireOp",EDGE,"E25.10"),sQuery(id+"F3.wireOp",EDGE,"E25.11")])]})})});
            var Q66;
            Q66=makeQuery(id+"F12.boolean.opBoolean","SPLIT",BODY,{"disambiguationData":[OD(45.0)],"derivedFrom":makeQuery(id+"F10.boolean.opBoolean","SPLIT",BODY,{"disambiguationData":[OD(0.0)],"derivedFrom":makeQuery(id+"F4.opExtrude","SWEPT_BODY",BODY,{"disambiguationData":[OSD([sQuery(id+"F3.wireOp",EDGE,"E25.0"),sQuery(id+"F3.wireOp",EDGE,"E25.1"),sQuery(id+"F3.wireOp",EDGE,"E25.2"),sQuery(id+"F3.wireOp",EDGE,"E25.3"),sQuery(id+"F3.wireOp",EDGE,"E25.4"),sQuery(id+"F3.wireOp",EDGE,"E25.5"),sQuery(id+"F3.wireOp",EDGE,"E25.6"),sQuery(id+"F3.wireOp",EDGE,"E25.7"),sQuery(id+"F3.wireOp",EDGE,"E25.8"),sQuery(id+"F3.wireOp",EDGE,"E25.9"),sQuery(id+"F3.wireOp",EDGE,"E25.10"),sQuery(id+"F3.wireOp",EDGE,"E25.11")])]})})});
            var Q67;
            Q67=makeQuery(id+"F12.boolean.opBoolean","SPLIT",BODY,{"disambiguationData":[OD(46.0)],"derivedFrom":makeQuery(id+"F10.boolean.opBoolean","SPLIT",BODY,{"disambiguationData":[OD(0.0)],"derivedFrom":makeQuery(id+"F4.opExtrude","SWEPT_BODY",BODY,{"disambiguationData":[OSD([sQuery(id+"F3.wireOp",EDGE,"E25.0"),sQuery(id+"F3.wireOp",EDGE,"E25.1"),sQuery(id+"F3.wireOp",EDGE,"E25.2"),sQuery(id+"F3.wireOp",EDGE,"E25.3"),sQuery(id+"F3.wireOp",EDGE,"E25.4"),sQuery(id+"F3.wireOp",EDGE,"E25.5"),sQuery(id+"F3.wireOp",EDGE,"E25.6"),sQuery(id+"F3.wireOp",EDGE,"E25.7"),sQuery(id+"F3.wireOp",EDGE,"E25.8"),sQuery(id+"F3.wireOp",EDGE,"E25.9"),sQuery(id+"F3.wireOp",EDGE,"E25.10"),sQuery(id+"F3.wireOp",EDGE,"E25.11")])]})})});
            var Q68;
            Q68=makeQuery(id+"F12.boolean.opBoolean","SPLIT",BODY,{"disambiguationData":[OD(47.0)],"derivedFrom":makeQuery(id+"F10.boolean.opBoolean","SPLIT",BODY,{"disambiguationData":[OD(0.0)],"derivedFrom":makeQuery(id+"F4.opExtrude","SWEPT_BODY",BODY,{"disambiguationData":[OSD([sQuery(id+"F3.wireOp",EDGE,"E25.0"),sQuery(id+"F3.wireOp",EDGE,"E25.1"),sQuery(id+"F3.wireOp",EDGE,"E25.2"),sQuery(id+"F3.wireOp",EDGE,"E25.3"),sQuery(id+"F3.wireOp",EDGE,"E25.4"),sQuery(id+"F3.wireOp",EDGE,"E25.5"),sQuery(id+"F3.wireOp",EDGE,"E25.6"),sQuery(id+"F3.wireOp",EDGE,"E25.7"),sQuery(id+"F3.wireOp",EDGE,"E25.8"),sQuery(id+"F3.wireOp",EDGE,"E25.9"),sQuery(id+"F3.wireOp",EDGE,"E25.10"),sQuery(id+"F3.wireOp",EDGE,"E25.11")])]})})});
            var Q69;
            Q69=makeQuery(id+"F12.boolean.opBoolean","SPLIT",BODY,{"disambiguationData":[OD(48.0)],"derivedFrom":makeQuery(id+"F10.boolean.opBoolean","SPLIT",BODY,{"disambiguationData":[OD(0.0)],"derivedFrom":makeQuery(id+"F4.opExtrude","SWEPT_BODY",BODY,{"disambiguationData":[OSD([sQuery(id+"F3.wireOp",EDGE,"E25.0"),sQuery(id+"F3.wireOp",EDGE,"E25.1"),sQuery(id+"F3.wireOp",EDGE,"E25.2"),sQuery(id+"F3.wireOp",EDGE,"E25.3"),sQuery(id+"F3.wireOp",EDGE,"E25.4"),sQuery(id+"F3.wireOp",EDGE,"E25.5"),sQuery(id+"F3.wireOp",EDGE,"E25.6"),sQuery(id+"F3.wireOp",EDGE,"E25.7"),sQuery(id+"F3.wireOp",EDGE,"E25.8"),sQuery(id+"F3.wireOp",EDGE,"E25.9"),sQuery(id+"F3.wireOp",EDGE,"E25.10"),sQuery(id+"F3.wireOp",EDGE,"E25.11")])]})})});
            var Q70;
            Q70=makeQuery(id+"F12.boolean.opBoolean","SPLIT",BODY,{"disambiguationData":[OD(49.0)],"derivedFrom":makeQuery(id+"F10.boolean.opBoolean","SPLIT",BODY,{"disambiguationData":[OD(0.0)],"derivedFrom":makeQuery(id+"F4.opExtrude","SWEPT_BODY",BODY,{"disambiguationData":[OSD([sQuery(id+"F3.wireOp",EDGE,"E25.0"),sQuery(id+"F3.wireOp",EDGE,"E25.1"),sQuery(id+"F3.wireOp",EDGE,"E25.2"),sQuery(id+"F3.wireOp",EDGE,"E25.3"),sQuery(id+"F3.wireOp",EDGE,"E25.4"),sQuery(id+"F3.wireOp",EDGE,"E25.5"),sQuery(id+"F3.wireOp",EDGE,"E25.6"),sQuery(id+"F3.wireOp",EDGE,"E25.7"),sQuery(id+"F3.wireOp",EDGE,"E25.8"),sQuery(id+"F3.wireOp",EDGE,"E25.9"),sQuery(id+"F3.wireOp",EDGE,"E25.10"),sQuery(id+"F3.wireOp",EDGE,"E25.11")])]})})});
            var Q71;
            Q71=makeQuery(id+"F12.boolean.opBoolean","SPLIT",BODY,{"disambiguationData":[OD(50.0)],"derivedFrom":makeQuery(id+"F10.boolean.opBoolean","SPLIT",BODY,{"disambiguationData":[OD(0.0)],"derivedFrom":makeQuery(id+"F4.opExtrude","SWEPT_BODY",BODY,{"disambiguationData":[OSD([sQuery(id+"F3.wireOp",EDGE,"E25.0"),sQuery(id+"F3.wireOp",EDGE,"E25.1"),sQuery(id+"F3.wireOp",EDGE,"E25.2"),sQuery(id+"F3.wireOp",EDGE,"E25.3"),sQuery(id+"F3.wireOp",EDGE,"E25.4"),sQuery(id+"F3.wireOp",EDGE,"E25.5"),sQuery(id+"F3.wireOp",EDGE,"E25.6"),sQuery(id+"F3.wireOp",EDGE,"E25.7"),sQuery(id+"F3.wireOp",EDGE,"E25.8"),sQuery(id+"F3.wireOp",EDGE,"E25.9"),sQuery(id+"F3.wireOp",EDGE,"E25.10"),sQuery(id+"F3.wireOp",EDGE,"E25.11")])]})})});
            var Q72;
            Q72=makeQuery(id+"F12.boolean.opBoolean","SPLIT",BODY,{"disambiguationData":[OD(51.0)],"derivedFrom":makeQuery(id+"F10.boolean.opBoolean","SPLIT",BODY,{"disambiguationData":[OD(0.0)],"derivedFrom":makeQuery(id+"F4.opExtrude","SWEPT_BODY",BODY,{"disambiguationData":[OSD([sQuery(id+"F3.wireOp",EDGE,"E25.0"),sQuery(id+"F3.wireOp",EDGE,"E25.1"),sQuery(id+"F3.wireOp",EDGE,"E25.2"),sQuery(id+"F3.wireOp",EDGE,"E25.3"),sQuery(id+"F3.wireOp",EDGE,"E25.4"),sQuery(id+"F3.wireOp",EDGE,"E25.5"),sQuery(id+"F3.wireOp",EDGE,"E25.6"),sQuery(id+"F3.wireOp",EDGE,"E25.7"),sQuery(id+"F3.wireOp",EDGE,"E25.8"),sQuery(id+"F3.wireOp",EDGE,"E25.9"),sQuery(id+"F3.wireOp",EDGE,"E25.10"),sQuery(id+"F3.wireOp",EDGE,"E25.11")])]})})});
            var Q73;
            Q73=makeQuery(id+"F12.boolean.opBoolean","SPLIT",BODY,{"disambiguationData":[OD(52.0)],"derivedFrom":makeQuery(id+"F10.boolean.opBoolean","SPLIT",BODY,{"disambiguationData":[OD(0.0)],"derivedFrom":makeQuery(id+"F4.opExtrude","SWEPT_BODY",BODY,{"disambiguationData":[OSD([sQuery(id+"F3.wireOp",EDGE,"E25.0"),sQuery(id+"F3.wireOp",EDGE,"E25.1"),sQuery(id+"F3.wireOp",EDGE,"E25.2"),sQuery(id+"F3.wireOp",EDGE,"E25.3"),sQuery(id+"F3.wireOp",EDGE,"E25.4"),sQuery(id+"F3.wireOp",EDGE,"E25.5"),sQuery(id+"F3.wireOp",EDGE,"E25.6"),sQuery(id+"F3.wireOp",EDGE,"E25.7"),sQuery(id+"F3.wireOp",EDGE,"E25.8"),sQuery(id+"F3.wireOp",EDGE,"E25.9"),sQuery(id+"F3.wireOp",EDGE,"E25.10"),sQuery(id+"F3.wireOp",EDGE,"E25.11")])]})})});
            var Q74;
            Q74=makeQuery(id+"F12.boolean.opBoolean","SPLIT",BODY,{"disambiguationData":[OD(53.0)],"derivedFrom":makeQuery(id+"F10.boolean.opBoolean","SPLIT",BODY,{"disambiguationData":[OD(0.0)],"derivedFrom":makeQuery(id+"F4.opExtrude","SWEPT_BODY",BODY,{"disambiguationData":[OSD([sQuery(id+"F3.wireOp",EDGE,"E25.0"),sQuery(id+"F3.wireOp",EDGE,"E25.1"),sQuery(id+"F3.wireOp",EDGE,"E25.2"),sQuery(id+"F3.wireOp",EDGE,"E25.3"),sQuery(id+"F3.wireOp",EDGE,"E25.4"),sQuery(id+"F3.wireOp",EDGE,"E25.5"),sQuery(id+"F3.wireOp",EDGE,"E25.6"),sQuery(id+"F3.wireOp",EDGE,"E25.7"),sQuery(id+"F3.wireOp",EDGE,"E25.8"),sQuery(id+"F3.wireOp",EDGE,"E25.9"),sQuery(id+"F3.wireOp",EDGE,"E25.10"),sQuery(id+"F3.wireOp",EDGE,"E25.11")])]})})});
            var Q75;
            Q75=makeQuery(id+"F12.boolean.opBoolean","SPLIT",BODY,{"disambiguationData":[OD(54.0)],"derivedFrom":makeQuery(id+"F10.boolean.opBoolean","SPLIT",BODY,{"disambiguationData":[OD(0.0)],"derivedFrom":makeQuery(id+"F4.opExtrude","SWEPT_BODY",BODY,{"disambiguationData":[OSD([sQuery(id+"F3.wireOp",EDGE,"E25.0"),sQuery(id+"F3.wireOp",EDGE,"E25.1"),sQuery(id+"F3.wireOp",EDGE,"E25.2"),sQuery(id+"F3.wireOp",EDGE,"E25.3"),sQuery(id+"F3.wireOp",EDGE,"E25.4"),sQuery(id+"F3.wireOp",EDGE,"E25.5"),sQuery(id+"F3.wireOp",EDGE,"E25.6"),sQuery(id+"F3.wireOp",EDGE,"E25.7"),sQuery(id+"F3.wireOp",EDGE,"E25.8"),sQuery(id+"F3.wireOp",EDGE,"E25.9"),sQuery(id+"F3.wireOp",EDGE,"E25.10"),sQuery(id+"F3.wireOp",EDGE,"E25.11")])]})})});
            var Q76;
            Q76=makeQuery(id+"F12.boolean.opBoolean","SPLIT",BODY,{"disambiguationData":[OD(55.0)],"derivedFrom":makeQuery(id+"F10.boolean.opBoolean","SPLIT",BODY,{"disambiguationData":[OD(0.0)],"derivedFrom":makeQuery(id+"F4.opExtrude","SWEPT_BODY",BODY,{"disambiguationData":[OSD([sQuery(id+"F3.wireOp",EDGE,"E25.0"),sQuery(id+"F3.wireOp",EDGE,"E25.1"),sQuery(id+"F3.wireOp",EDGE,"E25.2"),sQuery(id+"F3.wireOp",EDGE,"E25.3"),sQuery(id+"F3.wireOp",EDGE,"E25.4"),sQuery(id+"F3.wireOp",EDGE,"E25.5"),sQuery(id+"F3.wireOp",EDGE,"E25.6"),sQuery(id+"F3.wireOp",EDGE,"E25.7"),sQuery(id+"F3.wireOp",EDGE,"E25.8"),sQuery(id+"F3.wireOp",EDGE,"E25.9"),sQuery(id+"F3.wireOp",EDGE,"E25.10"),sQuery(id+"F3.wireOp",EDGE,"E25.11")])]})})});
            var Q77;
            Q77=makeQuery(id+"F12.boolean.opBoolean","SPLIT",BODY,{"disambiguationData":[OD(56.0)],"derivedFrom":makeQuery(id+"F10.boolean.opBoolean","SPLIT",BODY,{"disambiguationData":[OD(0.0)],"derivedFrom":makeQuery(id+"F4.opExtrude","SWEPT_BODY",BODY,{"disambiguationData":[OSD([sQuery(id+"F3.wireOp",EDGE,"E25.0"),sQuery(id+"F3.wireOp",EDGE,"E25.1"),sQuery(id+"F3.wireOp",EDGE,"E25.2"),sQuery(id+"F3.wireOp",EDGE,"E25.3"),sQuery(id+"F3.wireOp",EDGE,"E25.4"),sQuery(id+"F3.wireOp",EDGE,"E25.5"),sQuery(id+"F3.wireOp",EDGE,"E25.6"),sQuery(id+"F3.wireOp",EDGE,"E25.7"),sQuery(id+"F3.wireOp",EDGE,"E25.8"),sQuery(id+"F3.wireOp",EDGE,"E25.9"),sQuery(id+"F3.wireOp",EDGE,"E25.10"),sQuery(id+"F3.wireOp",EDGE,"E25.11")])]})})});
            var Q78;
            Q78=makeQuery(id+"F12.boolean.opBoolean","SPLIT",BODY,{"disambiguationData":[OD(57.0)],"derivedFrom":makeQuery(id+"F10.boolean.opBoolean","SPLIT",BODY,{"disambiguationData":[OD(0.0)],"derivedFrom":makeQuery(id+"F4.opExtrude","SWEPT_BODY",BODY,{"disambiguationData":[OSD([sQuery(id+"F3.wireOp",EDGE,"E25.0"),sQuery(id+"F3.wireOp",EDGE,"E25.1"),sQuery(id+"F3.wireOp",EDGE,"E25.2"),sQuery(id+"F3.wireOp",EDGE,"E25.3"),sQuery(id+"F3.wireOp",EDGE,"E25.4"),sQuery(id+"F3.wireOp",EDGE,"E25.5"),sQuery(id+"F3.wireOp",EDGE,"E25.6"),sQuery(id+"F3.wireOp",EDGE,"E25.7"),sQuery(id+"F3.wireOp",EDGE,"E25.8"),sQuery(id+"F3.wireOp",EDGE,"E25.9"),sQuery(id+"F3.wireOp",EDGE,"E25.10"),sQuery(id+"F3.wireOp",EDGE,"E25.11")])]})})});
            var Q79;
            Q79=makeQuery(id+"F12.boolean.opBoolean","SPLIT",BODY,{"disambiguationData":[OD(58.0)],"derivedFrom":makeQuery(id+"F10.boolean.opBoolean","SPLIT",BODY,{"disambiguationData":[OD(0.0)],"derivedFrom":makeQuery(id+"F4.opExtrude","SWEPT_BODY",BODY,{"disambiguationData":[OSD([sQuery(id+"F3.wireOp",EDGE,"E25.0"),sQuery(id+"F3.wireOp",EDGE,"E25.1"),sQuery(id+"F3.wireOp",EDGE,"E25.2"),sQuery(id+"F3.wireOp",EDGE,"E25.3"),sQuery(id+"F3.wireOp",EDGE,"E25.4"),sQuery(id+"F3.wireOp",EDGE,"E25.5"),sQuery(id+"F3.wireOp",EDGE,"E25.6"),sQuery(id+"F3.wireOp",EDGE,"E25.7"),sQuery(id+"F3.wireOp",EDGE,"E25.8"),sQuery(id+"F3.wireOp",EDGE,"E25.9"),sQuery(id+"F3.wireOp",EDGE,"E25.10"),sQuery(id+"F3.wireOp",EDGE,"E25.11")])]})})});
            var Q80;
            Q80=makeQuery(id+"F12.boolean.opBoolean","SPLIT",BODY,{"disambiguationData":[OD(59.0)],"derivedFrom":makeQuery(id+"F10.boolean.opBoolean","SPLIT",BODY,{"disambiguationData":[OD(0.0)],"derivedFrom":makeQuery(id+"F4.opExtrude","SWEPT_BODY",BODY,{"disambiguationData":[OSD([sQuery(id+"F3.wireOp",EDGE,"E25.0"),sQuery(id+"F3.wireOp",EDGE,"E25.1"),sQuery(id+"F3.wireOp",EDGE,"E25.2"),sQuery(id+"F3.wireOp",EDGE,"E25.3"),sQuery(id+"F3.wireOp",EDGE,"E25.4"),sQuery(id+"F3.wireOp",EDGE,"E25.5"),sQuery(id+"F3.wireOp",EDGE,"E25.6"),sQuery(id+"F3.wireOp",EDGE,"E25.7"),sQuery(id+"F3.wireOp",EDGE,"E25.8"),sQuery(id+"F3.wireOp",EDGE,"E25.9"),sQuery(id+"F3.wireOp",EDGE,"E25.10"),sQuery(id+"F3.wireOp",EDGE,"E25.11")])]})})});
            var Q81;
            Q81=makeQuery(id+"F12.boolean.opBoolean","SPLIT",BODY,{"disambiguationData":[OD(60.0)],"derivedFrom":makeQuery(id+"F10.boolean.opBoolean","SPLIT",BODY,{"disambiguationData":[OD(0.0)],"derivedFrom":makeQuery(id+"F4.opExtrude","SWEPT_BODY",BODY,{"disambiguationData":[OSD([sQuery(id+"F3.wireOp",EDGE,"E25.0"),sQuery(id+"F3.wireOp",EDGE,"E25.1"),sQuery(id+"F3.wireOp",EDGE,"E25.2"),sQuery(id+"F3.wireOp",EDGE,"E25.3"),sQuery(id+"F3.wireOp",EDGE,"E25.4"),sQuery(id+"F3.wireOp",EDGE,"E25.5"),sQuery(id+"F3.wireOp",EDGE,"E25.6"),sQuery(id+"F3.wireOp",EDGE,"E25.7"),sQuery(id+"F3.wireOp",EDGE,"E25.8"),sQuery(id+"F3.wireOp",EDGE,"E25.9"),sQuery(id+"F3.wireOp",EDGE,"E25.10"),sQuery(id+"F3.wireOp",EDGE,"E25.11")])]})})});
            var Q82;
            Q82=makeQuery(id+"F12.boolean.opBoolean","SPLIT",BODY,{"disambiguationData":[OD(61.0)],"derivedFrom":makeQuery(id+"F10.boolean.opBoolean","SPLIT",BODY,{"disambiguationData":[OD(0.0)],"derivedFrom":makeQuery(id+"F4.opExtrude","SWEPT_BODY",BODY,{"disambiguationData":[OSD([sQuery(id+"F3.wireOp",EDGE,"E25.0"),sQuery(id+"F3.wireOp",EDGE,"E25.1"),sQuery(id+"F3.wireOp",EDGE,"E25.2"),sQuery(id+"F3.wireOp",EDGE,"E25.3"),sQuery(id+"F3.wireOp",EDGE,"E25.4"),sQuery(id+"F3.wireOp",EDGE,"E25.5"),sQuery(id+"F3.wireOp",EDGE,"E25.6"),sQuery(id+"F3.wireOp",EDGE,"E25.7"),sQuery(id+"F3.wireOp",EDGE,"E25.8"),sQuery(id+"F3.wireOp",EDGE,"E25.9"),sQuery(id+"F3.wireOp",EDGE,"E25.10"),sQuery(id+"F3.wireOp",EDGE,"E25.11")])]})})});
            var Q83;
            Q83=makeQuery(id+"F12.boolean.opBoolean","SPLIT",BODY,{"disambiguationData":[OD(62.0)],"derivedFrom":makeQuery(id+"F10.boolean.opBoolean","SPLIT",BODY,{"disambiguationData":[OD(0.0)],"derivedFrom":makeQuery(id+"F4.opExtrude","SWEPT_BODY",BODY,{"disambiguationData":[OSD([sQuery(id+"F3.wireOp",EDGE,"E25.0"),sQuery(id+"F3.wireOp",EDGE,"E25.1"),sQuery(id+"F3.wireOp",EDGE,"E25.2"),sQuery(id+"F3.wireOp",EDGE,"E25.3"),sQuery(id+"F3.wireOp",EDGE,"E25.4"),sQuery(id+"F3.wireOp",EDGE,"E25.5"),sQuery(id+"F3.wireOp",EDGE,"E25.6"),sQuery(id+"F3.wireOp",EDGE,"E25.7"),sQuery(id+"F3.wireOp",EDGE,"E25.8"),sQuery(id+"F3.wireOp",EDGE,"E25.9"),sQuery(id+"F3.wireOp",EDGE,"E25.10"),sQuery(id+"F3.wireOp",EDGE,"E25.11")])]})})});
            var Q84;
            Q84=makeQuery(id+"F12.boolean.opBoolean","SPLIT",BODY,{"disambiguationData":[OD(63.0)],"derivedFrom":makeQuery(id+"F10.boolean.opBoolean","SPLIT",BODY,{"disambiguationData":[OD(0.0)],"derivedFrom":makeQuery(id+"F4.opExtrude","SWEPT_BODY",BODY,{"disambiguationData":[OSD([sQuery(id+"F3.wireOp",EDGE,"E25.0"),sQuery(id+"F3.wireOp",EDGE,"E25.1"),sQuery(id+"F3.wireOp",EDGE,"E25.2"),sQuery(id+"F3.wireOp",EDGE,"E25.3"),sQuery(id+"F3.wireOp",EDGE,"E25.4"),sQuery(id+"F3.wireOp",EDGE,"E25.5"),sQuery(id+"F3.wireOp",EDGE,"E25.6"),sQuery(id+"F3.wireOp",EDGE,"E25.7"),sQuery(id+"F3.wireOp",EDGE,"E25.8"),sQuery(id+"F3.wireOp",EDGE,"E25.9"),sQuery(id+"F3.wireOp",EDGE,"E25.10"),sQuery(id+"F3.wireOp",EDGE,"E25.11")])]})})});
            var Q85;
            Q85=makeQuery(id+"F12.boolean.opBoolean","SPLIT",BODY,{"disambiguationData":[OD(64.0)],"derivedFrom":makeQuery(id+"F10.boolean.opBoolean","SPLIT",BODY,{"disambiguationData":[OD(0.0)],"derivedFrom":makeQuery(id+"F4.opExtrude","SWEPT_BODY",BODY,{"disambiguationData":[OSD([sQuery(id+"F3.wireOp",EDGE,"E25.0"),sQuery(id+"F3.wireOp",EDGE,"E25.1"),sQuery(id+"F3.wireOp",EDGE,"E25.2"),sQuery(id+"F3.wireOp",EDGE,"E25.3"),sQuery(id+"F3.wireOp",EDGE,"E25.4"),sQuery(id+"F3.wireOp",EDGE,"E25.5"),sQuery(id+"F3.wireOp",EDGE,"E25.6"),sQuery(id+"F3.wireOp",EDGE,"E25.7"),sQuery(id+"F3.wireOp",EDGE,"E25.8"),sQuery(id+"F3.wireOp",EDGE,"E25.9"),sQuery(id+"F3.wireOp",EDGE,"E25.10"),sQuery(id+"F3.wireOp",EDGE,"E25.11")])]})})});
            var Q86;
            Q86=makeQuery(id+"F12.boolean.opBoolean","SPLIT",BODY,{"disambiguationData":[OD(65.0)],"derivedFrom":makeQuery(id+"F10.boolean.opBoolean","SPLIT",BODY,{"disambiguationData":[OD(0.0)],"derivedFrom":makeQuery(id+"F4.opExtrude","SWEPT_BODY",BODY,{"disambiguationData":[OSD([sQuery(id+"F3.wireOp",EDGE,"E25.0"),sQuery(id+"F3.wireOp",EDGE,"E25.1"),sQuery(id+"F3.wireOp",EDGE,"E25.2"),sQuery(id+"F3.wireOp",EDGE,"E25.3"),sQuery(id+"F3.wireOp",EDGE,"E25.4"),sQuery(id+"F3.wireOp",EDGE,"E25.5"),sQuery(id+"F3.wireOp",EDGE,"E25.6"),sQuery(id+"F3.wireOp",EDGE,"E25.7"),sQuery(id+"F3.wireOp",EDGE,"E25.8"),sQuery(id+"F3.wireOp",EDGE,"E25.9"),sQuery(id+"F3.wireOp",EDGE,"E25.10"),sQuery(id+"F3.wireOp",EDGE,"E25.11")])]})})});
            var Q87;
            Q87=makeQuery(id+"F12.boolean.opBoolean","SPLIT",BODY,{"disambiguationData":[OD(66.0)],"derivedFrom":makeQuery(id+"F10.boolean.opBoolean","SPLIT",BODY,{"disambiguationData":[OD(0.0)],"derivedFrom":makeQuery(id+"F4.opExtrude","SWEPT_BODY",BODY,{"disambiguationData":[OSD([sQuery(id+"F3.wireOp",EDGE,"E25.0"),sQuery(id+"F3.wireOp",EDGE,"E25.1"),sQuery(id+"F3.wireOp",EDGE,"E25.2"),sQuery(id+"F3.wireOp",EDGE,"E25.3"),sQuery(id+"F3.wireOp",EDGE,"E25.4"),sQuery(id+"F3.wireOp",EDGE,"E25.5"),sQuery(id+"F3.wireOp",EDGE,"E25.6"),sQuery(id+"F3.wireOp",EDGE,"E25.7"),sQuery(id+"F3.wireOp",EDGE,"E25.8"),sQuery(id+"F3.wireOp",EDGE,"E25.9"),sQuery(id+"F3.wireOp",EDGE,"E25.10"),sQuery(id+"F3.wireOp",EDGE,"E25.11")])]})})});
            var Q88;
            Q88=makeQuery(id+"F12.boolean.opBoolean","SPLIT",BODY,{"disambiguationData":[OD(67.0)],"derivedFrom":makeQuery(id+"F10.boolean.opBoolean","SPLIT",BODY,{"disambiguationData":[OD(0.0)],"derivedFrom":makeQuery(id+"F4.opExtrude","SWEPT_BODY",BODY,{"disambiguationData":[OSD([sQuery(id+"F3.wireOp",EDGE,"E25.0"),sQuery(id+"F3.wireOp",EDGE,"E25.1"),sQuery(id+"F3.wireOp",EDGE,"E25.2"),sQuery(id+"F3.wireOp",EDGE,"E25.3"),sQuery(id+"F3.wireOp",EDGE,"E25.4"),sQuery(id+"F3.wireOp",EDGE,"E25.5"),sQuery(id+"F3.wireOp",EDGE,"E25.6"),sQuery(id+"F3.wireOp",EDGE,"E25.7"),sQuery(id+"F3.wireOp",EDGE,"E25.8"),sQuery(id+"F3.wireOp",EDGE,"E25.9"),sQuery(id+"F3.wireOp",EDGE,"E25.10"),sQuery(id+"F3.wireOp",EDGE,"E25.11")])]})})});
            var Q89;
            Q89=makeQuery(id+"F12.boolean.opBoolean","SPLIT",BODY,{"disambiguationData":[OD(68.0)],"derivedFrom":makeQuery(id+"F10.boolean.opBoolean","SPLIT",BODY,{"disambiguationData":[OD(0.0)],"derivedFrom":makeQuery(id+"F4.opExtrude","SWEPT_BODY",BODY,{"disambiguationData":[OSD([sQuery(id+"F3.wireOp",EDGE,"E25.0"),sQuery(id+"F3.wireOp",EDGE,"E25.1"),sQuery(id+"F3.wireOp",EDGE,"E25.2"),sQuery(id+"F3.wireOp",EDGE,"E25.3"),sQuery(id+"F3.wireOp",EDGE,"E25.4"),sQuery(id+"F3.wireOp",EDGE,"E25.5"),sQuery(id+"F3.wireOp",EDGE,"E25.6"),sQuery(id+"F3.wireOp",EDGE,"E25.7"),sQuery(id+"F3.wireOp",EDGE,"E25.8"),sQuery(id+"F3.wireOp",EDGE,"E25.9"),sQuery(id+"F3.wireOp",EDGE,"E25.10"),sQuery(id+"F3.wireOp",EDGE,"E25.11")])]})})});
            var Q90;
            Q90=makeQuery(id+"F12.boolean.opBoolean","SPLIT",BODY,{"disambiguationData":[OD(69.0)],"derivedFrom":makeQuery(id+"F10.boolean.opBoolean","SPLIT",BODY,{"disambiguationData":[OD(0.0)],"derivedFrom":makeQuery(id+"F4.opExtrude","SWEPT_BODY",BODY,{"disambiguationData":[OSD([sQuery(id+"F3.wireOp",EDGE,"E25.0"),sQuery(id+"F3.wireOp",EDGE,"E25.1"),sQuery(id+"F3.wireOp",EDGE,"E25.2"),sQuery(id+"F3.wireOp",EDGE,"E25.3"),sQuery(id+"F3.wireOp",EDGE,"E25.4"),sQuery(id+"F3.wireOp",EDGE,"E25.5"),sQuery(id+"F3.wireOp",EDGE,"E25.6"),sQuery(id+"F3.wireOp",EDGE,"E25.7"),sQuery(id+"F3.wireOp",EDGE,"E25.8"),sQuery(id+"F3.wireOp",EDGE,"E25.9"),sQuery(id+"F3.wireOp",EDGE,"E25.10"),sQuery(id+"F3.wireOp",EDGE,"E25.11")])]})})});
            var Q91;
            Q91=makeQuery(id+"F12.boolean.opBoolean","SPLIT",BODY,{"disambiguationData":[OD(70.0)],"derivedFrom":makeQuery(id+"F10.boolean.opBoolean","SPLIT",BODY,{"disambiguationData":[OD(0.0)],"derivedFrom":makeQuery(id+"F4.opExtrude","SWEPT_BODY",BODY,{"disambiguationData":[OSD([sQuery(id+"F3.wireOp",EDGE,"E25.0"),sQuery(id+"F3.wireOp",EDGE,"E25.1"),sQuery(id+"F3.wireOp",EDGE,"E25.2"),sQuery(id+"F3.wireOp",EDGE,"E25.3"),sQuery(id+"F3.wireOp",EDGE,"E25.4"),sQuery(id+"F3.wireOp",EDGE,"E25.5"),sQuery(id+"F3.wireOp",EDGE,"E25.6"),sQuery(id+"F3.wireOp",EDGE,"E25.7"),sQuery(id+"F3.wireOp",EDGE,"E25.8"),sQuery(id+"F3.wireOp",EDGE,"E25.9"),sQuery(id+"F3.wireOp",EDGE,"E25.10"),sQuery(id+"F3.wireOp",EDGE,"E25.11")])]})})});
            var Q92;
            Q92=makeQuery(id+"F12.boolean.opBoolean","SPLIT",BODY,{"disambiguationData":[OD(71.0)],"derivedFrom":makeQuery(id+"F10.boolean.opBoolean","SPLIT",BODY,{"disambiguationData":[OD(0.0)],"derivedFrom":makeQuery(id+"F4.opExtrude","SWEPT_BODY",BODY,{"disambiguationData":[OSD([sQuery(id+"F3.wireOp",EDGE,"E25.0"),sQuery(id+"F3.wireOp",EDGE,"E25.1"),sQuery(id+"F3.wireOp",EDGE,"E25.2"),sQuery(id+"F3.wireOp",EDGE,"E25.3"),sQuery(id+"F3.wireOp",EDGE,"E25.4"),sQuery(id+"F3.wireOp",EDGE,"E25.5"),sQuery(id+"F3.wireOp",EDGE,"E25.6"),sQuery(id+"F3.wireOp",EDGE,"E25.7"),sQuery(id+"F3.wireOp",EDGE,"E25.8"),sQuery(id+"F3.wireOp",EDGE,"E25.9"),sQuery(id+"F3.wireOp",EDGE,"E25.10"),sQuery(id+"F3.wireOp",EDGE,"E25.11")])]})})});
            var Q93;
            Q93=makeQuery(id+"F12.boolean.opBoolean","SPLIT",BODY,{"disambiguationData":[OD(72.0)],"derivedFrom":makeQuery(id+"F10.boolean.opBoolean","SPLIT",BODY,{"disambiguationData":[OD(0.0)],"derivedFrom":makeQuery(id+"F4.opExtrude","SWEPT_BODY",BODY,{"disambiguationData":[OSD([sQuery(id+"F3.wireOp",EDGE,"E25.0"),sQuery(id+"F3.wireOp",EDGE,"E25.1"),sQuery(id+"F3.wireOp",EDGE,"E25.2"),sQuery(id+"F3.wireOp",EDGE,"E25.3"),sQuery(id+"F3.wireOp",EDGE,"E25.4"),sQuery(id+"F3.wireOp",EDGE,"E25.5"),sQuery(id+"F3.wireOp",EDGE,"E25.6"),sQuery(id+"F3.wireOp",EDGE,"E25.7"),sQuery(id+"F3.wireOp",EDGE,"E25.8"),sQuery(id+"F3.wireOp",EDGE,"E25.9"),sQuery(id+"F3.wireOp",EDGE,"E25.10"),sQuery(id+"F3.wireOp",EDGE,"E25.11")])]})})});
            var Q94;
            Q94=makeQuery(id+"F12.boolean.opBoolean","SPLIT",BODY,{"disambiguationData":[OD(73.0)],"derivedFrom":makeQuery(id+"F10.boolean.opBoolean","SPLIT",BODY,{"disambiguationData":[OD(0.0)],"derivedFrom":makeQuery(id+"F4.opExtrude","SWEPT_BODY",BODY,{"disambiguationData":[OSD([sQuery(id+"F3.wireOp",EDGE,"E25.0"),sQuery(id+"F3.wireOp",EDGE,"E25.1"),sQuery(id+"F3.wireOp",EDGE,"E25.2"),sQuery(id+"F3.wireOp",EDGE,"E25.3"),sQuery(id+"F3.wireOp",EDGE,"E25.4"),sQuery(id+"F3.wireOp",EDGE,"E25.5"),sQuery(id+"F3.wireOp",EDGE,"E25.6"),sQuery(id+"F3.wireOp",EDGE,"E25.7"),sQuery(id+"F3.wireOp",EDGE,"E25.8"),sQuery(id+"F3.wireOp",EDGE,"E25.9"),sQuery(id+"F3.wireOp",EDGE,"E25.10"),sQuery(id+"F3.wireOp",EDGE,"E25.11")])]})})});
            var Q95;
            Q95=makeQuery(id+"F12.boolean.opBoolean","SPLIT",BODY,{"disambiguationData":[OD(74.0)],"derivedFrom":makeQuery(id+"F10.boolean.opBoolean","SPLIT",BODY,{"disambiguationData":[OD(0.0)],"derivedFrom":makeQuery(id+"F4.opExtrude","SWEPT_BODY",BODY,{"disambiguationData":[OSD([sQuery(id+"F3.wireOp",EDGE,"E25.0"),sQuery(id+"F3.wireOp",EDGE,"E25.1"),sQuery(id+"F3.wireOp",EDGE,"E25.2"),sQuery(id+"F3.wireOp",EDGE,"E25.3"),sQuery(id+"F3.wireOp",EDGE,"E25.4"),sQuery(id+"F3.wireOp",EDGE,"E25.5"),sQuery(id+"F3.wireOp",EDGE,"E25.6"),sQuery(id+"F3.wireOp",EDGE,"E25.7"),sQuery(id+"F3.wireOp",EDGE,"E25.8"),sQuery(id+"F3.wireOp",EDGE,"E25.9"),sQuery(id+"F3.wireOp",EDGE,"E25.10"),sQuery(id+"F3.wireOp",EDGE,"E25.11")])]})})});
            var Q96;
            Q96=makeQuery(id+"F12.boolean.opBoolean","SPLIT",BODY,{"disambiguationData":[OD(75.0)],"derivedFrom":makeQuery(id+"F10.boolean.opBoolean","SPLIT",BODY,{"disambiguationData":[OD(0.0)],"derivedFrom":makeQuery(id+"F4.opExtrude","SWEPT_BODY",BODY,{"disambiguationData":[OSD([sQuery(id+"F3.wireOp",EDGE,"E25.0"),sQuery(id+"F3.wireOp",EDGE,"E25.1"),sQuery(id+"F3.wireOp",EDGE,"E25.2"),sQuery(id+"F3.wireOp",EDGE,"E25.3"),sQuery(id+"F3.wireOp",EDGE,"E25.4"),sQuery(id+"F3.wireOp",EDGE,"E25.5"),sQuery(id+"F3.wireOp",EDGE,"E25.6"),sQuery(id+"F3.wireOp",EDGE,"E25.7"),sQuery(id+"F3.wireOp",EDGE,"E25.8"),sQuery(id+"F3.wireOp",EDGE,"E25.9"),sQuery(id+"F3.wireOp",EDGE,"E25.10"),sQuery(id+"F3.wireOp",EDGE,"E25.11")])]})})});
            var Q97;
            Q97=makeQuery(id+"F12.boolean.opBoolean","SPLIT",BODY,{"disambiguationData":[OD(76.0)],"derivedFrom":makeQuery(id+"F10.boolean.opBoolean","SPLIT",BODY,{"disambiguationData":[OD(0.0)],"derivedFrom":makeQuery(id+"F4.opExtrude","SWEPT_BODY",BODY,{"disambiguationData":[OSD([sQuery(id+"F3.wireOp",EDGE,"E25.0"),sQuery(id+"F3.wireOp",EDGE,"E25.1"),sQuery(id+"F3.wireOp",EDGE,"E25.2"),sQuery(id+"F3.wireOp",EDGE,"E25.3"),sQuery(id+"F3.wireOp",EDGE,"E25.4"),sQuery(id+"F3.wireOp",EDGE,"E25.5"),sQuery(id+"F3.wireOp",EDGE,"E25.6"),sQuery(id+"F3.wireOp",EDGE,"E25.7"),sQuery(id+"F3.wireOp",EDGE,"E25.8"),sQuery(id+"F3.wireOp",EDGE,"E25.9"),sQuery(id+"F3.wireOp",EDGE,"E25.10"),sQuery(id+"F3.wireOp",EDGE,"E25.11")])]})})});
            var Q98;
            Q98=makeQuery(id+"F12.boolean.opBoolean","SPLIT",BODY,{"disambiguationData":[OD(77.0)],"derivedFrom":makeQuery(id+"F10.boolean.opBoolean","SPLIT",BODY,{"disambiguationData":[OD(0.0)],"derivedFrom":makeQuery(id+"F4.opExtrude","SWEPT_BODY",BODY,{"disambiguationData":[OSD([sQuery(id+"F3.wireOp",EDGE,"E25.0"),sQuery(id+"F3.wireOp",EDGE,"E25.1"),sQuery(id+"F3.wireOp",EDGE,"E25.2"),sQuery(id+"F3.wireOp",EDGE,"E25.3"),sQuery(id+"F3.wireOp",EDGE,"E25.4"),sQuery(id+"F3.wireOp",EDGE,"E25.5"),sQuery(id+"F3.wireOp",EDGE,"E25.6"),sQuery(id+"F3.wireOp",EDGE,"E25.7"),sQuery(id+"F3.wireOp",EDGE,"E25.8"),sQuery(id+"F3.wireOp",EDGE,"E25.9"),sQuery(id+"F3.wireOp",EDGE,"E25.10"),sQuery(id+"F3.wireOp",EDGE,"E25.11")])]})})});
            var Q99;
            Q99=makeQuery(id+"F12.boolean.opBoolean","SPLIT",BODY,{"disambiguationData":[OD(78.0)],"derivedFrom":makeQuery(id+"F10.boolean.opBoolean","SPLIT",BODY,{"disambiguationData":[OD(0.0)],"derivedFrom":makeQuery(id+"F4.opExtrude","SWEPT_BODY",BODY,{"disambiguationData":[OSD([sQuery(id+"F3.wireOp",EDGE,"E25.0"),sQuery(id+"F3.wireOp",EDGE,"E25.1"),sQuery(id+"F3.wireOp",EDGE,"E25.2"),sQuery(id+"F3.wireOp",EDGE,"E25.3"),sQuery(id+"F3.wireOp",EDGE,"E25.4"),sQuery(id+"F3.wireOp",EDGE,"E25.5"),sQuery(id+"F3.wireOp",EDGE,"E25.6"),sQuery(id+"F3.wireOp",EDGE,"E25.7"),sQuery(id+"F3.wireOp",EDGE,"E25.8"),sQuery(id+"F3.wireOp",EDGE,"E25.9"),sQuery(id+"F3.wireOp",EDGE,"E25.10"),sQuery(id+"F3.wireOp",EDGE,"E25.11")])]})})});
            var Q100;
            Q100=makeQuery(id+"F12.boolean.opBoolean","SPLIT",BODY,{"disambiguationData":[OD(79.0)],"derivedFrom":makeQuery(id+"F10.boolean.opBoolean","SPLIT",BODY,{"disambiguationData":[OD(0.0)],"derivedFrom":makeQuery(id+"F4.opExtrude","SWEPT_BODY",BODY,{"disambiguationData":[OSD([sQuery(id+"F3.wireOp",EDGE,"E25.0"),sQuery(id+"F3.wireOp",EDGE,"E25.1"),sQuery(id+"F3.wireOp",EDGE,"E25.2"),sQuery(id+"F3.wireOp",EDGE,"E25.3"),sQuery(id+"F3.wireOp",EDGE,"E25.4"),sQuery(id+"F3.wireOp",EDGE,"E25.5"),sQuery(id+"F3.wireOp",EDGE,"E25.6"),sQuery(id+"F3.wireOp",EDGE,"E25.7"),sQuery(id+"F3.wireOp",EDGE,"E25.8"),sQuery(id+"F3.wireOp",EDGE,"E25.9"),sQuery(id+"F3.wireOp",EDGE,"E25.10"),sQuery(id+"F3.wireOp",EDGE,"E25.11")])]})})});
            var Q101;
            Q101=makeQuery(id+"F12.boolean.opBoolean","SPLIT",BODY,{"disambiguationData":[OD(80.0)],"derivedFrom":makeQuery(id+"F10.boolean.opBoolean","SPLIT",BODY,{"disambiguationData":[OD(0.0)],"derivedFrom":makeQuery(id+"F4.opExtrude","SWEPT_BODY",BODY,{"disambiguationData":[OSD([sQuery(id+"F3.wireOp",EDGE,"E25.0"),sQuery(id+"F3.wireOp",EDGE,"E25.1"),sQuery(id+"F3.wireOp",EDGE,"E25.2"),sQuery(id+"F3.wireOp",EDGE,"E25.3"),sQuery(id+"F3.wireOp",EDGE,"E25.4"),sQuery(id+"F3.wireOp",EDGE,"E25.5"),sQuery(id+"F3.wireOp",EDGE,"E25.6"),sQuery(id+"F3.wireOp",EDGE,"E25.7"),sQuery(id+"F3.wireOp",EDGE,"E25.8"),sQuery(id+"F3.wireOp",EDGE,"E25.9"),sQuery(id+"F3.wireOp",EDGE,"E25.10"),sQuery(id+"F3.wireOp",EDGE,"E25.11")])]})})});
            var Q102;
            Q102=makeQuery(id+"F12.boolean.opBoolean","SPLIT",BODY,{"disambiguationData":[OD(81.0)],"derivedFrom":makeQuery(id+"F10.boolean.opBoolean","SPLIT",BODY,{"disambiguationData":[OD(0.0)],"derivedFrom":makeQuery(id+"F4.opExtrude","SWEPT_BODY",BODY,{"disambiguationData":[OSD([sQuery(id+"F3.wireOp",EDGE,"E25.0"),sQuery(id+"F3.wireOp",EDGE,"E25.1"),sQuery(id+"F3.wireOp",EDGE,"E25.2"),sQuery(id+"F3.wireOp",EDGE,"E25.3"),sQuery(id+"F3.wireOp",EDGE,"E25.4"),sQuery(id+"F3.wireOp",EDGE,"E25.5"),sQuery(id+"F3.wireOp",EDGE,"E25.6"),sQuery(id+"F3.wireOp",EDGE,"E25.7"),sQuery(id+"F3.wireOp",EDGE,"E25.8"),sQuery(id+"F3.wireOp",EDGE,"E25.9"),sQuery(id+"F3.wireOp",EDGE,"E25.10"),sQuery(id+"F3.wireOp",EDGE,"E25.11")])]})})});
            var Q103;
            Q103=makeQuery(id+"F12.boolean.opBoolean","SPLIT",BODY,{"disambiguationData":[OD(82.0)],"derivedFrom":makeQuery(id+"F10.boolean.opBoolean","SPLIT",BODY,{"disambiguationData":[OD(0.0)],"derivedFrom":makeQuery(id+"F4.opExtrude","SWEPT_BODY",BODY,{"disambiguationData":[OSD([sQuery(id+"F3.wireOp",EDGE,"E25.0"),sQuery(id+"F3.wireOp",EDGE,"E25.1"),sQuery(id+"F3.wireOp",EDGE,"E25.2"),sQuery(id+"F3.wireOp",EDGE,"E25.3"),sQuery(id+"F3.wireOp",EDGE,"E25.4"),sQuery(id+"F3.wireOp",EDGE,"E25.5"),sQuery(id+"F3.wireOp",EDGE,"E25.6"),sQuery(id+"F3.wireOp",EDGE,"E25.7"),sQuery(id+"F3.wireOp",EDGE,"E25.8"),sQuery(id+"F3.wireOp",EDGE,"E25.9"),sQuery(id+"F3.wireOp",EDGE,"E25.10"),sQuery(id+"F3.wireOp",EDGE,"E25.11")])]})})});
            var Q104;
            Q104=makeQuery(id+"F12.boolean.opBoolean","SPLIT",BODY,{"disambiguationData":[OD(83.0)],"derivedFrom":makeQuery(id+"F10.boolean.opBoolean","SPLIT",BODY,{"disambiguationData":[OD(0.0)],"derivedFrom":makeQuery(id+"F4.opExtrude","SWEPT_BODY",BODY,{"disambiguationData":[OSD([sQuery(id+"F3.wireOp",EDGE,"E25.0"),sQuery(id+"F3.wireOp",EDGE,"E25.1"),sQuery(id+"F3.wireOp",EDGE,"E25.2"),sQuery(id+"F3.wireOp",EDGE,"E25.3"),sQuery(id+"F3.wireOp",EDGE,"E25.4"),sQuery(id+"F3.wireOp",EDGE,"E25.5"),sQuery(id+"F3.wireOp",EDGE,"E25.6"),sQuery(id+"F3.wireOp",EDGE,"E25.7"),sQuery(id+"F3.wireOp",EDGE,"E25.8"),sQuery(id+"F3.wireOp",EDGE,"E25.9"),sQuery(id+"F3.wireOp",EDGE,"E25.10"),sQuery(id+"F3.wireOp",EDGE,"E25.11")])]})})});
            var Q105;
            Q105=makeQuery(id+"F12.boolean.opBoolean","SPLIT",BODY,{"disambiguationData":[OD(84.0)],"derivedFrom":makeQuery(id+"F10.boolean.opBoolean","SPLIT",BODY,{"disambiguationData":[OD(0.0)],"derivedFrom":makeQuery(id+"F4.opExtrude","SWEPT_BODY",BODY,{"disambiguationData":[OSD([sQuery(id+"F3.wireOp",EDGE,"E25.0"),sQuery(id+"F3.wireOp",EDGE,"E25.1"),sQuery(id+"F3.wireOp",EDGE,"E25.2"),sQuery(id+"F3.wireOp",EDGE,"E25.3"),sQuery(id+"F3.wireOp",EDGE,"E25.4"),sQuery(id+"F3.wireOp",EDGE,"E25.5"),sQuery(id+"F3.wireOp",EDGE,"E25.6"),sQuery(id+"F3.wireOp",EDGE,"E25.7"),sQuery(id+"F3.wireOp",EDGE,"E25.8"),sQuery(id+"F3.wireOp",EDGE,"E25.9"),sQuery(id+"F3.wireOp",EDGE,"E25.10"),sQuery(id+"F3.wireOp",EDGE,"E25.11")])]})})});
            var Q106;
            Q106=makeQuery(id+"F12.boolean.opBoolean","SPLIT",BODY,{"disambiguationData":[OD(85.0)],"derivedFrom":makeQuery(id+"F10.boolean.opBoolean","SPLIT",BODY,{"disambiguationData":[OD(0.0)],"derivedFrom":makeQuery(id+"F4.opExtrude","SWEPT_BODY",BODY,{"disambiguationData":[OSD([sQuery(id+"F3.wireOp",EDGE,"E25.0"),sQuery(id+"F3.wireOp",EDGE,"E25.1"),sQuery(id+"F3.wireOp",EDGE,"E25.2"),sQuery(id+"F3.wireOp",EDGE,"E25.3"),sQuery(id+"F3.wireOp",EDGE,"E25.4"),sQuery(id+"F3.wireOp",EDGE,"E25.5"),sQuery(id+"F3.wireOp",EDGE,"E25.6"),sQuery(id+"F3.wireOp",EDGE,"E25.7"),sQuery(id+"F3.wireOp",EDGE,"E25.8"),sQuery(id+"F3.wireOp",EDGE,"E25.9"),sQuery(id+"F3.wireOp",EDGE,"E25.10"),sQuery(id+"F3.wireOp",EDGE,"E25.11")])]})})});
            var Q107;
            Q107=makeQuery(id+"F12.boolean.opBoolean","SPLIT",BODY,{"disambiguationData":[OD(86.0)],"derivedFrom":makeQuery(id+"F10.boolean.opBoolean","SPLIT",BODY,{"disambiguationData":[OD(0.0)],"derivedFrom":makeQuery(id+"F4.opExtrude","SWEPT_BODY",BODY,{"disambiguationData":[OSD([sQuery(id+"F3.wireOp",EDGE,"E25.0"),sQuery(id+"F3.wireOp",EDGE,"E25.1"),sQuery(id+"F3.wireOp",EDGE,"E25.2"),sQuery(id+"F3.wireOp",EDGE,"E25.3"),sQuery(id+"F3.wireOp",EDGE,"E25.4"),sQuery(id+"F3.wireOp",EDGE,"E25.5"),sQuery(id+"F3.wireOp",EDGE,"E25.6"),sQuery(id+"F3.wireOp",EDGE,"E25.7"),sQuery(id+"F3.wireOp",EDGE,"E25.8"),sQuery(id+"F3.wireOp",EDGE,"E25.9"),sQuery(id+"F3.wireOp",EDGE,"E25.10"),sQuery(id+"F3.wireOp",EDGE,"E25.11")])]})})});
            var Q108;
            Q108=makeQuery(id+"F12.boolean.opBoolean","SPLIT",BODY,{"disambiguationData":[OD(87.0)],"derivedFrom":makeQuery(id+"F10.boolean.opBoolean","SPLIT",BODY,{"disambiguationData":[OD(0.0)],"derivedFrom":makeQuery(id+"F4.opExtrude","SWEPT_BODY",BODY,{"disambiguationData":[OSD([sQuery(id+"F3.wireOp",EDGE,"E25.0"),sQuery(id+"F3.wireOp",EDGE,"E25.1"),sQuery(id+"F3.wireOp",EDGE,"E25.2"),sQuery(id+"F3.wireOp",EDGE,"E25.3"),sQuery(id+"F3.wireOp",EDGE,"E25.4"),sQuery(id+"F3.wireOp",EDGE,"E25.5"),sQuery(id+"F3.wireOp",EDGE,"E25.6"),sQuery(id+"F3.wireOp",EDGE,"E25.7"),sQuery(id+"F3.wireOp",EDGE,"E25.8"),sQuery(id+"F3.wireOp",EDGE,"E25.9"),sQuery(id+"F3.wireOp",EDGE,"E25.10"),sQuery(id+"F3.wireOp",EDGE,"E25.11")])]})})});
            var Q109;
            Q109=makeQuery(id+"F12.boolean.opBoolean","SPLIT",BODY,{"disambiguationData":[OD(88.0)],"derivedFrom":makeQuery(id+"F10.boolean.opBoolean","SPLIT",BODY,{"disambiguationData":[OD(0.0)],"derivedFrom":makeQuery(id+"F4.opExtrude","SWEPT_BODY",BODY,{"disambiguationData":[OSD([sQuery(id+"F3.wireOp",EDGE,"E25.0"),sQuery(id+"F3.wireOp",EDGE,"E25.1"),sQuery(id+"F3.wireOp",EDGE,"E25.2"),sQuery(id+"F3.wireOp",EDGE,"E25.3"),sQuery(id+"F3.wireOp",EDGE,"E25.4"),sQuery(id+"F3.wireOp",EDGE,"E25.5"),sQuery(id+"F3.wireOp",EDGE,"E25.6"),sQuery(id+"F3.wireOp",EDGE,"E25.7"),sQuery(id+"F3.wireOp",EDGE,"E25.8"),sQuery(id+"F3.wireOp",EDGE,"E25.9"),sQuery(id+"F3.wireOp",EDGE,"E25.10"),sQuery(id+"F3.wireOp",EDGE,"E25.11")])]})})});
            var Q110;
            Q110=makeQuery(id+"F12.boolean.opBoolean","SPLIT",BODY,{"disambiguationData":[OD(89.0)],"derivedFrom":makeQuery(id+"F10.boolean.opBoolean","SPLIT",BODY,{"disambiguationData":[OD(0.0)],"derivedFrom":makeQuery(id+"F4.opExtrude","SWEPT_BODY",BODY,{"disambiguationData":[OSD([sQuery(id+"F3.wireOp",EDGE,"E25.0"),sQuery(id+"F3.wireOp",EDGE,"E25.1"),sQuery(id+"F3.wireOp",EDGE,"E25.2"),sQuery(id+"F3.wireOp",EDGE,"E25.3"),sQuery(id+"F3.wireOp",EDGE,"E25.4"),sQuery(id+"F3.wireOp",EDGE,"E25.5"),sQuery(id+"F3.wireOp",EDGE,"E25.6"),sQuery(id+"F3.wireOp",EDGE,"E25.7"),sQuery(id+"F3.wireOp",EDGE,"E25.8"),sQuery(id+"F3.wireOp",EDGE,"E25.9"),sQuery(id+"F3.wireOp",EDGE,"E25.10"),sQuery(id+"F3.wireOp",EDGE,"E25.11")])]})})});
            var Q111;
            Q111=makeQuery(id+"F12.boolean.opBoolean","SPLIT",BODY,{"disambiguationData":[OD(90.0)],"derivedFrom":makeQuery(id+"F10.boolean.opBoolean","SPLIT",BODY,{"disambiguationData":[OD(0.0)],"derivedFrom":makeQuery(id+"F4.opExtrude","SWEPT_BODY",BODY,{"disambiguationData":[OSD([sQuery(id+"F3.wireOp",EDGE,"E25.0"),sQuery(id+"F3.wireOp",EDGE,"E25.1"),sQuery(id+"F3.wireOp",EDGE,"E25.2"),sQuery(id+"F3.wireOp",EDGE,"E25.3"),sQuery(id+"F3.wireOp",EDGE,"E25.4"),sQuery(id+"F3.wireOp",EDGE,"E25.5"),sQuery(id+"F3.wireOp",EDGE,"E25.6"),sQuery(id+"F3.wireOp",EDGE,"E25.7"),sQuery(id+"F3.wireOp",EDGE,"E25.8"),sQuery(id+"F3.wireOp",EDGE,"E25.9"),sQuery(id+"F3.wireOp",EDGE,"E25.10"),sQuery(id+"F3.wireOp",EDGE,"E25.11")])]})})});
            var Q112;
            Q112=makeQuery(id+"F12.boolean.opBoolean","SPLIT",BODY,{"disambiguationData":[OD(91.0)],"derivedFrom":makeQuery(id+"F10.boolean.opBoolean","SPLIT",BODY,{"disambiguationData":[OD(0.0)],"derivedFrom":makeQuery(id+"F4.opExtrude","SWEPT_BODY",BODY,{"disambiguationData":[OSD([sQuery(id+"F3.wireOp",EDGE,"E25.0"),sQuery(id+"F3.wireOp",EDGE,"E25.1"),sQuery(id+"F3.wireOp",EDGE,"E25.2"),sQuery(id+"F3.wireOp",EDGE,"E25.3"),sQuery(id+"F3.wireOp",EDGE,"E25.4"),sQuery(id+"F3.wireOp",EDGE,"E25.5"),sQuery(id+"F3.wireOp",EDGE,"E25.6"),sQuery(id+"F3.wireOp",EDGE,"E25.7"),sQuery(id+"F3.wireOp",EDGE,"E25.8"),sQuery(id+"F3.wireOp",EDGE,"E25.9"),sQuery(id+"F3.wireOp",EDGE,"E25.10"),sQuery(id+"F3.wireOp",EDGE,"E25.11")])]})})});
            var Q113;
            Q113=makeQuery(id+"F12.boolean.opBoolean","SPLIT",BODY,{"disambiguationData":[OD(92.0)],"derivedFrom":makeQuery(id+"F10.boolean.opBoolean","SPLIT",BODY,{"disambiguationData":[OD(0.0)],"derivedFrom":makeQuery(id+"F4.opExtrude","SWEPT_BODY",BODY,{"disambiguationData":[OSD([sQuery(id+"F3.wireOp",EDGE,"E25.0"),sQuery(id+"F3.wireOp",EDGE,"E25.1"),sQuery(id+"F3.wireOp",EDGE,"E25.2"),sQuery(id+"F3.wireOp",EDGE,"E25.3"),sQuery(id+"F3.wireOp",EDGE,"E25.4"),sQuery(id+"F3.wireOp",EDGE,"E25.5"),sQuery(id+"F3.wireOp",EDGE,"E25.6"),sQuery(id+"F3.wireOp",EDGE,"E25.7"),sQuery(id+"F3.wireOp",EDGE,"E25.8"),sQuery(id+"F3.wireOp",EDGE,"E25.9"),sQuery(id+"F3.wireOp",EDGE,"E25.10"),sQuery(id+"F3.wireOp",EDGE,"E25.11")])]})})});
            var Q114;
            Q114=makeQuery(id+"F12.boolean.opBoolean","SPLIT",BODY,{"disambiguationData":[OD(93.0)],"derivedFrom":makeQuery(id+"F10.boolean.opBoolean","SPLIT",BODY,{"disambiguationData":[OD(0.0)],"derivedFrom":makeQuery(id+"F4.opExtrude","SWEPT_BODY",BODY,{"disambiguationData":[OSD([sQuery(id+"F3.wireOp",EDGE,"E25.0"),sQuery(id+"F3.wireOp",EDGE,"E25.1"),sQuery(id+"F3.wireOp",EDGE,"E25.2"),sQuery(id+"F3.wireOp",EDGE,"E25.3"),sQuery(id+"F3.wireOp",EDGE,"E25.4"),sQuery(id+"F3.wireOp",EDGE,"E25.5"),sQuery(id+"F3.wireOp",EDGE,"E25.6"),sQuery(id+"F3.wireOp",EDGE,"E25.7"),sQuery(id+"F3.wireOp",EDGE,"E25.8"),sQuery(id+"F3.wireOp",EDGE,"E25.9"),sQuery(id+"F3.wireOp",EDGE,"E25.10"),sQuery(id+"F3.wireOp",EDGE,"E25.11")])]})})});
            var Q115;
            Q115=makeQuery(id+"F12.boolean.opBoolean","SPLIT",BODY,{"disambiguationData":[OD(94.0)],"derivedFrom":makeQuery(id+"F10.boolean.opBoolean","SPLIT",BODY,{"disambiguationData":[OD(0.0)],"derivedFrom":makeQuery(id+"F4.opExtrude","SWEPT_BODY",BODY,{"disambiguationData":[OSD([sQuery(id+"F3.wireOp",EDGE,"E25.0"),sQuery(id+"F3.wireOp",EDGE,"E25.1"),sQuery(id+"F3.wireOp",EDGE,"E25.2"),sQuery(id+"F3.wireOp",EDGE,"E25.3"),sQuery(id+"F3.wireOp",EDGE,"E25.4"),sQuery(id+"F3.wireOp",EDGE,"E25.5"),sQuery(id+"F3.wireOp",EDGE,"E25.6"),sQuery(id+"F3.wireOp",EDGE,"E25.7"),sQuery(id+"F3.wireOp",EDGE,"E25.8"),sQuery(id+"F3.wireOp",EDGE,"E25.9"),sQuery(id+"F3.wireOp",EDGE,"E25.10"),sQuery(id+"F3.wireOp",EDGE,"E25.11")])]})})});
            var Q116;
            Q116=makeQuery(id+"F12.boolean.opBoolean","SPLIT",BODY,{"disambiguationData":[OD(95.0)],"derivedFrom":makeQuery(id+"F10.boolean.opBoolean","SPLIT",BODY,{"disambiguationData":[OD(0.0)],"derivedFrom":makeQuery(id+"F4.opExtrude","SWEPT_BODY",BODY,{"disambiguationData":[OSD([sQuery(id+"F3.wireOp",EDGE,"E25.0"),sQuery(id+"F3.wireOp",EDGE,"E25.1"),sQuery(id+"F3.wireOp",EDGE,"E25.2"),sQuery(id+"F3.wireOp",EDGE,"E25.3"),sQuery(id+"F3.wireOp",EDGE,"E25.4"),sQuery(id+"F3.wireOp",EDGE,"E25.5"),sQuery(id+"F3.wireOp",EDGE,"E25.6"),sQuery(id+"F3.wireOp",EDGE,"E25.7"),sQuery(id+"F3.wireOp",EDGE,"E25.8"),sQuery(id+"F3.wireOp",EDGE,"E25.9"),sQuery(id+"F3.wireOp",EDGE,"E25.10"),sQuery(id+"F3.wireOp",EDGE,"E25.11")])]})})});
            var Q117;
            Q117=makeQuery(id+"F12.boolean.opBoolean","SPLIT",BODY,{"disambiguationData":[OD(96.0)],"derivedFrom":makeQuery(id+"F10.boolean.opBoolean","SPLIT",BODY,{"disambiguationData":[OD(0.0)],"derivedFrom":makeQuery(id+"F4.opExtrude","SWEPT_BODY",BODY,{"disambiguationData":[OSD([sQuery(id+"F3.wireOp",EDGE,"E25.0"),sQuery(id+"F3.wireOp",EDGE,"E25.1"),sQuery(id+"F3.wireOp",EDGE,"E25.2"),sQuery(id+"F3.wireOp",EDGE,"E25.3"),sQuery(id+"F3.wireOp",EDGE,"E25.4"),sQuery(id+"F3.wireOp",EDGE,"E25.5"),sQuery(id+"F3.wireOp",EDGE,"E25.6"),sQuery(id+"F3.wireOp",EDGE,"E25.7"),sQuery(id+"F3.wireOp",EDGE,"E25.8"),sQuery(id+"F3.wireOp",EDGE,"E25.9"),sQuery(id+"F3.wireOp",EDGE,"E25.10"),sQuery(id+"F3.wireOp",EDGE,"E25.11")])]})})});
            var Q118;
            Q118=makeQuery(id+"F12.boolean.opBoolean","SPLIT",BODY,{"disambiguationData":[OD(97.0)],"derivedFrom":makeQuery(id+"F10.boolean.opBoolean","SPLIT",BODY,{"disambiguationData":[OD(0.0)],"derivedFrom":makeQuery(id+"F4.opExtrude","SWEPT_BODY",BODY,{"disambiguationData":[OSD([sQuery(id+"F3.wireOp",EDGE,"E25.0"),sQuery(id+"F3.wireOp",EDGE,"E25.1"),sQuery(id+"F3.wireOp",EDGE,"E25.2"),sQuery(id+"F3.wireOp",EDGE,"E25.3"),sQuery(id+"F3.wireOp",EDGE,"E25.4"),sQuery(id+"F3.wireOp",EDGE,"E25.5"),sQuery(id+"F3.wireOp",EDGE,"E25.6"),sQuery(id+"F3.wireOp",EDGE,"E25.7"),sQuery(id+"F3.wireOp",EDGE,"E25.8"),sQuery(id+"F3.wireOp",EDGE,"E25.9"),sQuery(id+"F3.wireOp",EDGE,"E25.10"),sQuery(id+"F3.wireOp",EDGE,"E25.11")])]})})});
            var Q119;
            Q119=makeQuery(id+"F12.boolean.opBoolean","SPLIT",BODY,{"disambiguationData":[OD(98.0)],"derivedFrom":makeQuery(id+"F10.boolean.opBoolean","SPLIT",BODY,{"disambiguationData":[OD(0.0)],"derivedFrom":makeQuery(id+"F4.opExtrude","SWEPT_BODY",BODY,{"disambiguationData":[OSD([sQuery(id+"F3.wireOp",EDGE,"E25.0"),sQuery(id+"F3.wireOp",EDGE,"E25.1"),sQuery(id+"F3.wireOp",EDGE,"E25.2"),sQuery(id+"F3.wireOp",EDGE,"E25.3"),sQuery(id+"F3.wireOp",EDGE,"E25.4"),sQuery(id+"F3.wireOp",EDGE,"E25.5"),sQuery(id+"F3.wireOp",EDGE,"E25.6"),sQuery(id+"F3.wireOp",EDGE,"E25.7"),sQuery(id+"F3.wireOp",EDGE,"E25.8"),sQuery(id+"F3.wireOp",EDGE,"E25.9"),sQuery(id+"F3.wireOp",EDGE,"E25.10"),sQuery(id+"F3.wireOp",EDGE,"E25.11")])]})})});
            var Q120;
            Q120=makeQuery(id+"F12.boolean.opBoolean","SPLIT",BODY,{"disambiguationData":[OD(99.0)],"derivedFrom":makeQuery(id+"F10.boolean.opBoolean","SPLIT",BODY,{"disambiguationData":[OD(0.0)],"derivedFrom":makeQuery(id+"F4.opExtrude","SWEPT_BODY",BODY,{"disambiguationData":[OSD([sQuery(id+"F3.wireOp",EDGE,"E25.0"),sQuery(id+"F3.wireOp",EDGE,"E25.1"),sQuery(id+"F3.wireOp",EDGE,"E25.2"),sQuery(id+"F3.wireOp",EDGE,"E25.3"),sQuery(id+"F3.wireOp",EDGE,"E25.4"),sQuery(id+"F3.wireOp",EDGE,"E25.5"),sQuery(id+"F3.wireOp",EDGE,"E25.6"),sQuery(id+"F3.wireOp",EDGE,"E25.7"),sQuery(id+"F3.wireOp",EDGE,"E25.8"),sQuery(id+"F3.wireOp",EDGE,"E25.9"),sQuery(id+"F3.wireOp",EDGE,"E25.10"),sQuery(id+"F3.wireOp",EDGE,"E25.11")])]})})});
            var Q121;
            Q121=makeQuery(id+"F12.boolean.opBoolean","SPLIT",BODY,{"disambiguationData":[OD(100.0)],"derivedFrom":makeQuery(id+"F10.boolean.opBoolean","SPLIT",BODY,{"disambiguationData":[OD(0.0)],"derivedFrom":makeQuery(id+"F4.opExtrude","SWEPT_BODY",BODY,{"disambiguationData":[OSD([sQuery(id+"F3.wireOp",EDGE,"E25.0"),sQuery(id+"F3.wireOp",EDGE,"E25.1"),sQuery(id+"F3.wireOp",EDGE,"E25.2"),sQuery(id+"F3.wireOp",EDGE,"E25.3"),sQuery(id+"F3.wireOp",EDGE,"E25.4"),sQuery(id+"F3.wireOp",EDGE,"E25.5"),sQuery(id+"F3.wireOp",EDGE,"E25.6"),sQuery(id+"F3.wireOp",EDGE,"E25.7"),sQuery(id+"F3.wireOp",EDGE,"E25.8"),sQuery(id+"F3.wireOp",EDGE,"E25.9"),sQuery(id+"F3.wireOp",EDGE,"E25.10"),sQuery(id+"F3.wireOp",EDGE,"E25.11")])]})})});
            var Q122;
            Q122=makeQuery(id+"F12.boolean.opBoolean","SPLIT",BODY,{"disambiguationData":[OD(101.0)],"derivedFrom":makeQuery(id+"F10.boolean.opBoolean","SPLIT",BODY,{"disambiguationData":[OD(0.0)],"derivedFrom":makeQuery(id+"F4.opExtrude","SWEPT_BODY",BODY,{"disambiguationData":[OSD([sQuery(id+"F3.wireOp",EDGE,"E25.0"),sQuery(id+"F3.wireOp",EDGE,"E25.1"),sQuery(id+"F3.wireOp",EDGE,"E25.2"),sQuery(id+"F3.wireOp",EDGE,"E25.3"),sQuery(id+"F3.wireOp",EDGE,"E25.4"),sQuery(id+"F3.wireOp",EDGE,"E25.5"),sQuery(id+"F3.wireOp",EDGE,"E25.6"),sQuery(id+"F3.wireOp",EDGE,"E25.7"),sQuery(id+"F3.wireOp",EDGE,"E25.8"),sQuery(id+"F3.wireOp",EDGE,"E25.9"),sQuery(id+"F3.wireOp",EDGE,"E25.10"),sQuery(id+"F3.wireOp",EDGE,"E25.11")])]})})});
            var Q123;
            Q123=makeQuery(id+"F12.boolean.opBoolean","SPLIT",BODY,{"disambiguationData":[OD(102.0)],"derivedFrom":makeQuery(id+"F10.boolean.opBoolean","SPLIT",BODY,{"disambiguationData":[OD(0.0)],"derivedFrom":makeQuery(id+"F4.opExtrude","SWEPT_BODY",BODY,{"disambiguationData":[OSD([sQuery(id+"F3.wireOp",EDGE,"E25.0"),sQuery(id+"F3.wireOp",EDGE,"E25.1"),sQuery(id+"F3.wireOp",EDGE,"E25.2"),sQuery(id+"F3.wireOp",EDGE,"E25.3"),sQuery(id+"F3.wireOp",EDGE,"E25.4"),sQuery(id+"F3.wireOp",EDGE,"E25.5"),sQuery(id+"F3.wireOp",EDGE,"E25.6"),sQuery(id+"F3.wireOp",EDGE,"E25.7"),sQuery(id+"F3.wireOp",EDGE,"E25.8"),sQuery(id+"F3.wireOp",EDGE,"E25.9"),sQuery(id+"F3.wireOp",EDGE,"E25.10"),sQuery(id+"F3.wireOp",EDGE,"E25.11")])]})})});
            var Q124;
            Q124=makeQuery(id+"F12.boolean.opBoolean","SPLIT",BODY,{"disambiguationData":[OD(103.0)],"derivedFrom":makeQuery(id+"F10.boolean.opBoolean","SPLIT",BODY,{"disambiguationData":[OD(0.0)],"derivedFrom":makeQuery(id+"F4.opExtrude","SWEPT_BODY",BODY,{"disambiguationData":[OSD([sQuery(id+"F3.wireOp",EDGE,"E25.0"),sQuery(id+"F3.wireOp",EDGE,"E25.1"),sQuery(id+"F3.wireOp",EDGE,"E25.2"),sQuery(id+"F3.wireOp",EDGE,"E25.3"),sQuery(id+"F3.wireOp",EDGE,"E25.4"),sQuery(id+"F3.wireOp",EDGE,"E25.5"),sQuery(id+"F3.wireOp",EDGE,"E25.6"),sQuery(id+"F3.wireOp",EDGE,"E25.7"),sQuery(id+"F3.wireOp",EDGE,"E25.8"),sQuery(id+"F3.wireOp",EDGE,"E25.9"),sQuery(id+"F3.wireOp",EDGE,"E25.10"),sQuery(id+"F3.wireOp",EDGE,"E25.11")])]})})});
            var Q125;
            Q125=makeQuery(id+"F12.boolean.opBoolean","SPLIT",BODY,{"disambiguationData":[OD(104.0)],"derivedFrom":makeQuery(id+"F10.boolean.opBoolean","SPLIT",BODY,{"disambiguationData":[OD(0.0)],"derivedFrom":makeQuery(id+"F4.opExtrude","SWEPT_BODY",BODY,{"disambiguationData":[OSD([sQuery(id+"F3.wireOp",EDGE,"E25.0"),sQuery(id+"F3.wireOp",EDGE,"E25.1"),sQuery(id+"F3.wireOp",EDGE,"E25.2"),sQuery(id+"F3.wireOp",EDGE,"E25.3"),sQuery(id+"F3.wireOp",EDGE,"E25.4"),sQuery(id+"F3.wireOp",EDGE,"E25.5"),sQuery(id+"F3.wireOp",EDGE,"E25.6"),sQuery(id+"F3.wireOp",EDGE,"E25.7"),sQuery(id+"F3.wireOp",EDGE,"E25.8"),sQuery(id+"F3.wireOp",EDGE,"E25.9"),sQuery(id+"F3.wireOp",EDGE,"E25.10"),sQuery(id+"F3.wireOp",EDGE,"E25.11")])]})})});
            var Q126;
            Q126=makeQuery(id+"F12.boolean.opBoolean","SPLIT",BODY,{"disambiguationData":[OD(105.0)],"derivedFrom":makeQuery(id+"F10.boolean.opBoolean","SPLIT",BODY,{"disambiguationData":[OD(0.0)],"derivedFrom":makeQuery(id+"F4.opExtrude","SWEPT_BODY",BODY,{"disambiguationData":[OSD([sQuery(id+"F3.wireOp",EDGE,"E25.0"),sQuery(id+"F3.wireOp",EDGE,"E25.1"),sQuery(id+"F3.wireOp",EDGE,"E25.2"),sQuery(id+"F3.wireOp",EDGE,"E25.3"),sQuery(id+"F3.wireOp",EDGE,"E25.4"),sQuery(id+"F3.wireOp",EDGE,"E25.5"),sQuery(id+"F3.wireOp",EDGE,"E25.6"),sQuery(id+"F3.wireOp",EDGE,"E25.7"),sQuery(id+"F3.wireOp",EDGE,"E25.8"),sQuery(id+"F3.wireOp",EDGE,"E25.9"),sQuery(id+"F3.wireOp",EDGE,"E25.10"),sQuery(id+"F3.wireOp",EDGE,"E25.11")])]})})});
            var Q127;
            Q127=makeQuery(id+"F12.boolean.opBoolean","SPLIT",BODY,{"disambiguationData":[OD(106.0)],"derivedFrom":makeQuery(id+"F10.boolean.opBoolean","SPLIT",BODY,{"disambiguationData":[OD(0.0)],"derivedFrom":makeQuery(id+"F4.opExtrude","SWEPT_BODY",BODY,{"disambiguationData":[OSD([sQuery(id+"F3.wireOp",EDGE,"E25.0"),sQuery(id+"F3.wireOp",EDGE,"E25.1"),sQuery(id+"F3.wireOp",EDGE,"E25.2"),sQuery(id+"F3.wireOp",EDGE,"E25.3"),sQuery(id+"F3.wireOp",EDGE,"E25.4"),sQuery(id+"F3.wireOp",EDGE,"E25.5"),sQuery(id+"F3.wireOp",EDGE,"E25.6"),sQuery(id+"F3.wireOp",EDGE,"E25.7"),sQuery(id+"F3.wireOp",EDGE,"E25.8"),sQuery(id+"F3.wireOp",EDGE,"E25.9"),sQuery(id+"F3.wireOp",EDGE,"E25.10"),sQuery(id+"F3.wireOp",EDGE,"E25.11")])]})})});
            var Q128;
            Q128=makeQuery(id+"F12.boolean.opBoolean","SPLIT",BODY,{"disambiguationData":[OD(107.0)],"derivedFrom":makeQuery(id+"F10.boolean.opBoolean","SPLIT",BODY,{"disambiguationData":[OD(0.0)],"derivedFrom":makeQuery(id+"F4.opExtrude","SWEPT_BODY",BODY,{"disambiguationData":[OSD([sQuery(id+"F3.wireOp",EDGE,"E25.0"),sQuery(id+"F3.wireOp",EDGE,"E25.1"),sQuery(id+"F3.wireOp",EDGE,"E25.2"),sQuery(id+"F3.wireOp",EDGE,"E25.3"),sQuery(id+"F3.wireOp",EDGE,"E25.4"),sQuery(id+"F3.wireOp",EDGE,"E25.5"),sQuery(id+"F3.wireOp",EDGE,"E25.6"),sQuery(id+"F3.wireOp",EDGE,"E25.7"),sQuery(id+"F3.wireOp",EDGE,"E25.8"),sQuery(id+"F3.wireOp",EDGE,"E25.9"),sQuery(id+"F3.wireOp",EDGE,"E25.10"),sQuery(id+"F3.wireOp",EDGE,"E25.11")])]})})});
            var Q129;
            Q129=makeQuery(id+"F12.boolean.opBoolean","SPLIT",BODY,{"disambiguationData":[OD(108.0)],"derivedFrom":makeQuery(id+"F10.boolean.opBoolean","SPLIT",BODY,{"disambiguationData":[OD(0.0)],"derivedFrom":makeQuery(id+"F4.opExtrude","SWEPT_BODY",BODY,{"disambiguationData":[OSD([sQuery(id+"F3.wireOp",EDGE,"E25.0"),sQuery(id+"F3.wireOp",EDGE,"E25.1"),sQuery(id+"F3.wireOp",EDGE,"E25.2"),sQuery(id+"F3.wireOp",EDGE,"E25.3"),sQuery(id+"F3.wireOp",EDGE,"E25.4"),sQuery(id+"F3.wireOp",EDGE,"E25.5"),sQuery(id+"F3.wireOp",EDGE,"E25.6"),sQuery(id+"F3.wireOp",EDGE,"E25.7"),sQuery(id+"F3.wireOp",EDGE,"E25.8"),sQuery(id+"F3.wireOp",EDGE,"E25.9"),sQuery(id+"F3.wireOp",EDGE,"E25.10"),sQuery(id+"F3.wireOp",EDGE,"E25.11")])]})})});
            deleteBodies(context, id + "F13", {"entities" : qUnion([Q0, Q1, Q2, Q3, Q4, Q5, Q6, Q7, Q8, Q9, Q10, Q11, Q12, Q13, Q14, Q15, Q16, Q17, Q18, Q19, Q20, Q21, Q22, Q23, Q24, Q25, Q26, Q27, Q28, Q29, Q30, Q31, Q32, Q33, Q34, Q35, Q36, Q37, Q38, Q39, Q40, Q41, Q42, Q43, Q44, Q45, Q46, Q47, Q48, Q49, Q50, Q51, Q52, Q53, Q54, Q55, Q56, Q57, Q58, Q59, Q60, Q61, Q62, Q63, Q64, Q65, Q66, Q67, Q68, Q69, Q70, Q71, Q72, Q73, Q74, Q75, Q76, Q77, Q78, Q79, Q80, Q81, Q82, Q83, Q84, Q85, Q86, Q87, Q88, Q89, Q90, Q91, Q92, Q93, Q94, Q95, Q96, Q97, Q98, Q99, Q100, Q101, Q102, Q103, Q104, Q105, Q106, Q107, Q108, Q109, Q110, Q111, Q112, Q113, Q114, Q115, Q116, Q117, Q118, Q119, Q120, Q121, Q122, Q123, Q124, Q125, Q126, Q127, Q128, Q129])});
        }
        {
            var Q0;
            Q0=makeQuery(id+"F1.opExtrude","CAP_FACE",FACE,{"disambiguationData":[OSD([sQuery(id+"F0.wireOp",EDGE,"E0"),sQuery(id+"F0.wireOp",EDGE,"E1.0.1.0"),sQuery(id+"F0.wireOp",EDGE,"E1.0.2.0"),sQuery(id+"F0.wireOp",EDGE,"E1.0.3.0"),sQuery(id+"F0.wireOp",EDGE,"E1.1.0.0"),sQuery(id+"F0.wireOp",EDGE,"E1.1.1.0"),sQuery(id+"F0.wireOp",EDGE,"E1.1.2.0"),sQuery(id+"F0.wireOp",EDGE,"E1.1.3.0"),sQuery(id+"F0.wireOp",EDGE,"E1.2.0.0"),sQuery(id+"F0.wireOp",EDGE,"E1.2.1.0"),sQuery(id+"F0.wireOp",EDGE,"E1.2.2.0"),sQuery(id+"F0.wireOp",EDGE,"E1.2.3.0"),sQuery(id+"F0.wireOp",EDGE,"E1.3.0.0"),sQuery(id+"F0.wireOp",EDGE,"E1.3.1.0"),sQuery(id+"F0.wireOp",EDGE,"E1.3.2.0"),sQuery(id+"F0.wireOp",EDGE,"E1.3.3.0"),sQuery(id+"F0.wireOp",EDGE,"E1.4.0.0"),sQuery(id+"F0.wireOp",EDGE,"E1.4.1.0"),sQuery(id+"F0.wireOp",EDGE,"E1.4.2.0"),sQuery(id+"F0.wireOp",EDGE,"E1.4.3.0"),sQuery(id+"F0.wireOp",EDGE,"E1.5.0.0"),sQuery(id+"F0.wireOp",EDGE,"E1.5.1.0"),sQuery(id+"F0.wireOp",EDGE,"E1.5.2.0"),sQuery(id+"F0.wireOp",EDGE,"E1.5.3.0"),sQuery(id+"F0.wireOp",EDGE,"E1.6.0.0"),sQuery(id+"F0.wireOp",EDGE,"E1.6.1.0"),sQuery(id+"F0.wireOp",EDGE,"E1.6.2.0"),sQuery(id+"F0.wireOp",EDGE,"E1.6.3.0"),sQuery(id+"F0.wireOp",EDGE,"E1.7.0.0"),sQuery(id+"F0.wireOp",EDGE,"E1.7.1.0"),sQuery(id+"F0.wireOp",EDGE,"E1.7.2.0"),sQuery(id+"F0.wireOp",EDGE,"E1.7.3.0"),sQuery(id+"F0.wireOp",EDGE,"E1.8.0.0"),sQuery(id+"F0.wireOp",EDGE,"E1.8.1.0"),sQuery(id+"F0.wireOp",EDGE,"E1.8.2.0"),sQuery(id+"F0.wireOp",EDGE,"E1.8.3.0"),sQuery(id+"F0.wireOp",EDGE,"E1.9.0.0"),sQuery(id+"F0.wireOp",EDGE,"E1.9.1.0"),sQuery(id+"F0.wireOp",EDGE,"E1.9.2.0"),sQuery(id+"F0.wireOp",EDGE,"E1.9.3.0"),sQuery(id+"F0.wireOp",EDGE,"E2.0.10.0"),sQuery(id+"F0.wireOp",EDGE,"E2.0.10.1"),sQuery(id+"F0.wireOp",EDGE,"E2.0.10.2"),sQuery(id+"F0.wireOp",EDGE,"E2.0.10.3"),sQuery(id+"F0.wireOp",EDGE,"E2.0.11.0"),sQuery(id+"F0.wireOp",EDGE,"E2.0.11.1"),sQuery(id+"F0.wireOp",EDGE,"E2.0.11.2"),sQuery(id+"F0.wireOp",EDGE,"E2.0.11.3"),sQuery(id+"F0.wireOp",EDGE,"E2.0.12.0"),sQuery(id+"F0.wireOp",EDGE,"E2.0.12.1"),sQuery(id+"F0.wireOp",EDGE,"E2.0.12.2"),sQuery(id+"F0.wireOp",EDGE,"E2.0.12.3"),sQuery(id+"F0.wireOp",EDGE,"E2.0.13.0"),sQuery(id+"F0.wireOp",EDGE,"E2.0.13.1"),sQuery(id+"F0.wireOp",EDGE,"E2.0.13.2"),sQuery(id+"F0.wireOp",EDGE,"E2.0.13.3"),sQuery(id+"F0.wireOp",EDGE,"E2.0.14.0"),sQuery(id+"F0.wireOp",EDGE,"E2.0.14.1"),sQuery(id+"F0.wireOp",EDGE,"E2.0.14.2"),sQuery(id+"F0.wireOp",EDGE,"E2.0.14.3"),sQuery(id+"F0.wireOp",EDGE,"E2.0.15.0"),sQuery(id+"F0.wireOp",EDGE,"E2.0.15.1"),sQuery(id+"F0.wireOp",EDGE,"E2.0.15.2"),sQuery(id+"F0.wireOp",EDGE,"E2.0.15.3"),sQuery(id+"F0.wireOp",EDGE,"E2.0.16.0"),sQuery(id+"F0.wireOp",EDGE,"E2.0.16.1"),sQuery(id+"F0.wireOp",EDGE,"E2.0.16.2"),sQuery(id+"F0.wireOp",EDGE,"E2.0.16.3"),sQuery(id+"F0.wireOp",EDGE,"E2.0.17.0"),sQuery(id+"F0.wireOp",EDGE,"E2.0.17.1"),sQuery(id+"F0.wireOp",EDGE,"E2.0.17.2"),sQuery(id+"F0.wireOp",EDGE,"E2.0.17.3"),sQuery(id+"F0.wireOp",EDGE,"E2.0.18.0"),sQuery(id+"F0.wireOp",EDGE,"E2.0.18.1"),sQuery(id+"F0.wireOp",EDGE,"E2.0.18.2"),sQuery(id+"F0.wireOp",EDGE,"E2.0.18.3"),sQuery(id+"F0.wireOp",EDGE,"E2.0.19.0"),sQuery(id+"F0.wireOp",EDGE,"E2.0.19.1"),sQuery(id+"F0.wireOp",EDGE,"E2.0.19.2"),sQuery(id+"F0.wireOp",EDGE,"E2.0.19.3"),sQuery(id+"F0.wireOp",EDGE,"E3.0.20.0"),sQuery(id+"F0.wireOp",EDGE,"E3.0.20.1"),sQuery(id+"F0.wireOp",EDGE,"E3.0.20.2"),sQuery(id+"F0.wireOp",EDGE,"E3.0.20.3"),sQuery(id+"F0.wireOp",EDGE,"E3.0.21.0"),sQuery(id+"F0.wireOp",EDGE,"E3.0.21.1"),sQuery(id+"F0.wireOp",EDGE,"E3.0.21.2"),sQuery(id+"F0.wireOp",EDGE,"E3.0.21.3"),sQuery(id+"F0.wireOp",EDGE,"E3.0.22.0"),sQuery(id+"F0.wireOp",EDGE,"E3.0.22.1"),sQuery(id+"F0.wireOp",EDGE,"E3.0.22.2"),sQuery(id+"F0.wireOp",EDGE,"E3.0.22.3"),sQuery(id+"F0.wireOp",EDGE,"E3.0.23.0"),sQuery(id+"F0.wireOp",EDGE,"E3.0.23.1"),sQuery(id+"F0.wireOp",EDGE,"E3.0.23.2"),sQuery(id+"F0.wireOp",EDGE,"E3.0.23.3"),sQuery(id+"F0.wireOp",EDGE,"E8"),sQuery(id+"F0.wireOp",EDGE,"E9.0.1.0"),sQuery(id+"F0.wireOp",EDGE,"E9.0.2.0"),sQuery(id+"F0.wireOp",EDGE,"E9.0.3.0"),sQuery(id+"F0.wireOp",EDGE,"E9.1.0.0"),sQuery(id+"F0.wireOp",EDGE,"E9.1.1.0"),sQuery(id+"F0.wireOp",EDGE,"E9.1.2.0"),sQuery(id+"F0.wireOp",EDGE,"E9.1.3.0"),sQuery(id+"F0.wireOp",EDGE,"E9.2.0.0"),sQuery(id+"F0.wireOp",EDGE,"E9.2.1.0"),sQuery(id+"F0.wireOp",EDGE,"E9.2.2.0"),sQuery(id+"F0.wireOp",EDGE,"E9.2.3.0"),sQuery(id+"F0.wireOp",EDGE,"E9.3.0.0"),sQuery(id+"F0.wireOp",EDGE,"E9.3.1.0"),sQuery(id+"F0.wireOp",EDGE,"E9.3.2.0"),sQuery(id+"F0.wireOp",EDGE,"E9.3.3.0"),sQuery(id+"F0.wireOp",EDGE,"E9.4.0.0"),sQuery(id+"F0.wireOp",EDGE,"E9.4.1.0"),sQuery(id+"F0.wireOp",EDGE,"E9.4.2.0"),sQuery(id+"F0.wireOp",EDGE,"E9.4.3.0"),sQuery(id+"F0.wireOp",EDGE,"E9.5.0.0"),sQuery(id+"F0.wireOp",EDGE,"E9.5.1.0"),sQuery(id+"F0.wireOp",EDGE,"E9.5.2.0"),sQuery(id+"F0.wireOp",EDGE,"E9.5.3.0"),sQuery(id+"F0.wireOp",EDGE,"E9.6.0.0"),sQuery(id+"F0.wireOp",EDGE,"E9.6.1.0"),sQuery(id+"F0.wireOp",EDGE,"E9.6.2.0"),sQuery(id+"F0.wireOp",EDGE,"E9.6.3.0"),sQuery(id+"F0.wireOp",EDGE,"E9.7.0.0"),sQuery(id+"F0.wireOp",EDGE,"E9.7.1.0"),sQuery(id+"F0.wireOp",EDGE,"E9.7.2.0"),sQuery(id+"F0.wireOp",EDGE,"E9.7.3.0"),sQuery(id+"F0.wireOp",EDGE,"E9.8.0.0"),sQuery(id+"F0.wireOp",EDGE,"E9.8.1.0"),sQuery(id+"F0.wireOp",EDGE,"E9.8.2.0"),sQuery(id+"F0.wireOp",EDGE,"E9.8.3.0"),sQuery(id+"F0.wireOp",EDGE,"E9.9.0.0"),sQuery(id+"F0.wireOp",EDGE,"E9.9.1.0"),sQuery(id+"F0.wireOp",EDGE,"E9.9.2.0"),sQuery(id+"F0.wireOp",EDGE,"E9.9.3.0"),sQuery(id+"F0.wireOp",EDGE,"E9.10.0.0"),sQuery(id+"F0.wireOp",EDGE,"E9.10.1.0"),sQuery(id+"F0.wireOp",EDGE,"E9.10.2.0"),sQuery(id+"F0.wireOp",EDGE,"E9.10.3.0"),sQuery(id+"F0.wireOp",EDGE,"E9.11.0.0"),sQuery(id+"F0.wireOp",EDGE,"E9.11.1.0"),sQuery(id+"F0.wireOp",EDGE,"E9.11.2.0"),sQuery(id+"F0.wireOp",EDGE,"E9.11.3.0"),sQuery(id+"F0.wireOp",EDGE,"E9.12.0.0"),sQuery(id+"F0.wireOp",EDGE,"E9.12.1.0"),sQuery(id+"F0.wireOp",EDGE,"E9.12.2.0"),sQuery(id+"F0.wireOp",EDGE,"E9.12.3.0"),sQuery(id+"F0.wireOp",EDGE,"E9.13.0.0"),sQuery(id+"F0.wireOp",EDGE,"E9.13.1.0"),sQuery(id+"F0.wireOp",EDGE,"E9.13.2.0"),sQuery(id+"F0.wireOp",EDGE,"E9.13.3.0"),sQuery(id+"F0.wireOp",EDGE,"E9.14.0.0"),sQuery(id+"F0.wireOp",EDGE,"E9.14.1.0"),sQuery(id+"F0.wireOp",EDGE,"E9.14.2.0"),sQuery(id+"F0.wireOp",EDGE,"E9.14.3.0"),sQuery(id+"F0.wireOp",EDGE,"E9.15.0.0"),sQuery(id+"F0.wireOp",EDGE,"E9.15.1.0"),sQuery(id+"F0.wireOp",EDGE,"E9.15.2.0"),sQuery(id+"F0.wireOp",EDGE,"E9.15.3.0"),sQuery(id+"F0.wireOp",EDGE,"E10.0"),sQuery(id+"F0.wireOp",EDGE,"E11.0"),sQuery(id+"F0.wireOp",EDGE,"E12.0"),sQuery(id+"F0.wireOp",EDGE,"E13.0"),sQuery(id+"F0.wireOp",EDGE,"E14.0"),sQuery(id+"F0.wireOp",EDGE,"E16"),sQuery(id+"F0.wireOp",EDGE,"E17"),sQuery(id+"F0.wireOp",EDGE,"E18"),sQuery(id+"F0.wireOp",EDGE,"E19"),sQuery(id+"F0.wireOp",EDGE,"E20"),sQuery(id+"F0.wireOp",EDGE,"E22"),sQuery(id+"F0.wireOp",EDGE,"E23"),sQuery(id+"F0.wireOp",EDGE,"E24")])],"isStart":false});
            var sketch = newSketch(context, id + "F14", { "sketchPlane" : qUnion([Q0]) });
            skLineSegment(sketch, "E62.0", {"start": v(455.4, 12.4) * mm, "end": v(0, 12.4) * mm, "construction": true});
            skArc(sketch, "E62.1", {"start": v(0, 12.4) * mm, "mid": v(-10.74, 6.2) * mm, "end": v(-10.74, -6.2) * mm, "construction": true});
            skLineSegment(sketch, "E62.2", {"start": v(-10.74, -6.2) * mm, "end": v(18.96, -57.64) * mm, "construction": true});
            skArc(sketch, "E62.3", {"start": v(18.96, -57.64) * mm, "mid": v(23.5, -62.18) * mm, "end": v(29.7, -63.84) * mm, "construction": true});
            skLineSegment(sketch, "E62.4", {"start": v(29.7, -63.84) * mm, "end": v(169.4, -63.84) * mm, "construction": true});
            skArc(sketch, "E62.5", {"start": v(169.4, -63.84) * mm, "mid": v(179.4, -66.52) * mm, "end": v(186.71, -73.84) * mm, "construction": true});
            skLineSegment(sketch, "E62.6", {"start": v(216.96, -126.23) * mm, "end": v(186.71, -73.84) * mm, "construction": true});
            skArc(sketch, "E62.7", {"start": v(216.96, -126.23) * mm, "mid": v(221.5, -130.77) * mm, "end": v(227.7, -132.43) * mm, "construction": true});
            skLineSegment(sketch, "E62.8", {"start": v(227.7, -132.43) * mm, "end": v(524.7, -132.43) * mm, "construction": true});
            skArc(sketch, "E62.9", {"start": v(524.7, -132.43) * mm, "mid": v(535.44, -126.23) * mm, "end": v(535.44, -113.83) * mm, "construction": true});
            skLineSegment(sketch, "E62.10", {"start": v(466.14, 6.2) * mm, "end": v(535.44, -113.83) * mm, "construction": true});
            skArc(sketch, "E62.11", {"start": v(466.14, 6.2) * mm, "mid": v(461.6, 10.74) * mm, "end": v(455.4, 12.4) * mm, "construction": true});
            skLineSegment(sketch, "E63", {"start": v(455.4, 12.4) * mm, "end": v(594, 12.4) * mm, "construction": true});
            skLineSegment(sketch, "E64", {"start": v(535.44, -126.23) * mm, "end": v(604.74, -6.2) * mm, "construction": true});
            skArc(sketch, "E65", {"start": v(524.7, -132.43) * mm, "mid": v(530.9, -130.77) * mm, "end": v(535.44, -126.23) * mm, "construction": true});
            skPoint(sketch, "E66.visualSharp", {"position": v(615.48, 12.4) * mm});
            skArc(sketch, "E66.filletArc", {"start": v(604.74, -6.2) * mm, "mid": v(604.74, 6.2) * mm, "end": v(594, 12.4) * mm, "construction": true});
            skLineSegment(sketch, "E67.0", {"start": v(227.7, -140.43) * mm, "end": v(524.7, -140.43) * mm});
            skArc(sketch, "E67.1", {"start": v(210.03, -130.23) * mm, "mid": v(217.5, -137.7) * mm, "end": v(227.7, -140.43) * mm});
            skLineSegment(sketch, "E67.2", {"start": v(455.4, 20.4) * mm, "end": v(0, 20.4) * mm});
            skLineSegment(sketch, "E67.3", {"start": v(455.4, 20.4) * mm, "end": v(594, 20.4) * mm});
            skArc(sketch, "E67.4", {"start": v(611.67, -10.2) * mm, "mid": v(611.67, 10.2) * mm, "end": v(594, 20.4) * mm});
            skLineSegment(sketch, "E67.5", {"start": v(542.37, -130.23) * mm, "end": v(611.67, -10.2) * mm});
            skArc(sketch, "E67.6", {"start": v(0, 20.4) * mm, "mid": v(-17.67, 10.2) * mm, "end": v(-17.67, -10.2) * mm});
            skLineSegment(sketch, "E67.7", {"start": v(-17.67, -10.2) * mm, "end": v(12.03, -61.64) * mm});
            skArc(sketch, "E67.8", {"start": v(524.7, -140.43) * mm, "mid": v(534.9, -137.7) * mm, "end": v(542.37, -130.23) * mm});
            skArc(sketch, "E67.9", {"start": v(12.03, -61.64) * mm, "mid": v(19.5, -69.1) * mm, "end": v(29.7, -71.84) * mm});
            skLineSegment(sketch, "E67.10", {"start": v(29.7, -71.84) * mm, "end": v(169.4, -71.84) * mm});
            skArc(sketch, "E67.11", {"start": v(169.4, -71.84) * mm, "mid": v(175.4, -73.45) * mm, "end": v(179.79, -77.84) * mm});
            skLineSegment(sketch, "E67.12", {"start": v(210.03, -130.23) * mm, "end": v(179.79, -77.84) * mm});
            skSolve(sketch);
        }
        {
            var Q0;
            Q0 = qSketchRegion(id + "F14", true);
            extrude(context, id + "F15", {"entities" : qUnion([Q0]), "operationType" : NewBodyOperationType.ADD, "depth" : 5 * mm});
        }
    });
